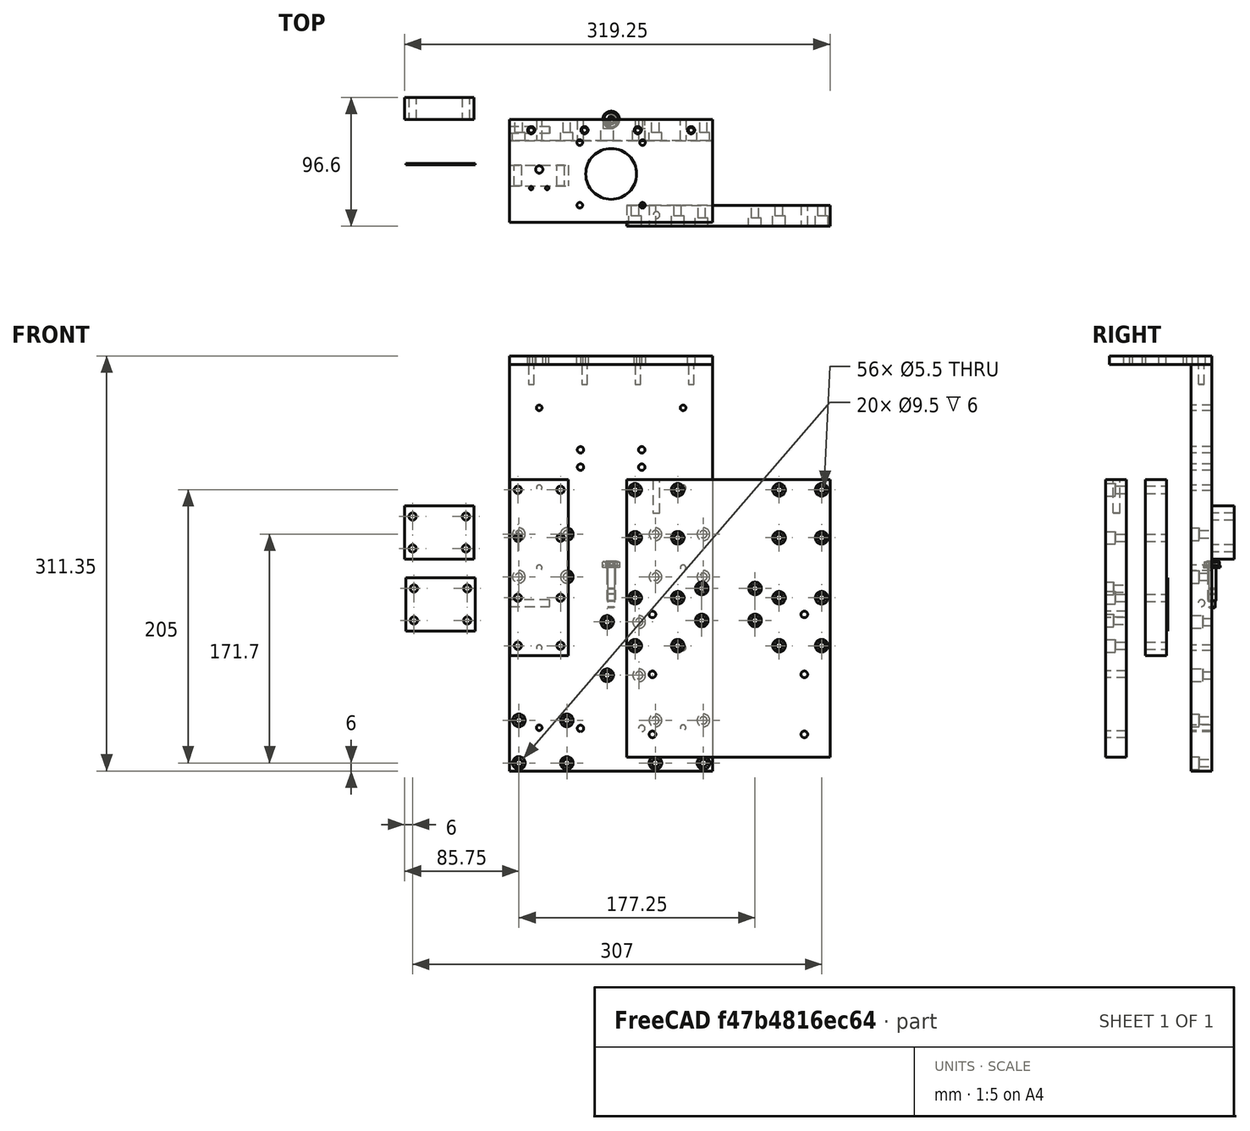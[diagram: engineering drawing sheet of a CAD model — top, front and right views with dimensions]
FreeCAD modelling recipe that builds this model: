
FCSTD DOCUMENT  (FreeCAD 2021.717R24301 +3842 (Git))
Label: Z axis plates
License: Creative Commons Attribution
LicenseURL: http://creativecommons.org/licenses/by/4.0/
objects: App::FeaturePython×171, Part::FeaturePython×140, TechDraw::DrawViewDimension×96, App::LinkElement×44, Sketcher::SketchObject×16, App::Link×16, PartDesign::Pocket×7, PartDesign::Pad×6, PartDesign::Body×6, TechDraw::DrawSVGTemplate×6, TechDraw::DrawViewPart×6, TechDraw::DrawPage×6, PartDesign::ShapeBinder×5, PartDesign::Hole×4, TechDraw::DrawProjGroupItem×4, App::DocumentObjectGroup×3, TechDraw::DrawProjGroup×2, PartDesign::Mirrored×1, TechDraw::DrawViewSection×1, TechDraw::DrawViewAnnotation×1
note: 215 computed .brp shape members not serialized (recipe doc carries the construction recipe); baked Part::Feature solids carry a one-line shape summary decoded from their .brp

FEATURE [Sketcher::SketchObject] Sketch
  FullyConstrained = true
  MapMode = 5
  Placement = pos=(0,0,0) rot=(1,0,0;1.5708rad)
  Support = -> [XZ_Plane]
  sketch-geometry (4):
    g0: LineSegment StartX=-76.25 StartY=152.5 StartZ=0 EndX=76.25 EndY=152.5 EndZ=0
    g1: LineSegment StartX=76.25 StartY=152.5 StartZ=0 EndX=76.25 EndY=-152.5 EndZ=0
    g2: LineSegment StartX=76.25 StartY=-152.5 StartZ=0 EndX=-76.25 EndY=-152.5 EndZ=0
    g3: LineSegment StartX=-76.25 StartY=-152.5 StartZ=0 EndX=-76.25 EndY=152.5 EndZ=0
  constraints (11):
    c: Coincident(g0,g1)
    c: Coincident(g1,g2)
    c: Coincident(g2,g3)
    c: Coincident(g3,g0)
    c: Horizontal(g0)
    c: Horizontal(g2)
    c: Vertical(g1)
    c: Vertical(g3)
    c: Symmetric(g1,g0,g-1)
    c: DistanceX(g0,g0) = 152.5
    c: DistanceY(g1,g1) = 305
FEATURE [PartDesign::Pad] Pad
  ClaimChildren = false
  Direction = (1,1,1)
  Fit = 0
  FitJoin = 0
  InnerFit = 0
  InnerFitJoin = 0
  InnerTaperAngle = 0
  InnerTaperAngleRev = 0
  Length = 15.7
  Length2 = 100
  Linearize = true
  NewSolid = false
  Placement = pos=(0,0,0) rot=(1,0,0;1.5708rad)
  Profile = -> Sketch
  Refine = true
  Suppress = false
  Type = 0
  _ProfileBasedVersion = 0
FEATURE [Sketcher::SketchObject] Sketch001
  FullyConstrained = true
  MapMode = 5
  Placement = pos=(0,0,0) rot=(1,0,0;1.5708rad)
  Support = -> [XZ_Plane]
  sketch-geometry (9):
    g0: Circle CenterX=-54 CenterY=0 CenterZ=0 NormalX=0 NormalY=0 NormalZ=1 AngleXU=0 Radius=2.1
    g1: Circle CenterX=-54 CenterY=60 CenterZ=0 NormalX=0 NormalY=0 NormalZ=1 AngleXU=0 Radius=2.1
    g2: Circle CenterX=-54 CenterY=120 CenterZ=0 NormalX=0 NormalY=0 NormalZ=1 AngleXU=0 Radius=2.1
    g3: Circle CenterX=-54 CenterY=-60 CenterZ=0 NormalX=0 NormalY=0 NormalZ=1 AngleXU=0 Radius=2.1
    g4: Circle CenterX=-54 CenterY=-120 CenterZ=0 NormalX=0 NormalY=0 NormalZ=1 AngleXU=0 Radius=2.1
    g5: LineSegment [constr] StartX=-54 StartY=120 StartZ=0 EndX=-54 EndY=60 EndZ=0
    g6: LineSegment [constr] StartX=-54 StartY=60 StartZ=0 EndX=-54 EndY=0 EndZ=0
    g7: LineSegment [constr] StartX=-54 StartY=0 StartZ=0 EndX=-54 EndY=-60 EndZ=0
    g8: LineSegment [constr] StartX=-54 StartY=-60 StartZ=0 EndX=-54 EndY=-120 EndZ=0
  constraints (23):
    c: Vertical(g4,g3)
    c: Vertical(g3,g0)
    c: Vertical(g0,g1)
    c: Vertical(g1,g2)
    c: Equal(g2,g1)
    c: Equal(g1,g0)
    c: Equal(g0,g3)
    c: Equal(g3,g4)
    c: Coincident(g5,g2)
    c: Coincident(g5,g1)
    c: Coincident(g6,g1)
    c: Coincident(g6,g0)
    c: Coincident(g7,g0)
    c: Coincident(g7,g3)
    c: Coincident(g8,g3)
    c: Coincident(g8,g4)
    c: Equal(g8,g7)
    c: Equal(g7,g6)
    c: Equal(g6,g5)
    c: DistanceY(g5,g5) = 60
    c: DistanceX(g0,g-1) = 54
    c: PointOnObject(g0,g-1)
    c: Radius(g2) = 2.1
FEATURE [PartDesign::Pocket] Pocket
  BaseFeature = -> Pad
  ClaimChildren = false
  Fit = 0
  FitJoin = 0
  InnerFit = 0
  InnerFitJoin = 0
  InnerTaperAngle = 0
  InnerTaperAngleRev = 0
  Length = 5
  Length2 = 100
  Linearize = true
  Midplane = true
  NewSolid = false
  Placement = pos=(0,0,0) rot=(1,0,0;1.5708rad)
  Profile = -> Sketch001
  Refine = true
  Suppress = false
  Type = 1
  _ProfileBasedVersion = 0
FEATURE [PartDesign::Mirrored] Mirrored
  BaseFeature = -> Pocket
  CopyShape = false
  MirrorPlane = -> Sketch001 [V_Axis]
  NewSolid = false
  OriginalSubs = -> [Pocket]
  Originals = -> [Pocket]
  ParallelTransform = true
  Placement = pos=(0,0,0) rot=(1,0,0;1.5708rad)
  Refine = true
  SubTransform = true
  Suppress = false
  _Version = 1
FEATURE [Sketcher::SketchObject] Sketch002
  FullyConstrained = true
  MapMode = 5
  Placement = pos=(0,0,0) rot=(1,0,0;1.5708rad)
  Support = -> [XZ_Plane]
  sketch-geometry (8):
    g0: Circle CenterX=-23 CenterY=-120.525 CenterZ=0 NormalX=0 NormalY=0 NormalZ=1 AngleXU=0 Radius=2.4
    g1: Circle CenterX=23 CenterY=-120.525 CenterZ=0 NormalX=0 NormalY=0 NormalZ=1 AngleXU=0 Radius=2.4
    g2: LineSegment [constr] StartX=-23 StartY=-120.525 StartZ=0 EndX=23 EndY=-120.525 EndZ=0
    g3: GeomPoint [constr] X=0 Y=-120.525 Z=0
    g4: Circle CenterX=-23 CenterY=88.475 CenterZ=0 NormalX=0 NormalY=0 NormalZ=1 AngleXU=0 Radius=2.4
    g5: Circle CenterX=-23 CenterY=75.475 CenterZ=0 NormalX=0 NormalY=0 NormalZ=1 AngleXU=0 Radius=2.4
    g6: Circle CenterX=23 CenterY=88.475 CenterZ=0 NormalX=0 NormalY=0 NormalZ=1 AngleXU=0 Radius=2.4
    g7: Circle CenterX=23 CenterY=75.475 CenterZ=0 NormalX=0 NormalY=0 NormalZ=1 AngleXU=0 Radius=2.4
  constraints (21):
    c: Equal(g1,g0)
    c: Coincident(g2,g0)
    c: Coincident(g2,g1)
    c: Horizontal(g2)
    c: PointOnObject(g3,g-2)
    c: Symmetric(g0,g1,g3)
    c: Radius(g1) = 2.4
    c: DistanceX(g2,g2) = 46
    c: DistanceY(g3,g-1) = 120.525
    c: Equal(g6,g7)
    c: Equal(g7,g5)
    c: Equal(g5,g4)
    c: Equal(g4,g1)
    c: Vertical(g7,g6)
    c: Vertical(g6,g1)
    c: Vertical(g4,g5)
    c: Vertical(g5,g0)
    c: Horizontal(g4,g6)
    c: Horizontal(g5,g7)
    c: DistanceY(g7,g6) = 13
    c: DistanceY(g1,g7) = 196
FEATURE [PartDesign::Pocket] Pocket001
  BaseFeature = -> Mirrored
  ClaimChildren = false
  Fit = 0
  FitJoin = 0
  InnerFit = 0
  InnerFitJoin = 0
  InnerTaperAngle = 0
  InnerTaperAngleRev = 0
  Length = 5
  Length2 = 100
  Linearize = true
  Midplane = true
  NewSolid = false
  Placement = pos=(0,0,0) rot=(1,0,0;1.5708rad)
  Profile = -> Sketch002
  Refine = true
  Suppress = false
  Type = 1
  _ProfileBasedVersion = 0
FEATURE [PartDesign::ShapeBinder] ShapeBinder
  Placement = pos=(0,0,0) rot=(1,0,0;1.5708rad)
  Support = -> [Pocket001]
  TraceSupport = false
FEATURE [Sketcher::SketchObject] Sketch003
  FullyConstrained = true
  MapMode = 5
  Placement = pos=(0,0,0) rot=(1,0,0;1.5708rad)
  Support = -> [XZ_Plane001]
  sketch-geometry (4):
    g0: LineSegment StartX=-76.25 StartY=66 StartZ=0 EndX=76.25 EndY=66 EndZ=0
    g1: LineSegment StartX=76.25 StartY=66 StartZ=0 EndX=76.25 EndY=-142 EndZ=0
    g2: LineSegment StartX=76.25 StartY=-142 StartZ=0 EndX=-76.25 EndY=-142 EndZ=0
    g3: LineSegment StartX=-76.25 StartY=-142 StartZ=0 EndX=-76.25 EndY=66 EndZ=0
  constraints (11):
    c: Coincident(g0,g1)
    c: Coincident(g1,g2)
    c: Coincident(g2,g3)
    c: Coincident(g3,g0)
    c: Horizontal(g2)
    c: Vertical(g1)
    c: Vertical(g3)
    c: DistanceX(g0,g0) = 152.5
    c: DistanceY(g1,g1) = 208
    c: Symmetric(g0,g0,g-2)
    c: DistanceY(g-1,g0) = 66
FEATURE [PartDesign::Pad] Pad001
  ClaimChildren = false
  Direction = (1,1,1)
  Fit = 0
  FitJoin = 0
  InnerFit = 0
  InnerFitJoin = 0
  InnerTaperAngle = 0
  InnerTaperAngleRev = 0
  Length = 15.7
  Length2 = 100
  Linearize = true
  Midplane = true
  NewSolid = false
  Placement = pos=(0,0,0) rot=(1,0,0;1.5708rad)
  Profile = -> Sketch003
  Refine = true
  Suppress = false
  Type = 0
  _ProfileBasedVersion = 0
FEATURE [Sketcher::SketchObject] Sketch004
  ExternalGeometry = -> [ShapeBinder]
  FullyConstrained = true
  MapMode = 5
  Placement = pos=(0,-7.85,-1.7e-15) rot=(1,0,0;1.5708rad)
  Support = -> [Pad001]
  sketch-geometry (21):
    g0: Circle CenterX=-70 CenterY=58.5 CenterZ=0 NormalX=0 NormalY=0 NormalZ=1 AngleXU=0 Radius=2.75
    g1: Circle CenterX=-38 CenterY=58.5 CenterZ=0 NormalX=0 NormalY=0 NormalZ=1 AngleXU=0 Radius=2.75
    g2: Circle CenterX=-70 CenterY=22.5 CenterZ=0 NormalX=0 NormalY=0 NormalZ=1 AngleXU=0 Radius=2.75
    g3: Circle CenterX=-38 CenterY=22.5 CenterZ=0 NormalX=0 NormalY=0 NormalZ=1 AngleXU=0 Radius=2.75
    g4: Circle CenterX=-70 CenterY=-22.5 CenterZ=0 NormalX=0 NormalY=0 NormalZ=1 AngleXU=0 Radius=2.75
    g5: Circle CenterX=-38 CenterY=-22.5 CenterZ=0 NormalX=0 NormalY=0 NormalZ=1 AngleXU=0 Radius=2.75
    g6: Circle CenterX=-70 CenterY=-58.5 CenterZ=0 NormalX=0 NormalY=0 NormalZ=1 AngleXU=0 Radius=2.75
    g7: Circle CenterX=-38 CenterY=-58.5 CenterZ=0 NormalX=0 NormalY=0 NormalZ=1 AngleXU=0 Radius=2.75
    g8: Circle CenterX=38 CenterY=-22.5 CenterZ=0 NormalX=0 NormalY=0 NormalZ=1 AngleXU=0 Radius=2.75
    g9: Circle CenterX=70 CenterY=-22.5 CenterZ=0 NormalX=0 NormalY=0 NormalZ=1 AngleXU=0 Radius=2.75
    g10: Circle CenterX=38 CenterY=-58.5 CenterZ=0 NormalX=0 NormalY=0 NormalZ=1 AngleXU=0 Radius=2.75
    g11: Circle CenterX=70 CenterY=-58.5 CenterZ=0 NormalX=0 NormalY=0 NormalZ=1 AngleXU=0 Radius=2.75
    g12: Circle CenterX=38 CenterY=22.5 CenterZ=0 NormalX=0 NormalY=0 NormalZ=1 AngleXU=0 Radius=2.75
    g13: Circle CenterX=70 CenterY=22.5 CenterZ=0 NormalX=0 NormalY=0 NormalZ=1 AngleXU=0 Radius=2.75
    g14: Circle CenterX=38 CenterY=58.5 CenterZ=0 NormalX=0 NormalY=0 NormalZ=1 AngleXU=0 Radius=2.75
    g15: Circle CenterX=70 CenterY=58.5 CenterZ=0 NormalX=0 NormalY=0 NormalZ=1 AngleXU=0 Radius=2.75
    g16: LineSegment [constr] StartX=-70 StartY=58.5 StartZ=0 EndX=-70 EndY=22.5 EndZ=0
    g17: LineSegment [constr] StartX=-70 StartY=-22.5 StartZ=0 EndX=-70 EndY=-58.5 EndZ=0
    g18: LineSegment [constr] StartX=-70 StartY=58.5 StartZ=0 EndX=-38 EndY=58.5 EndZ=0
    g19: LineSegment [constr] StartX=38 StartY=58.5 StartZ=0 EndX=70 EndY=58.5 EndZ=0
    g20: GeomPoint [constr] X=-54 Y=58.5 Z=0
  constraints (56):
    c: Horizontal(g0,g1)
    c: Horizontal(g1,g14)
    c: Horizontal(g14,g15)
    c: Horizontal(g2,g3)
    c: Horizontal(g3,g12)
    c: Horizontal(g12,g13)
    c: Horizontal(g4,g5)
    c: Horizontal(g5,g8)
    c: Horizontal(g8,g9)
    c: Horizontal(g6,g7)
    c: Horizontal(g7,g10)
    c: Horizontal(g10,g11)
    c: Equal(g0,g1)
    c: Equal(g1,g14)
    c: Equal(g14,g15)
    c: Equal(g15,g12)
    c: Equal(g12,g13)
    c: Equal(g13,g3)
    c: Equal(g3,g2)
    c: Equal(g2,g4)
    c: Equal(g4,g5)
    c: Equal(g5,g8)
    c: Equal(g8,g9)
    c: Equal(g9,g10)
    c: Equal(g10,g11)
    c: Equal(g11,g7)
    c: Equal(g7,g6)
    c: Vertical(g0,g2)
    c: Vertical(g2,g4)
    c: Vertical(g4,g6)
    c: Vertical(g7,g5)
    c: Vertical(g5,g3)
    c: Vertical(g3,g1)
    c: Vertical(g14,g12)
    c: Vertical(g12,g8)
    c: Vertical(g8,g10)
    c: Vertical(g15,g13)
    c: Vertical(g13,g9)
    c: Vertical(g9,g11)
    c: Coincident(g16,g0)
    c: Coincident(g16,g2)
    c: Coincident(g17,g4)
    c: Coincident(g17,g6)
    c: Coincident(g18,g0)
    c: Coincident(g18,g1)
    c: Coincident(g19,g14)
    c: Coincident(g19,g15)
    c: Equal(g18,g19)
    c: Equal(g16,g17)
    c: Symmetric(g2,g9,g-1)
    c: DistanceX(g18,g18) = 32
    c: DistanceY(g16,g16) = 36
    c: Diameter(g15) = 5.5
    c: DistanceY(g4,g2) = 45
    c: Vertical(g20,g-3)
    c: Symmetric(g0,g1,g20)
FEATURE [PartDesign::Hole] Hole  label="Carriages mounts"
  BaseFeature = -> Pad001
  ClaimChildren = false
  CustomThreadClearance = 0
  Depth = 25
  DepthType = 1
  Diameter = 5.5
  DrillForDepth = false
  DrillPoint = 1
  DrillPointAngle = 118
  Fit = 0
  FitJoin = 0
  HoleCutCountersinkAngle = 90
  HoleCutCustomValues = false
  HoleCutDepth = 7.5
  HoleCutDiameter = 9.5
  HoleCutType = 1
  InnerFit = 0
  InnerFitJoin = 0
  ModelThread = false
  NewSolid = false
  Placement = pos=(0,0,0) rot=(1,0,0;1.5708rad)
  Profile = -> Sketch004
  Refine = true
  Suppress = false
  Tapered = false
  TaperedAngle = 90
  ThreadClass = 0
  ThreadDepth = 444.18
  ThreadDepthType = 0
  ThreadDirection = 0
  ThreadFit = 0
  ThreadSize = 0
  ThreadType = 0
  Threaded = false
  UseCustomThreadClearance = false
  _ProfileBasedVersion = 0
FEATURE [Sketcher::SketchObject] Sketch005
  FullyConstrained = true
  MapMode = 5
  Placement = pos=(0,-7.85,-1.7e-15) rot=(1,0,0;1.5708rad)
  Support = -> [Hole]
  sketch-geometry (4):
    g0: Circle CenterX=-20 CenterY=-15.525 CenterZ=0 NormalX=0 NormalY=0 NormalZ=1 AngleXU=0 Radius=2.75
    g1: Circle CenterX=20 CenterY=-15.525 CenterZ=0 NormalX=0 NormalY=0 NormalZ=1 AngleXU=0 Radius=2.75
    g2: Circle CenterX=-20 CenterY=-39.525 CenterZ=0 NormalX=0 NormalY=0 NormalZ=1 AngleXU=0 Radius=2.75
    g3: Circle CenterX=20 CenterY=-39.525 CenterZ=0 NormalX=0 NormalY=0 NormalZ=1 AngleXU=0 Radius=2.75
  constraints (11):
    c: Horizontal(g2,g3)
    c: Vertical(g0,g2)
    c: Vertical(g1,g3)
    c: DistanceX(g0,g1) = 40
    c: DistanceY(g3,g1) = 24
    c: Diameter(g0) = 5.5
    c: Equal(g0,g1)
    c: Equal(g1,g3)
    c: Equal(g3,g2)
    c: DistanceY(g1,g-1) = 15.525
    c: Symmetric(g1,g0,g-2)
FEATURE [PartDesign::Hole] Hole001  label="Screw mount"
  BaseFeature = -> Hole
  ClaimChildren = false
  CustomThreadClearance = 0
  Depth = 25
  DepthType = 1
  Diameter = 5.5
  DrillForDepth = false
  DrillPoint = 1
  DrillPointAngle = 118
  Fit = 0
  FitJoin = 0
  HoleCutCountersinkAngle = 90
  HoleCutCustomValues = false
  HoleCutDepth = 6
  HoleCutDiameter = 9.5
  HoleCutType = 1
  InnerFit = 0
  InnerFitJoin = 0
  ModelThread = false
  NewSolid = false
  Placement = pos=(0,0,0) rot=(1,0,0;1.5708rad)
  Profile = -> Sketch005
  Refine = true
  Suppress = false
  Tapered = false
  TaperedAngle = 90
  ThreadClass = 0
  ThreadDepth = 444.18
  ThreadDepthType = 0
  ThreadDirection = 0
  ThreadFit = 0
  ThreadSize = 0
  ThreadType = 0
  Threaded = false
  UseCustomThreadClearance = false
  _ProfileBasedVersion = 0
FEATURE [PartDesign::ShapeBinder] ShapeBinder001
  Placement = pos=(0,0,0) rot=(1,0,0;1.5708rad)
  Support = -> [Hole001]
  TraceSupport = false
FEATURE [Sketcher::SketchObject] Sketch006
  ExternalGeometry = -> [ShapeBinder001]
  FullyConstrained = true
  MapMode = 5
  Placement = pos=(0,0,0) rot=(1,0,0;1.5708rad)
  Support = -> [XZ_Plane002]
  sketch-geometry (16):
    g0: LineSegment StartX=-76 StartY=66 StartZ=0 EndX=-32 EndY=66 EndZ=0
    g1: LineSegment StartX=-32 StartY=66 StartZ=0 EndX=-32 EndY=-66 EndZ=0
    g2: LineSegment StartX=-32 StartY=-66 StartZ=0 EndX=-76 EndY=-66 EndZ=0
    g3: LineSegment StartX=-76 StartY=-66 StartZ=0 EndX=-76 EndY=66 EndZ=0
    g4: LineSegment [constr] StartX=-70 StartY=58.5 StartZ=0 EndX=-76 EndY=58.5 EndZ=0
    g5: LineSegment [constr] StartX=-38 StartY=58.5 StartZ=0 EndX=-32 EndY=58.5 EndZ=0
    g6: LineSegment [constr] StartX=-38 StartY=58.5 StartZ=0 EndX=-38 EndY=66 EndZ=0
    g7: LineSegment [constr] StartX=-38 StartY=-58.5 StartZ=0 EndX=-38 EndY=-66 EndZ=0
    g8: Circle CenterX=-70 CenterY=58.5 CenterZ=0 NormalX=0 NormalY=0 NormalZ=1 AngleXU=0 Radius=2.75
    g9: Circle CenterX=-38 CenterY=58.5 CenterZ=0 NormalX=0 NormalY=0 NormalZ=1 AngleXU=0 Radius=2.75
    g10: Circle CenterX=-70 CenterY=22.5 CenterZ=0 NormalX=0 NormalY=0 NormalZ=1 AngleXU=0 Radius=2.75
    g11: Circle CenterX=-38 CenterY=22.5 CenterZ=0 NormalX=0 NormalY=0 NormalZ=1 AngleXU=0 Radius=2.75
    g12: Circle CenterX=-70 CenterY=-22.5 CenterZ=0 NormalX=0 NormalY=0 NormalZ=1 AngleXU=0 Radius=2.75
    g13: Circle CenterX=-38 CenterY=-22.5 CenterZ=0 NormalX=0 NormalY=0 NormalZ=1 AngleXU=0 Radius=2.75
    g14: Circle CenterX=-70 CenterY=-58.5 CenterZ=0 NormalX=0 NormalY=0 NormalZ=1 AngleXU=0 Radius=2.75
    g15: Circle CenterX=-38 CenterY=-58.5 CenterZ=0 NormalX=0 NormalY=0 NormalZ=1 AngleXU=0 Radius=2.75
  constraints (40):
    c: Coincident(g0,g1)
    c: Coincident(g1,g2)
    c: Coincident(g2,g3)
    c: Coincident(g3,g0)
    c: Horizontal(g0)
    c: Horizontal(g2)
    c: Vertical(g1)
    c: Vertical(g3)
    c: DistanceX(g2,g2) = 44
    c: DistanceY(g1,g1) = 132
    c: Coincident(g4,g-3)
    c: PointOnObject(g4,g3)
    c: Horizontal(g4)
    c: Coincident(g5,g-4)
    c: PointOnObject(g5,g1)
    c: Horizontal(g5)
    c: Equal(g5,g4)
    c: Coincident(g6,g-4)
    c: PointOnObject(g6,g0)
    c: Coincident(g7,g-10)
    c: PointOnObject(g7,g2)
    c: Vertical(g7)
    c: Vertical(g6)
    c: Equal(g6,g7)
    c: Coincident(g8,g-3)
    c: Coincident(g9,g-4)
    c: Coincident(g10,g-5)
    c: Coincident(g11,g-6)
    c: Coincident(g12,g-7)
    c: Coincident(g13,g-8)
    c: Coincident(g14,g-9)
    c: Coincident(g15,g-10)
    c: Equal(g15,g14)
    c: Equal(g14,g12)
    c: Equal(g12,g13)
    c: Equal(g13,g10)
    c: Equal(g10,g11)
    c: Equal(g11,g8)
    c: Equal(g8,g9)
    c: Equal(g9,g-4)
FEATURE [PartDesign::Pad] Pad002
  ClaimChildren = false
  Direction = (1,1,1)
  Fit = 0
  FitJoin = 0
  InnerFit = 0
  InnerFitJoin = 0
  InnerTaperAngle = 0
  InnerTaperAngleRev = 0
  Length = 15.7
  Length2 = 100
  Linearize = true
  Midplane = true
  NewSolid = false
  Placement = pos=(0,0,0) rot=(1,0,0;1.5708rad)
  Profile = -> Sketch006
  Refine = true
  Suppress = false
  Type = 0
  _ProfileBasedVersion = 0
FEATURE [PartDesign::Body] Body002  label="Shim"
  AutoGroupSolids = false
  ExportMode = 0
  Group = -> [ShapeBinder001,Sketch006,Pad002]
  Origin = -> Origin002
  Placement = pos=(0,-42,0) rot=(0,0,1;0rad)
  Tip = -> Pad002
  _ExportChildren = -> [ShapeBinder001,Pad002]
  _GroupVersion = 1
FEATURE [App::Link] Link  label="Link(Backplate)"
  AutoLinkLabel = true
  AutoPlacement = true
  LinkedObject = -> Body
  SyncGroupVisibility = false
  _LinkVersion = 1
FEATURE [App::Link] Link001  label="Link001(Shim)"
  AutoLinkLabel = true
  AutoPlacement = true
  LinkPlacement = pos=(0,-42,0) rot=(0,0,1;0rad)
  LinkedObject = -> Body002
  Placement = pos=(0,-42,0) rot=(0,0,1;0rad)
  SyncGroupVisibility = false
  _LinkVersion = 1
FEATURE [Part::FeaturePython] Parts002  # WARN: FeaturePython — macro-defined, semantics opaque (R4)
  Group = -> [Link001]
  GroupMode = 0
  _LinkVersion = 1
FEATURE [App::Link] Link002  label="Link002(Frontplate)"
  AutoLinkLabel = true
  AutoPlacement = true
  LinkPlacement = pos=(88,-72,0) rot=(0,0,1;0rad)
  LinkedObject = -> Body001
  Placement = pos=(88,-72,0) rot=(0,0,1;0rad)
  SyncGroupVisibility = false
  _LinkVersion = 1
FEATURE [PartDesign::ShapeBinder] ShapeBinder002
  Placement = pos=(0,0,0) rot=(1,0,0;1.5708rad)
  TraceSupport = false
FEATURE [Sketcher::SketchObject] Sketch008
  ExternalGeometry = -> [ShapeBinder002]
  FullyConstrained = true
  MapMode = 5
  Placement = pos=(0,0,0) rot=(1,0,0;1.5708rad)
  Support = -> [XZ_Plane003]
  sketch-geometry (10):
    g0: LineSegment StartX=-26 StartY=-7.525 StartZ=0 EndX=26 EndY=-7.525 EndZ=0
    g1: LineSegment StartX=26 StartY=-7.525 StartZ=0 EndX=26 EndY=-47.525 EndZ=0
    g2: LineSegment StartX=26 StartY=-47.525 StartZ=0 EndX=-26 EndY=-47.525 EndZ=0
    g3: LineSegment StartX=-26 StartY=-47.525 StartZ=0 EndX=-26 EndY=-7.525 EndZ=0
    g4: Circle CenterX=20 CenterY=-39.525 CenterZ=0 NormalX=0 NormalY=0 NormalZ=1 AngleXU=0 Radius=2.75
    g5: Circle CenterX=-20 CenterY=-15.525 CenterZ=0 NormalX=0 NormalY=0 NormalZ=1 AngleXU=0 Radius=2.75
    g6: Circle CenterX=-20 CenterY=-39.525 CenterZ=0 NormalX=0 NormalY=0 NormalZ=1 AngleXU=0 Radius=2.75
    g7: Circle CenterX=20 CenterY=-15.525 CenterZ=0 NormalX=0 NormalY=0 NormalZ=1 AngleXU=0 Radius=2.75
    g8: LineSegment [constr] StartX=20 StartY=-15.525 StartZ=0 EndX=20 EndY=-7.525 EndZ=0
    g9: LineSegment [constr] StartX=20 StartY=-39.525 StartZ=0 EndX=20 EndY=-47.525 EndZ=0
  constraints (25):
    c: Coincident(g0,g1)
    c: Coincident(g1,g2)
    c: Coincident(g2,g3)
    c: Coincident(g3,g0)
    c: Horizontal(g2)
    c: Vertical(g1)
    c: Vertical(g3)
    c: DistanceX(g0,g0) = 52
    c: DistanceY(g1,g1) = 40
    c: Equal(g7,g6)
    c: Equal(g6,g4)
    c: Equal(g4,g5)
    c: Symmetric(g0,g0,g-2)
    c: Coincident(g5,g-3)
    c: Coincident(g7,g-4)
    c: Equal(g-4,g7)
    c: Coincident(g-5,g6)
    c: Coincident(g4,g-6)
    c: Coincident(g8,g7)
    c: PointOnObject(g8,g0)
    c: Vertical(g8)
    c: Coincident(g9,g4)
    c: PointOnObject(g9,g2)
    c: Vertical(g9)
    c: Equal(g9,g8)
FEATURE [PartDesign::Pad] Pad003
  ClaimChildren = false
  Direction = (1,1,1)
  Fit = 0
  FitJoin = 0
  InnerFit = 0
  InnerFitJoin = 0
  InnerTaperAngle = 0
  InnerTaperAngleRev = 0
  Length = 0.7
  Length2 = 100
  Linearize = true
  NewSolid = false
  Placement = pos=(0,0,0) rot=(1,0,0;1.5708rad)
  Profile = -> Sketch008
  Refine = true
  Suppress = false
  Type = 0
  _ProfileBasedVersion = 0
FEATURE [PartDesign::Body] Body003  label="Nut-shim"
  AutoGroupSolids = false
  ExportMode = 0
  Group = -> [ShapeBinder002,Sketch008,Pad003]
  Origin = -> Origin003
  Placement = pos=(-128,-33,0) rot=(0,0,1;0rad)
  Tip = -> Pad003
  _ExportChildren = -> [ShapeBinder002,Pad003]
  _GroupVersion = 1
FEATURE [App::Link] Link003  label="Link003(Nut-shim)"
  AutoLinkLabel = true
  AutoPlacement = true
  LinkPlacement = pos=(-128,-33,0) rot=(0,0,1;0rad)
  LinkedObject = -> Body003
  Placement = pos=(-128,-33,0) rot=(0,0,1;0rad)
  SyncGroupVisibility = false
  _LinkVersion = 1
FEATURE [Part::FeaturePython] Parts003  # WARN: FeaturePython — macro-defined, semantics opaque (R4)
  Group = -> [Link003]
  GroupMode = 0
  _LinkVersion = 1
FEATURE [Sketcher::SketchObject] Sketch009
  ExternalGeometry = -> [Pocket001]
  FullyConstrained = true
  MapMode = 5
  Placement = pos=(0,-15.7,-3.5e-15) rot=(1,0,0;1.5708rad)
  Support = -> [Pocket001]
  sketch-geometry (22):
    g0: Circle CenterX=-69.25 CenterY=-146.5 CenterZ=0 NormalX=0 NormalY=0 NormalZ=1 AngleXU=0 Radius=2.75
    g1: Circle CenterX=-69.25 CenterY=-114.5 CenterZ=0 NormalX=0 NormalY=0 NormalZ=1 AngleXU=0 Radius=2.75
    g2: Circle CenterX=-33.25 CenterY=-114.5 CenterZ=0 NormalX=0 NormalY=0 NormalZ=1 AngleXU=0 Radius=2.75
    g3: Circle CenterX=-33.25 CenterY=-146.5 CenterZ=0 NormalX=0 NormalY=0 NormalZ=1 AngleXU=0 Radius=2.75
    g4: Circle CenterX=33.25 CenterY=-114.5 CenterZ=0 NormalX=0 NormalY=0 NormalZ=1 AngleXU=0 Radius=2.75
    g5: Circle CenterX=69.25 CenterY=-114.5 CenterZ=0 NormalX=0 NormalY=0 NormalZ=1 AngleXU=0 Radius=2.75
    g6: Circle CenterX=33.25 CenterY=-146.5 CenterZ=0 NormalX=0 NormalY=0 NormalZ=1 AngleXU=0 Radius=2.75
    g7: Circle CenterX=69.25 CenterY=-146.5 CenterZ=0 NormalX=0 NormalY=0 NormalZ=1 AngleXU=0 Radius=2.75
    g8: LineSegment [constr] StartX=-69.25 StartY=-146.5 StartZ=0 EndX=-33.25 EndY=-146.5 EndZ=0
    g9: LineSegment [constr] StartX=33.25 StartY=-146.5 StartZ=0 EndX=69.25 EndY=-146.5 EndZ=0
    g10: Circle CenterX=-69.25 CenterY=-6.8 CenterZ=0 NormalX=0 NormalY=0 NormalZ=1 AngleXU=0 Radius=2.75
    g11: Circle CenterX=-69.25 CenterY=25.2 CenterZ=0 NormalX=0 NormalY=0 NormalZ=1 AngleXU=0 Radius=2.75
    g12: Circle CenterX=-33.25 CenterY=-6.8 CenterZ=0 NormalX=0 NormalY=0 NormalZ=1 AngleXU=0 Radius=2.75
    g13: Circle CenterX=-33.25 CenterY=25.2 CenterZ=0 NormalX=0 NormalY=0 NormalZ=1 AngleXU=0 Radius=2.75
    g14: Circle CenterX=33.25 CenterY=-6.8 CenterZ=0 NormalX=0 NormalY=0 NormalZ=1 AngleXU=0 Radius=2.75
    g15: Circle CenterX=33.25 CenterY=25.2 CenterZ=0 NormalX=0 NormalY=0 NormalZ=1 AngleXU=0 Radius=2.75
    g16: Circle CenterX=69.25 CenterY=-6.8 CenterZ=0 NormalX=0 NormalY=0 NormalZ=1 AngleXU=0 Radius=2.75
    g17: Circle CenterX=69.25 CenterY=25.2 CenterZ=0 NormalX=0 NormalY=0 NormalZ=1 AngleXU=0 Radius=2.75
    g18: GeomPoint [constr] X=69.25 Y=9.2 Z=0
    g19: GeomPoint [constr] X=69.25 Y=-130.5 Z=0
    g20: LineSegment [constr] StartX=-69.25 StartY=-146.5 StartZ=0 EndX=-69.25 EndY=-114.5 EndZ=0
    g21: LineSegment [constr] StartX=-69.25 StartY=25.2 StartZ=0 EndX=-69.25 EndY=-6.8 EndZ=0
  constraints (57):
    c: Horizontal(g5,g4)
    c: Horizontal(g4,g2)
    c: Horizontal(g2,g1)
    c: Horizontal(g0,g3)
    c: Horizontal(g6,g7)
    c: Vertical(g5,g7)
    c: Vertical(g4,g6)
    c: Vertical(g2,g3)
    c: Vertical(g1,g0)
    c: Equal(g1,g2)
    c: Equal(g2,g4)
    c: Equal(g4,g5)
    c: Equal(g5,g6)
    c: Equal(g6,g7)
    c: Equal(g7,g3)
    c: Equal(g3,g0)
    c: Diameter(g1) = 5.5
    c: Coincident(g8,g0)
    c: Coincident(g8,g3)
    c: Coincident(g9,g6)
    c: Coincident(g9,g7)
    c: Equal(g9,g8)
    c: DistanceY(g0,g1) = 32
    c: DistanceX(g8,g8) = 36
    c: Symmetric(g6,g3,g-2)
    c: DistanceY(g-3,g0) = 6
    c: DistanceX(g-3,g0) = 7
    c: Equal(g10,g12)
    c: Equal(g12,g14)
    c: Equal(g14,g16)
    c: Equal(g16,g17)
    c: Equal(g17,g15)
    c: Equal(g15,g13)
    c: Equal(g13,g11)
    c: Equal(g11,g1)
    c: Horizontal(g10,g12)
    c: Horizontal(g12,g14)
    c: Horizontal(g14,g16)
    c: Horizontal(g11,g13)
    c: Horizontal(g13,g15)
    c: Horizontal(g15,g17)
    c: Vertical(g10,g11)
    c: Vertical(g11,g1)
    c: Vertical(g12,g13)
    c: Vertical(g13,g2)
    c: Vertical(g14,g15)
    c: Vertical(g15,g4)
    c: Vertical(g16,g17)
    c: Vertical(g17,g5)
    c: Symmetric(g16,g17,g18)
    c: Symmetric(g5,g7,g19)
    c: DistanceY(g19,g18) = 139.7
    c: Coincident(g20,g0)
    c: Coincident(g20,g1)
    c: Coincident(g21,g11)
    c: Coincident(g21,g10)
    c: Equal(g21,g20)
FEATURE [PartDesign::Hole] Hole003
  BaseFeature = -> Pocket001
  ClaimChildren = false
  CustomThreadClearance = 0
  Depth = 25
  DepthType = 1
  Diameter = 5.5
  DrillForDepth = false
  DrillPoint = 1
  DrillPointAngle = 118
  Fit = 0
  FitJoin = 0
  HoleCutCountersinkAngle = 90
  HoleCutCustomValues = false
  HoleCutDepth = 6
  HoleCutDiameter = 9.5
  HoleCutType = 1
  InnerFit = 0
  InnerFitJoin = 0
  ModelThread = false
  NewSolid = false
  Placement = pos=(0,0,0) rot=(1,0,0;1.5708rad)
  Profile = -> Sketch009
  Refine = true
  Suppress = false
  Tapered = false
  TaperedAngle = 90
  ThreadClass = 0
  ThreadDepth = 689.55
  ThreadDepthType = 0
  ThreadDirection = 0
  ThreadFit = 0
  ThreadSize = 0
  ThreadType = 0
  Threaded = false
  UseCustomThreadClearance = false
  _ProfileBasedVersion = 0
FEATURE [App::Link] Link004  label="Link004(Motor-bracket)"
  AutoLinkLabel = true
  AutoPlacement = true
  LinkedObject = -> Body004
  SyncGroupVisibility = false
  _LinkVersion = 1
FEATURE [Sketcher::SketchObject] Sketch011
  ExternalGeometry = -> [Hole003]
  FullyConstrained = true
  MapMode = 5
  Placement = pos=(0,0,152.5) rot=(0,0,1;3.14159rad)
  Support = -> [Hole003]
  sketch-geometry (9):
    g0: LineSegment [constr] StartX=-60 StartY=15.7 StartZ=0 EndX=-60 EndY=7.85 EndZ=0
    g1: LineSegment [constr] StartX=-60 StartY=7.85 StartZ=0 EndX=-60 EndY=0 EndZ=0
    g2: LineSegment [constr] StartX=-60 StartY=7.85 StartZ=0 EndX=-20 EndY=7.85 EndZ=0
    g3: LineSegment [constr] StartX=-20 StartY=7.85 StartZ=0 EndX=20 EndY=7.85 EndZ=0
    g4: LineSegment [constr] StartX=20 StartY=7.85 StartZ=0 EndX=60 EndY=7.85 EndZ=0
    g5: Circle CenterX=-60 CenterY=7.85 CenterZ=0 NormalX=0 NormalY=0 NormalZ=1 AngleXU=0 Radius=2.1
    g6: Circle CenterX=-20 CenterY=7.85 CenterZ=0 NormalX=0 NormalY=0 NormalZ=1 AngleXU=0 Radius=2.1
    g7: Circle CenterX=20 CenterY=7.85 CenterZ=0 NormalX=0 NormalY=0 NormalZ=1 AngleXU=0 Radius=2.1
    g8: Circle CenterX=60 CenterY=7.85 CenterZ=0 NormalX=0 NormalY=0 NormalZ=1 AngleXU=0 Radius=2.1
  constraints (23):
    c: PointOnObject(g0,g-3)
    c: Vertical(g0)
    c: Coincident(g1,g0)
    c: PointOnObject(g1,g-1)
    c: Coincident(g2,g0)
    c: Horizontal(g2)
    c: Coincident(g3,g2)
    c: Coincident(g4,g3)
    c: Horizontal(g4)
    c: Vertical(g1)
    c: Equal(g1,g0)
    c: Equal(g2,g3)
    c: Equal(g3,g4)
    c: Symmetric(g2,g3,g-2)
    c: Coincident(g5,g0)
    c: Coincident(g6,g2)
    c: Coincident(g7,g3)
    c: Coincident(g8,g4)
    c: Equal(g8,g7)
    c: Equal(g7,g6)
    c: Equal(g6,g5)
    c: Diameter(g8) = 4.2
    c: DistanceX(g3,g3) = 40
FEATURE [PartDesign::Pocket] Pocket002
  BaseFeature = -> Hole003
  ClaimChildren = false
  Fit = 0
  FitJoin = 0
  InnerFit = 0
  InnerFitJoin = 0
  InnerTaperAngle = 0
  InnerTaperAngleRev = 0
  Length = 15
  Length2 = 100
  Linearize = true
  NewSolid = false
  Placement = pos=(0,0,0) rot=(1,0,0;1.5708rad)
  Profile = -> Sketch011
  Refine = true
  Suppress = false
  Type = 0
  _ProfileBasedVersion = 0
FEATURE [PartDesign::ShapeBinder] ShapeBinder003
  Placement = pos=(0,0,0) rot=(1,0,0;1.5708rad)
  Support = -> [Pocket002]
  TraceSupport = false
FEATURE [Sketcher::SketchObject] Sketch010
  ExternalGeometry = -> [ShapeBinder003]
  FullyConstrained = true
  MapMode = 5
  Placement = pos=(0,-3.39e-14,152.5) rot=(0,0,1;3.14159rad)
  Support = -> [ShapeBinder003]
  sketch-geometry (19):
    g0: LineSegment StartX=-76.25 StartY=77.1 StartZ=0 EndX=76.25 EndY=77.1 EndZ=0
    g1: LineSegment StartX=76.25 StartY=77.1 StartZ=0 EndX=76.25 EndY=0 EndZ=0
    g2: LineSegment StartX=-76.25 StartY=0 StartZ=0 EndX=-76.25 EndY=77.1 EndZ=0
    g3: Circle CenterX=0 CenterY=40.7 CenterZ=0 NormalX=0 NormalY=0 NormalZ=1 AngleXU=0 Radius=19.05
    g4: Circle CenterX=-23.55 CenterY=64.25 CenterZ=0 NormalX=0 NormalY=0 NormalZ=1 AngleXU=0 Radius=2.1
    g5: Circle CenterX=23.55 CenterY=64.25 CenterZ=0 NormalX=0 NormalY=0 NormalZ=1 AngleXU=0 Radius=2.1
    g6: Circle CenterX=-23.55 CenterY=17.15 CenterZ=0 NormalX=0 NormalY=0 NormalZ=1 AngleXU=0 Radius=2.1
    g7: Circle CenterX=23.55 CenterY=17.15 CenterZ=0 NormalX=0 NormalY=0 NormalZ=1 AngleXU=0 Radius=2.1
    g8: LineSegment [constr] StartX=-23.55 StartY=64.25 StartZ=0 EndX=23.55 EndY=64.25 EndZ=0
    g9: LineSegment [constr] StartX=23.55 StartY=64.25 StartZ=0 EndX=23.55 EndY=17.15 EndZ=0
    g10: LineSegment [constr] StartX=-28.2 StartY=68.9 StartZ=0 EndX=28.2 EndY=68.9 EndZ=0
    g11: LineSegment [constr] StartX=28.2 StartY=68.9 StartZ=0 EndX=28.2 EndY=12.5 EndZ=0
    g12: LineSegment [constr] StartX=28.2 StartY=12.5 StartZ=0 EndX=-28.2 EndY=12.5 EndZ=0
    g13: LineSegment [constr] StartX=-28.2 StartY=12.5 StartZ=0 EndX=-28.2 EndY=68.9 EndZ=0
    g14: Circle CenterX=-60 CenterY=7.85 CenterZ=0 NormalX=0 NormalY=0 NormalZ=1 AngleXU=0 Radius=2.75
    g15: Circle CenterX=-20 CenterY=7.85 CenterZ=0 NormalX=0 NormalY=0 NormalZ=1 AngleXU=0 Radius=2.75
    g16: Circle CenterX=20 CenterY=7.85 CenterZ=0 NormalX=0 NormalY=0 NormalZ=1 AngleXU=0 Radius=2.75
    g17: Circle CenterX=60 CenterY=7.85 CenterZ=0 NormalX=0 NormalY=0 NormalZ=1 AngleXU=0 Radius=2.75
    g18: LineSegment StartX=-76.25 StartY=0 StartZ=0 EndX=76.25 EndY=0 EndZ=0
  constraints (48):
    c: Coincident(g0,g1)
    c: Coincident(g2,g0)
    c: Horizontal(g0)
    c: Vertical(g1)
    c: Vertical(g2)
    c: Symmetric(g2,g1,g-1)
    c: PointOnObject(g3,g-2)
    c: Diameter(g3) = 38.1
    c: Vertical(g7,g5)
    c: Vertical(g4,g6)
    c: Horizontal(g4,g5)
    c: Horizontal(g6,g7)
    c: Symmetric(g7,g4,g3)
    c: DistanceX(g4,g5) = 47.1
    c: Equal(g5,g4)
    c: Equal(g4,g6)
    c: Equal(g6,g7)
    c: Diameter(g5) = 4.2
    c: Coincident(g8,g4)
    c: Coincident(g8,g5)
    c: Coincident(g9,g5)
    c: Coincident(g9,g7)
    c: Equal(g9,g8)
    c: Coincident(g10,g11)
    c: Coincident(g11,g12)
    c: Coincident(g12,g13)
    c: Coincident(g13,g10)
    c: Horizontal(g10)
    c: Horizontal(g12)
    c: Vertical(g11)
    c: Vertical(g13)
    c: Symmetric(g10,g11,g3)
    c: Equal(g11,g10)
    c: DistanceY(g13,g13) = 56.4
    c: DistanceX(g0,g0) = 152.5
    c: DistanceY(g-4,g3) = 25
    c: Coincident(g14,g-5)
    c: Coincident(g15,g-6)
    c: Coincident(g16,g-7)
    c: Coincident(g17,g-8)
    c: Equal(g17,g16)
    c: Equal(g16,g15)
    c: Equal(g15,g14)
    c: Diameter(g14) = 5.5
    c: Coincident(g18,g2)
    c: Coincident(g18,g1)
    c: Horizontal(g18)
    c: DistanceY(g2,g2) = 77.1
FEATURE [PartDesign::Pad] Pad004
  ClaimChildren = false
  Direction = (1,1,1)
  Fit = 0
  FitJoin = 0
  InnerFit = 0
  InnerFitJoin = 0
  InnerTaperAngle = 0
  InnerTaperAngleRev = 0
  Length = 6.35
  Length2 = 100
  Linearize = true
  NewSolid = false
  Placement = pos=(0,0,0) rot=(1,0,0;1.5708rad)
  Profile = -> Sketch010
  Refine = true
  Suppress = false
  Type = 0
  _ProfileBasedVersion = 0
FEATURE [Sketcher::SketchObject] Sketch012
  ExternalGeometry = -> [Pad001]
  FullyConstrained = true
  MapMode = 5
  Placement = pos=(0,-7.85,-1.7e-15) rot=(1,0,0;1.5708rad)
  sketch-geometry (6):
    g0: Circle CenterX=-57 CenterY=-80 CenterZ=0 NormalX=0 NormalY=0 NormalZ=1 AngleXU=0 Radius=2.5
    g1: Circle CenterX=-57 CenterY=-125 CenterZ=0 NormalX=0 NormalY=0 NormalZ=1 AngleXU=0 Radius=2.5
    g2: Circle CenterX=57 CenterY=-80 CenterZ=0 NormalX=0 NormalY=0 NormalZ=1 AngleXU=0 Radius=2.5
    g3: Circle CenterX=57 CenterY=-125 CenterZ=0 NormalX=0 NormalY=0 NormalZ=1 AngleXU=0 Radius=2.5
    g4: Circle CenterX=-57 CenterY=-35 CenterZ=0 NormalX=0 NormalY=0 NormalZ=1 AngleXU=0 Radius=2.5
    g5: Circle CenterX=57 CenterY=-35 CenterZ=0 NormalX=0 NormalY=0 NormalZ=1 AngleXU=0 Radius=2.5
  constraints (17):
    c: Vertical(g0,g1)
    c: Horizontal(g1,g3)
    c: Equal(g1,g0)
    c: Equal(g0,g2)
    c: Equal(g2,g3)
    c: Diameter(g2) = 5
    c: Symmetric(g2,g0,g-2)
    c: DistanceX(g0,g2) = 114
    c: DistanceY(g1,g0) = 45
    c: Vertical(g3,g2)
    c: DistanceY(g-3,g3) = 17
    c: Vertical(g5,g2)
    c: Vertical(g4,g0)
    c: Horizontal(g4,g5)
    c: Equal(g4,g5)
    c: Equal(g5,g2)
    c: DistanceY(g0,g4) = 45
FEATURE [PartDesign::Pocket] Pocket003
  BaseFeature = -> Hole001
  ClaimChildren = false
  Fit = 0
  FitJoin = 0
  InnerFit = 0
  InnerFitJoin = 0
  InnerTaperAngle = 0
  InnerTaperAngleRev = 0
  Length = 5
  Length2 = 100
  Linearize = true
  NewSolid = false
  Placement = pos=(0,0,0) rot=(1,0,0;1.5708rad)
  Profile = -> Sketch012
  Refine = true
  Suppress = false
  Type = 1
  _ProfileBasedVersion = 0
FEATURE [Sketcher::SketchObject] Sketch013
  ExternalGeometry = -> [Pocket002]
  FullyConstrained = true
  MapMode = 5
  Placement = pos=(0,-15.7,-3.5e-15) rot=(1,0,0;1.5708rad)
  Support = -> [Pocket002]
  sketch-geometry (6):
    g0: Circle CenterX=-3 CenterY=-40.65 CenterZ=0 NormalX=0 NormalY=0 NormalZ=1 AngleXU=0 Radius=2.75
    g1: Circle CenterX=21 CenterY=-40.65 CenterZ=0 NormalX=0 NormalY=0 NormalZ=1 AngleXU=0 Radius=2.75
    g2: Circle CenterX=-3 CenterY=-80.65 CenterZ=0 NormalX=0 NormalY=0 NormalZ=1 AngleXU=0 Radius=2.75
    g3: Circle CenterX=21 CenterY=-80.65 CenterZ=0 NormalX=0 NormalY=0 NormalZ=1 AngleXU=0 Radius=2.75
    g4: GeomPoint [constr] X=33.25 Y=-60.65 Z=0
    g5: GeomPoint [constr] X=21 Y=-60.65 Z=0
  constraints (14):
    c: Equal(g0,g1)
    c: Equal(g1,g3)
    c: Equal(g3,g2)
    c: Vertical(g1,g3)
    c: Vertical(g0,g2)
    c: Horizontal(g2,g3)
    c: DistanceX(g0,g1) = 24
    c: DistanceY(g3,g1) = 40
    c: Horizontal(g4,g5)
    c: Symmetric(g1,g3,g5)
    c: Symmetric(g-4,g-3,g4)
    c: Diameter(g0) = 5.5
    c: DistanceX(g-1,g1) = 21
    c: Horizontal(g0,g1)
FEATURE [PartDesign::Hole] Hole004
  BaseFeature = -> Pocket002
  ClaimChildren = false
  CustomThreadClearance = 0
  Depth = 25
  DepthType = 1
  Diameter = 5.5
  DrillForDepth = false
  DrillPoint = 1
  DrillPointAngle = 118
  Fit = 0
  FitJoin = 0
  HoleCutCountersinkAngle = 90
  HoleCutCustomValues = false
  HoleCutDepth = 9
  HoleCutDiameter = 9.5
  HoleCutType = 1
  InnerFit = 0
  InnerFitJoin = 0
  ModelThread = false
  NewSolid = false
  Placement = pos=(0,0,0) rot=(1,0,0;1.5708rad)
  Profile = -> Sketch013
  Refine = true
  Suppress = false
  Tapered = false
  TaperedAngle = 90
  ThreadClass = 0
  ThreadDepth = 689.55
  ThreadDepthType = 0
  ThreadDirection = 0
  ThreadFit = 0
  ThreadSize = 0
  ThreadType = 0
  Threaded = false
  UseCustomThreadClearance = false
  _ProfileBasedVersion = 0
FEATURE [PartDesign::ShapeBinder] ShapeBinder004
  Support = -> [Pad003]
  TraceSupport = false
FEATURE [PartDesign::Pad] Pad005
  ClaimChildren = false
  Direction = (1,1,1)
  Fit = 0
  FitJoin = 0
  InnerFit = 0
  InnerFitJoin = 0
  InnerTaperAngle = 0
  InnerTaperAngleRev = 0
  Length = 16.75
  Length2 = 100
  Linearize = true
  NewSolid = false
  Profile = -> ShapeBinder004
  Refine = true
  Suppress = false
  Type = 0
  _ProfileBasedVersion = 0
FEATURE [PartDesign::Body] Body005  label="Nut-shim-X"
  AutoGroupSolids = false
  ExportMode = 0
  Group = -> [ShapeBinder004,Pad005]
  Origin = -> Origin005
  Placement = pos=(-129,0,54) rot=(0,0,1;0rad)
  Tip = -> Pad005
  _ExportChildren = -> [Pad005]
  _GroupVersion = 1
FEATURE [App::Link] Link005  label="Link005(Nut-shim-X)"
  AutoLinkLabel = true
  AutoPlacement = true
  LinkPlacement = pos=(-129,0,54) rot=(0,0,1;0rad)
  LinkedObject = -> Body005
  Placement = pos=(-129,0,54) rot=(0,0,1;0rad)
  SyncGroupVisibility = false
  _LinkVersion = 1
FEATURE [Part::FeaturePython] Parts005  # WARN: FeaturePython — macro-defined, semantics opaque (R4)
  Group = -> [Link005]
  GroupMode = 0
  _LinkVersion = 1
FEATURE [Part::FeaturePython] Screw  label="M5x16-Screw"  # Fasteners workbench fastener (typed FeaturePython)
  diameter = 6
  invert = false
  length = 4
  lengthCustom = 16
  matchOuter = false
  offset = 0
  thread = false
  type = 33
FEATURE [App::LinkElement] Link006_i0
  LinkPlacement = pos=(-69.25,29.3,25.2) rot=(1,0,0;1.5708rad)
  LinkedObject = -> Screw
  Placement = pos=(-69.25,29.3,25.2) rot=(1,0,0;1.5708rad)
  _LinkVersion = 1
FEATURE [App::LinkElement] Link006_i1
  LinkPlacement = pos=(-33.25,29.3,25.2) rot=(1,0,0;1.5708rad)
  LinkedObject = -> Screw
  Placement = pos=(-33.25,29.3,25.2) rot=(1,0,0;1.5708rad)
  _LinkVersion = 1
FEATURE [App::LinkElement] Link006_i2
  LinkPlacement = pos=(-69.25,29.3,-6.8) rot=(1,0,0;1.5708rad)
  LinkedObject = -> Screw
  Placement = pos=(-69.25,29.3,-6.8) rot=(1,0,0;1.5708rad)
  _LinkVersion = 1
FEATURE [App::LinkElement] Link006_i3
  LinkPlacement = pos=(33.25,29.3,25.2) rot=(1,0,0;1.5708rad)
  LinkedObject = -> Screw
  Placement = pos=(33.25,29.3,25.2) rot=(1,0,0;1.5708rad)
  _LinkVersion = 1
FEATURE [App::LinkElement] Link006_i4
  LinkPlacement = pos=(69.25,29.3,-6.8) rot=(1,0,0;1.5708rad)
  LinkedObject = -> Screw
  Placement = pos=(69.25,29.3,-6.8) rot=(1,0,0;1.5708rad)
  _LinkVersion = 1
FEATURE [App::LinkElement] Link006_i5
  LinkPlacement = pos=(33.25,29.3,-114.5) rot=(1,0,0;1.5708rad)
  LinkedObject = -> Screw
  Placement = pos=(33.25,29.3,-114.5) rot=(1,0,0;1.5708rad)
  _LinkVersion = 1
FEATURE [App::LinkElement] Link006_i6
  LinkPlacement = pos=(-33.25,29.3,-114.5) rot=(1,0,0;1.5708rad)
  LinkedObject = -> Screw
  Placement = pos=(-33.25,29.3,-114.5) rot=(1,0,0;1.5708rad)
  _LinkVersion = 1
FEATURE [App::LinkElement] Link006_i7
  LinkPlacement = pos=(-69.25,29.3,-114.5) rot=(1,0,0;1.5708rad)
  LinkedObject = -> Screw
  Placement = pos=(-69.25,29.3,-114.5) rot=(1,0,0;1.5708rad)
  _LinkVersion = 1
FEATURE [App::LinkElement] Link006_i8
  LinkPlacement = pos=(33.25,29.3,-146.5) rot=(1,0,0;1.5708rad)
  LinkedObject = -> Screw
  Placement = pos=(33.25,29.3,-146.5) rot=(1,0,0;1.5708rad)
  _LinkVersion = 1
FEATURE [App::LinkElement] Link006_i9
  LinkPlacement = pos=(-33.25,29.3,-146.5) rot=(1,0,0;1.5708rad)
  LinkedObject = -> Screw
  Placement = pos=(-33.25,29.3,-146.5) rot=(1,0,0;1.5708rad)
  _LinkVersion = 1
FEATURE [App::LinkElement] Link006_i10
  LinkPlacement = pos=(-69.25,29.3,-146.5) rot=(1,0,0;1.5708rad)
  LinkedObject = -> Screw
  Placement = pos=(-69.25,29.3,-146.5) rot=(1,0,0;1.5708rad)
  _LinkVersion = 1
FEATURE [App::LinkElement] Link006_i11
  LinkPlacement = pos=(-33.25,29.3,-6.8) rot=(1,0,0;1.5708rad)
  LinkedObject = -> Screw
  Placement = pos=(-33.25,29.3,-6.8) rot=(1,0,0;1.5708rad)
  _LinkVersion = 1
FEATURE [App::LinkElement] Link006_i12
  LinkPlacement = pos=(69.25,29.3,25.2) rot=(1,0,0;1.5708rad)
  LinkedObject = -> Screw
  Placement = pos=(69.25,29.3,25.2) rot=(1,0,0;1.5708rad)
  _LinkVersion = 1
FEATURE [App::LinkElement] Link006_i13
  LinkPlacement = pos=(33.25,29.3,-6.8) rot=(1,0,0;1.5708rad)
  LinkedObject = -> Screw
  Placement = pos=(33.25,29.3,-6.8) rot=(1,0,0;1.5708rad)
  _LinkVersion = 1
FEATURE [App::LinkElement] Link006_i14
  LinkPlacement = pos=(69.25,29.3,-114.5) rot=(1,0,0;1.5708rad)
  LinkedObject = -> Screw
  Placement = pos=(69.25,29.3,-114.5) rot=(1,0,0;1.5708rad)
  _LinkVersion = 1
FEATURE [App::LinkElement] Link006_i15
  LinkPlacement = pos=(69.25,29.3,-146.5) rot=(1,0,0;1.5708rad)
  LinkedObject = -> Screw
  Placement = pos=(69.25,29.3,-146.5) rot=(1,0,0;1.5708rad)
  _LinkVersion = 1
FEATURE [App::Link] Link006  label="M5x16-Screw 16ct"
  AutoLinkLabel = true
  AutoPlacement = true
  ElementCount = 16
  ElementList = -> [Link006_i0,Link006_i1,Link006_i2,Link006_i3,Link006_i4,Link006_i5,Link006_i6,Link006_i7,Link006_i8,Link006_i9,Link006_i10,Link006_i11,Link006_i12,Link006_i13,Link006_i14,Link006_i15]
  LinkPlacement = pos=(0,-39,0) rot=(0,0,1;0rad)
  LinkedObject = -> Screw
  Placement = pos=(0,-39,0) rot=(0,0,1;0rad)
  SyncGroupVisibility = false
  _LinkVersion = 1
FEATURE [Part::FeaturePython] Screw001  label="M5x30-Screw"  # Fasteners workbench fastener (typed FeaturePython)
  diameter = 6
  invert = false
  length = 7
  lengthCustom = 30
  matchOuter = false
  offset = 0
  thread = false
  type = 33
FEATURE [App::LinkElement] Link007_i0
  LinkPlacement = pos=(-3,44.3,-40.65) rot=(1,0,0;1.5708rad)
  LinkedObject = -> Screw001
  Placement = pos=(-3,44.3,-40.65) rot=(1,0,0;1.5708rad)
  _LinkVersion = 1
FEATURE [App::LinkElement] Link007_i1
  LinkPlacement = pos=(21,44.3,-40.65) rot=(1,0,0;1.5708rad)
  LinkedObject = -> Screw001
  Placement = pos=(21,44.3,-40.65) rot=(1,0,0;1.5708rad)
  _LinkVersion = 1
FEATURE [App::LinkElement] Link007_i2
  LinkPlacement = pos=(-3,44.3,-80.65) rot=(1,0,0;1.5708rad)
  LinkedObject = -> Screw001
  Placement = pos=(-3,44.3,-80.65) rot=(1,0,0;1.5708rad)
  _LinkVersion = 1
FEATURE [App::LinkElement] Link007_i3
  LinkPlacement = pos=(21,44.3,-80.65) rot=(1,0,0;1.5708rad)
  LinkedObject = -> Screw001
  Placement = pos=(21,44.3,-80.65) rot=(1,0,0;1.5708rad)
  _LinkVersion = 1
FEATURE [App::Link] Link007  label="M5x30-Screw 4ct"
  AutoLinkLabel = true
  AutoPlacement = true
  ElementCount = 4
  ElementList = -> [Link007_i0,Link007_i1,Link007_i2,Link007_i3]
  LinkPlacement = pos=(0,-51,0) rot=(0,0,1;0rad)
  LinkedObject = -> Screw001
  Placement = pos=(0,-51,0) rot=(0,0,1;0rad)
  SyncGroupVisibility = false
  _LinkVersion = 1
FEATURE [Part::FeaturePython] Screw002  label="M5x20-Screw"  # Fasteners workbench fastener (typed FeaturePython)
  diameter = 6
  invert = false
  length = 5
  lengthCustom = 20
  matchOuter = false
  offset = 0
  thread = false
  type = 33
FEATURE [App::LinkElement] Link008_i0
  LinkPlacement = pos=(-60,-7.84998,-46.15) rot=(0,0,1;3.14159rad)
  LinkedObject = -> Screw002
  Placement = pos=(-60,-7.84998,-46.15) rot=(0,0,1;3.14159rad)
  _LinkVersion = 1
FEATURE [App::LinkElement] Link008_i1
  LinkPlacement = pos=(-20,-7.84998,-46.15) rot=(0,0,1;3.14159rad)
  LinkedObject = -> Screw002
  Placement = pos=(-20,-7.84998,-46.15) rot=(0,0,1;3.14159rad)
  _LinkVersion = 1
FEATURE [App::LinkElement] Link008_i2
  LinkPlacement = pos=(20,-7.84998,-46.15) rot=(0,0,1;3.14159rad)
  LinkedObject = -> Screw002
  Placement = pos=(20,-7.84998,-46.15) rot=(0,0,1;3.14159rad)
  _LinkVersion = 1
FEATURE [App::LinkElement] Link008_i3
  LinkPlacement = pos=(60,-7.84998,-46.15) rot=(0,0,1;3.14159rad)
  LinkedObject = -> Screw002
  Placement = pos=(60,-7.84998,-46.15) rot=(0,0,1;3.14159rad)
  _LinkVersion = 1
FEATURE [App::Link] Link008  label="M5x20-Screw 4ct"
  AutoLinkLabel = true
  AutoPlacement = true
  ElementCount = 4
  ElementList = -> [Link008_i0,Link008_i1,Link008_i2,Link008_i3]
  LinkPlacement = pos=(0,-2.44379e-05,205) rot=(0,0,1;0rad)
  LinkedObject = -> Screw002
  Placement = pos=(0,-2.44379e-05,205) rot=(0,0,1;0rad)
  SyncGroupVisibility = false
  _LinkVersion = 1
FEATURE [Part::FeaturePython] Parts004  # WARN: FeaturePython — macro-defined, semantics opaque (R4)
  Group = -> [Link004,Link008]
  GroupMode = 0
  _LinkVersion = 1
FEATURE [App::LinkElement] Link009_i0
  LinkPlacement = pos=(18,39.65,58.5) rot=(1,0,0;1.5708rad)
  LinkedObject = -> Screw001
  Placement = pos=(18,39.65,58.5) rot=(1,0,0;1.5708rad)
  _LinkVersion = 1
FEATURE [App::LinkElement] Link009_i1
  LinkPlacement = pos=(18,39.65,22.5) rot=(1,0,0;1.5708rad)
  LinkedObject = -> Screw001
  Placement = pos=(18,39.65,22.5) rot=(1,0,0;1.5708rad)
  _LinkVersion = 1
FEATURE [App::LinkElement] Link009_i2
  LinkPlacement = pos=(50,39.65,22.5) rot=(1,0,0;1.5708rad)
  LinkedObject = -> Screw001
  Placement = pos=(50,39.65,22.5) rot=(1,0,0;1.5708rad)
  _LinkVersion = 1
FEATURE [App::LinkElement] Link009_i3
  LinkPlacement = pos=(18,39.65,-58.5) rot=(1,0,0;1.5708rad)
  LinkedObject = -> Screw001
  Placement = pos=(18,39.65,-58.5) rot=(1,0,0;1.5708rad)
  _LinkVersion = 1
FEATURE [App::LinkElement] Link009_i4
  LinkPlacement = pos=(50,39.65,-22.5) rot=(1,0,0;1.5708rad)
  LinkedObject = -> Screw001
  Placement = pos=(50,39.65,-22.5) rot=(1,0,0;1.5708rad)
  _LinkVersion = 1
FEATURE [App::LinkElement] Link009_i5
  LinkPlacement = pos=(158,39.65,-58.5) rot=(1,0,0;1.5708rad)
  LinkedObject = -> Screw001
  Placement = pos=(158,39.65,-58.5) rot=(1,0,0;1.5708rad)
  _LinkVersion = 1
FEATURE [App::LinkElement] Link009_i6
  LinkPlacement = pos=(126,39.65,-58.5) rot=(1,0,0;1.5708rad)
  LinkedObject = -> Screw001
  Placement = pos=(126,39.65,-58.5) rot=(1,0,0;1.5708rad)
  _LinkVersion = 1
FEATURE [App::LinkElement] Link009_i7
  LinkPlacement = pos=(158,39.65,-22.5) rot=(1,0,0;1.5708rad)
  LinkedObject = -> Screw001
  Placement = pos=(158,39.65,-22.5) rot=(1,0,0;1.5708rad)
  _LinkVersion = 1
FEATURE [App::LinkElement] Link009_i8
  LinkPlacement = pos=(126,39.65,-22.5) rot=(1,0,0;1.5708rad)
  LinkedObject = -> Screw001
  Placement = pos=(126,39.65,-22.5) rot=(1,0,0;1.5708rad)
  _LinkVersion = 1
FEATURE [App::LinkElement] Link009_i9
  LinkPlacement = pos=(126,39.65,22.5) rot=(1,0,0;1.5708rad)
  LinkedObject = -> Screw001
  Placement = pos=(126,39.65,22.5) rot=(1,0,0;1.5708rad)
  _LinkVersion = 1
FEATURE [App::LinkElement] Link009_i10
  LinkPlacement = pos=(158,39.65,22.5) rot=(1,0,0;1.5708rad)
  LinkedObject = -> Screw001
  Placement = pos=(158,39.65,22.5) rot=(1,0,0;1.5708rad)
  _LinkVersion = 1
FEATURE [App::LinkElement] Link009_i11
  LinkPlacement = pos=(50,39.65,58.5) rot=(1,0,0;1.5708rad)
  LinkedObject = -> Screw001
  Placement = pos=(50,39.65,58.5) rot=(1,0,0;1.5708rad)
  _LinkVersion = 1
FEATURE [App::LinkElement] Link009_i12
  LinkPlacement = pos=(18,39.65,-22.5) rot=(1,0,0;1.5708rad)
  LinkedObject = -> Screw001
  Placement = pos=(18,39.65,-22.5) rot=(1,0,0;1.5708rad)
  _LinkVersion = 1
FEATURE [App::LinkElement] Link009_i13
  LinkPlacement = pos=(50,39.65,-58.5) rot=(1,0,0;1.5708rad)
  LinkedObject = -> Screw001
  Placement = pos=(50,39.65,-58.5) rot=(1,0,0;1.5708rad)
  _LinkVersion = 1
FEATURE [App::LinkElement] Link009_i14
  LinkPlacement = pos=(158,39.65,58.5) rot=(1,0,0;1.5708rad)
  LinkedObject = -> Screw001
  Placement = pos=(158,39.65,58.5) rot=(1,0,0;1.5708rad)
  _LinkVersion = 1
FEATURE [App::LinkElement] Link009_i15
  LinkPlacement = pos=(126,39.65,58.5) rot=(1,0,0;1.5708rad)
  LinkedObject = -> Screw001
  Placement = pos=(126,39.65,58.5) rot=(1,0,0;1.5708rad)
  _LinkVersion = 1
FEATURE [App::Link] Link009  label="M5x30-Screw 16ct"
  AutoLinkLabel = true
  AutoPlacement = true
  ElementCount = 16
  ElementList = -> [Link009_i0,Link009_i1,Link009_i2,Link009_i3,Link009_i4,Link009_i5,Link009_i6,Link009_i7,Link009_i8,Link009_i9,Link009_i10,Link009_i11,Link009_i12,Link009_i13,Link009_i14,Link009_i15]
  LinkPlacement = pos=(0,-112,0) rot=(0,0,1;0rad)
  LinkedObject = -> Screw001
  Placement = pos=(0,-112,0) rot=(0,0,1;0rad)
  SyncGroupVisibility = false
  _LinkVersion = 1
FEATURE [App::LinkElement] Link010_i0
  LinkPlacement = pos=(9.99999,27.15,-15.525) rot=(1,0,0;1.5708rad)
  LinkedObject = -> Screw
  Placement = pos=(9.99999,27.15,-15.525) rot=(1,0,0;1.5708rad)
  _LinkVersion = 1
FEATURE [App::LinkElement] Link010_i1
  LinkPlacement = pos=(50,27.15,-15.525) rot=(1,0,0;1.5708rad)
  LinkedObject = -> Screw
  Placement = pos=(50,27.15,-15.525) rot=(1,0,0;1.5708rad)
  _LinkVersion = 1
FEATURE [App::LinkElement] Link010_i2
  LinkPlacement = pos=(9.99999,27.15,-39.525) rot=(1,0,0;1.5708rad)
  LinkedObject = -> Screw
  Placement = pos=(9.99999,27.15,-39.525) rot=(1,0,0;1.5708rad)
  _LinkVersion = 1
FEATURE [App::LinkElement] Link010_i3
  LinkPlacement = pos=(50,27.15,-39.525) rot=(1,0,0;1.5708rad)
  LinkedObject = -> Screw
  Placement = pos=(50,27.15,-39.525) rot=(1,0,0;1.5708rad)
  _LinkVersion = 1
FEATURE [App::Link] Link010  label="M5x16-Screw 4ct "
  AutoLinkLabel = true
  AutoPlacement = true
  ElementCount = 4
  ElementList = -> [Link010_i0,Link010_i1,Link010_i2,Link010_i3]
  LinkPlacement = pos=(58,-101,0) rot=(0,0,1;0rad)
  LinkedObject = -> Screw
  Placement = pos=(58,-101,0) rot=(0,0,1;0rad)
  SyncGroupVisibility = false
  _LinkVersion = 1
FEATURE [Sketcher::SketchObject] Sketch014
  ExternalGeometry = -> [Hole004]
  FullyConstrained = true
  MapMode = 5
  Placement = pos=(-76.25,0,0) rot=(0.707107,0,-0.707107;3.14159rad)
  Support = -> [Hole004]
  sketch-geometry (3):
    g0: Circle CenterX=26.5 CenterY=7.85 CenterZ=0 NormalX=0 NormalY=0 NormalZ=1 AngleXU=0 Radius=2.5
    g1: GeomPoint [constr] X=26.5 Y=15.7 Z=0
    g2: GeomPoint [constr] X=26.5 Y=0 Z=0
  constraints (6):
    c: PointOnObject(g1,g-3)
    c: PointOnObject(g2,g-1)
    c: Vertical(g1,g0)
    c: DistanceX(g-3,g1) = 179
    c: Symmetric(g1,g2,g0)
    c: Diameter(g0) = 5
FEATURE [PartDesign::Pocket] Pocket004
  BaseFeature = -> Hole004
  ClaimChildren = false
  Fit = 0
  FitJoin = 0
  InnerFit = 0
  InnerFitJoin = 0
  InnerTaperAngle = 0
  InnerTaperAngleRev = 0
  Length = 30
  Length2 = 100
  Linearize = true
  NewSolid = false
  Placement = pos=(0,0,0) rot=(1,0,0;1.5708rad)
  Profile = -> Sketch014
  Refine = true
  Suppress = false
  Type = 0
  _ProfileBasedVersion = 1
FEATURE [PartDesign::Body] Body  label="Backplate"
  AutoGroupSolids = false
  ExportMode = 0
  Group = -> [Sketch,Pad,Sketch001,Pocket,Mirrored,Sketch002,Pocket001,Sketch009,Hole003,Sketch011,Pocket002,Sketch013,Hole004,Sketch014,Pocket004]
  Origin = -> Origin
  Tip = -> Pocket004
  _ExportChildren = -> [Pad,Pocket,Mirrored,Pocket001,Hole003,Pocket002,Hole004,Pocket004]
  _GroupVersion = 1
FEATURE [Part::FeaturePython] Screw003  label="1/4inx1in-Screw"  # Fasteners workbench fastener (typed FeaturePython)
  diameter = 1
  invert = false
  length = 2
  lengthCustom = 25.4
  matchOuter = false
  offset = 0
  thread = false
  type = 0
FEATURE [Part::FeaturePython] Nut  label="1/4in-Nut"  # Fasteners workbench fastener (typed FeaturePython)
  diameter = 11
  invert = false
  matchOuter = false
  offset = 0
  thread = false
  type = 0
FEATURE [App::Link] Link011  label="Link011(1/4inx1in-Screw)"
  AutoLinkLabel = true
  AutoPlacement = true
  LinkPlacement = pos=(-81.65,-7.85,-26.5) rot=(0.707107,0,-0.707107;3.14159rad)
  LinkedObject = -> Screw003
  Placement = pos=(-81.65,-7.85,-26.5) rot=(0.707107,0,-0.707107;3.14159rad)
  SyncGroupVisibility = false
  _LinkVersion = 1
FEATURE [App::Link] Link012  label="Link012(1/4in-Nut)"
  AutoLinkLabel = true
  AutoPlacement = true
  LinkPlacement = pos=(-76.25,-7.85,-26.5) rot=(0.707107,0,-0.707107;3.14159rad)
  LinkedObject = -> Nut
  Placement = pos=(-76.25,-7.85,-26.5) rot=(0.707107,0,-0.707107;3.14159rad)
  SyncGroupVisibility = false
  _LinkVersion = 1
FEATURE [Part::FeaturePython] Parts  # WARN: FeaturePython — macro-defined, semantics opaque (R4)
  Group = -> [Link,Link006,Link007,Link011,Link012]
  GroupMode = 0
  _LinkVersion = 1
FEATURE [Sketcher::SketchObject] Sketch015
  FullyConstrained = true
  MapMode = 5
  Placement = pos=(0,-5.49e-14,152.5) rot=(1,0,0;3.14159rad)
  Support = -> [Pad004]
  sketch-geometry (5):
    g0: LineSegment [constr] StartX=-60 StartY=51.35 StartZ=0 EndX=-54 EndY=37.35 EndZ=0
    g1: LineSegment [constr] StartX=-54 StartY=37.35 StartZ=0 EndX=-48 EndY=51.35 EndZ=0
    g2: Circle CenterX=-48 CenterY=51.35 CenterZ=0 NormalX=0 NormalY=0 NormalZ=1 AngleXU=0 Radius=1.25
    g3: Circle CenterX=-60 CenterY=51.35 CenterZ=0 NormalX=0 NormalY=0 NormalZ=1 AngleXU=0 Radius=1.25
    g4: Circle CenterX=-54 CenterY=37.35 CenterZ=0 NormalX=0 NormalY=0 NormalZ=1 AngleXU=0 Radius=2.75
  constraints (13):
    c: Coincident(g1,g0)
    c: Equal(g1,g0)
    c: Coincident(g2,g1)
    c: Coincident(g3,g0)
    c: Coincident(g4,g0)
    c: Equal(g3,g2)
    c: Horizontal(g3,g2)
    c: Diameter(g3) = 2.5
    c: Diameter(g4) = 5.5
    c: DistanceX(g3,g2) = 12
    c: DistanceY(g4,g2) = 14
    c: DistanceX(g4,g-1) = 54
    c: DistanceY(g-1,g2) = 51.35
FEATURE [PartDesign::Pocket] Pocket005
  BaseFeature = -> Pad004
  ClaimChildren = false
  Fit = 0
  FitJoin = 0
  InnerFit = 0
  InnerFitJoin = 0
  InnerTaperAngle = 0
  InnerTaperAngleRev = 0
  Length = 5
  Length2 = 100
  Linearize = true
  NewSolid = false
  Placement = pos=(0,0,0) rot=(1,0,0;1.5708rad)
  Profile = -> Sketch015
  Refine = true
  Suppress = false
  Type = 1
  _ProfileBasedVersion = 1
FEATURE [PartDesign::Body] Body004  label="Motor-bracket"
  AutoGroupSolids = false
  ExportMode = 0
  Group = -> [Sketch010,Pad004,ShapeBinder003,Sketch015,Pocket005]
  Origin = -> Origin004
  Tip = -> Pocket005
  _ExportChildren = -> [Pad004,ShapeBinder003,Pocket005]
  _GroupVersion = 1
FEATURE [Sketcher::SketchObject] Sketch016
  FullyConstrained = true
  MapMode = 5
  Placement = pos=(0,0,66) rot=(0,0,1;3.14159rad)
  Support = -> [Pocket003]
  sketch-geometry (1):
    g0: Circle CenterX=54 CenterY=-0.4 CenterZ=0 NormalX=0 NormalY=0 NormalZ=1 AngleXU=0 Radius=2.5
  constraints (3):
    c: Diameter(g0) = 5
    c: DistanceX(g-1,g0) = 54
    c: DistanceY(g0,g-1) = 0.4
FEATURE [PartDesign::Pocket] Pocket006
  BaseFeature = -> Pocket003
  ClaimChildren = false
  Fit = 0
  FitJoin = 0
  InnerFit = 0
  InnerFitJoin = 0
  InnerTaperAngle = 0
  InnerTaperAngleRev = 0
  Length = 25
  Length2 = 100
  Linearize = true
  NewSolid = false
  Placement = pos=(0,0,0) rot=(1,0,0;1.5708rad)
  Profile = -> Sketch016
  Refine = true
  Suppress = false
  Type = 0
  _ProfileBasedVersion = 1
FEATURE [PartDesign::Body] Body001  label="Frontplate"
  AutoGroupSolids = false
  ExportMode = 0
  Group = -> [ShapeBinder,Sketch003,Pad001,Sketch004,Hole,Sketch005,Hole001,Sketch012,Pocket003,Sketch016,Pocket006]
  Origin = -> Origin001
  Placement = pos=(88,-72,0) rot=(0,0,1;0rad)
  Tip = -> Pocket006
  _ExportChildren = -> [ShapeBinder,Pad001,Hole,Hole001,Pocket003,Pocket006]
  _GroupVersion = 1
FEATURE [Part::FeaturePython] Washer  label="1/4in-Washer"  # Fasteners workbench fastener (typed FeaturePython)
  diameter = 11
  invert = false
  matchOuter = false
  offset = 0
  type = 0
FEATURE [App::DocumentObjectGroup] Group  label="Components"
  ExportMode = 1
  Group = -> [Body,Body001,Body002,Body003,Body004,Body005,Screw,Screw001,Screw002,Screw003,Nut,Washer]
  _GroupVersion = 1
FEATURE [App::Link] Link013  label="1/4in-Washer "
  AutoLinkLabel = true
  AutoPlacement = true
  LinkPlacement = pos=(34,-71.6,66) rot=(0,0,1;3.14159rad)
  LinkedObject = -> Washer
  Placement = pos=(34,-71.6,66) rot=(0,0,1;3.14159rad)
  SyncGroupVisibility = false
  _LinkVersion = 1
FEATURE [App::Link] Link014  label="1/4inx1in-Screw "
  AutoLinkLabel = true
  AutoPlacement = true
  LinkPlacement = pos=(34,-71.6,81.4) rot=(0,0,1;3.14159rad)
  LinkedObject = -> Screw003
  Placement = pos=(34,-71.6,81.4) rot=(0,0,1;3.14159rad)
  SyncGroupVisibility = false
  _LinkVersion = 1
FEATURE [App::Link] Link015  label="1/4in-Nut "
  AutoLinkLabel = true
  AutoPlacement = true
  LinkPlacement = pos=(34,-71.6,67.6002) rot=(0,0,1;3.14159rad)
  LinkedObject = -> Nut
  Placement = pos=(34,-71.6,67.6002) rot=(0,0,1;3.14159rad)
  SyncGroupVisibility = false
  _LinkVersion = 1
FEATURE [Part::FeaturePython] Parts001  # WARN: FeaturePython — macro-defined, semantics opaque (R4)
  Group = -> [Link002,Link009,Link010,Link014,Link013,Link015]
  GroupMode = 0
  _LinkVersion = 1
FEATURE [TechDraw::DrawSVGTemplate] Template
  EditableTexts = DrawingTitle1=Z axis motor bracket; DrawingTitle2=Count: 1; DrawingTitle3=Maerial: 1/4" Aluminum; DrawnBy=Andrew <owner>; Revision=V.1.0; Scale=Scale 1:1; Sheet=Sheet 1 of 1
  Height = 215.9
  Orientation = 1
  Width = 279.4
FEATURE [TechDraw::DrawViewPart] View  label="Motor bracket Top"
  CoarseView = false
  Direction = (0,0,1)
  Focus = 100
  HardHidden = false
  IsoCount = 0
  IsoHidden = false
  IsoVisible = false
  LockPosition = false
  Perspective = false
  Rotation = 0
  ScaleType = 0
  SeamHidden = false
  SeamVisible = true
  SmoothHidden = false
  SmoothVisible = true
  Source = -> [Body004]
  X = 142.851
  XDirection = (1,0,0)
  Y = 132.61
FEATURE [TechDraw::DrawViewDimension] Dimension
  Arbitrary = false
  ArbitraryTolerances = false
  EqualTolerance = true
  FormatSpec = ⌀%.2f
  FormatSpecOverTolerance = %+.2f
  FormatSpecUnderTolerance = %+.2f
  Inverted = false
  LockPosition = false
  MeasureType = 1
  OverTolerance = 0
  References2D = -> [View]
  Rotation = 0
  ScaleType = 0
  TheoreticalExact = false
  Type = 5
  UnderTolerance = 0
  X = -8.48904
  Y = -1.17013
FEATURE [TechDraw::DrawViewDimension] Dimension002
  Arbitrary = false
  ArbitraryTolerances = false
  EqualTolerance = true
  FormatSpec = %.2f
  FormatSpecOverTolerance = %+.2f
  FormatSpecUnderTolerance = %+.2f
  Inverted = false
  LockPosition = false
  MeasureType = 1
  OverTolerance = 0
  References2D = -> [View]
  Rotation = 0
  ScaleType = 0
  TheoreticalExact = false
  Type = 1
  UnderTolerance = 0
  X = 0.775865
  Y = 61.4694
FEATURE [TechDraw::DrawViewDimension] Dimension003
  Arbitrary = false
  ArbitraryTolerances = false
  EqualTolerance = true
  FormatSpec = %.2f
  FormatSpecOverTolerance = %+.2f
  FormatSpecUnderTolerance = %+.2f
  Inverted = false
  LockPosition = false
  MeasureType = 1
  OverTolerance = 0
  References2D = -> [View]
  Rotation = 0
  ScaleType = 0
  TheoreticalExact = false
  Type = 2
  UnderTolerance = 0
  X = -98.2391
  Y = 0.0602093
FEATURE [TechDraw::DrawViewDimension] Dimension004
  Arbitrary = false
  ArbitraryTolerances = false
  EqualTolerance = true
  FormatSpec = %.2f
  FormatSpecOverTolerance = %+.2f
  FormatSpecUnderTolerance = %+.2f
  Inverted = false
  LockPosition = false
  MeasureType = 1
  OverTolerance = 0
  References2D = -> [View]
  Rotation = 0
  ScaleType = 0
  TheoreticalExact = false
  Type = 1
  UnderTolerance = 0
  X = -67.2513
  Y = 50.8762
FEATURE [TechDraw::DrawViewDimension] Dimension005
  Arbitrary = false
  ArbitraryTolerances = false
  EqualTolerance = true
  FormatSpec = %.2f
  FormatSpecOverTolerance = %+.2f
  FormatSpecUnderTolerance = %+.2f
  Inverted = false
  LockPosition = false
  MeasureType = 1
  OverTolerance = 0
  References2D = -> [View]
  Rotation = 0
  ScaleType = 0
  TheoreticalExact = false
  Type = 1
  UnderTolerance = 0
  X = -40.3495
  Y = 50.7956
FEATURE [TechDraw::DrawViewDimension] Dimension006
  Arbitrary = false
  ArbitraryTolerances = false
  EqualTolerance = true
  FormatSpec = %.2f
  FormatSpecOverTolerance = %+.2f
  FormatSpecUnderTolerance = %+.2f
  Inverted = false
  LockPosition = false
  MeasureType = 1
  OverTolerance = 0
  References2D = -> [View]
  Rotation = 0
  ScaleType = 0
  TheoreticalExact = false
  Type = 1
  UnderTolerance = 0
  X = -3.49488
  Y = 50.7956
FEATURE [TechDraw::DrawViewDimension] Dimension007
  Arbitrary = false
  ArbitraryTolerances = false
  EqualTolerance = true
  FormatSpec = %.2f
  FormatSpecOverTolerance = %+.2f
  FormatSpecUnderTolerance = %+.2f
  Inverted = false
  LockPosition = false
  MeasureType = 1
  OverTolerance = 0
  References2D = -> [View]
  Rotation = 0
  ScaleType = 0
  TheoreticalExact = false
  Type = 1
  UnderTolerance = 0
  X = 38.0099
  Y = 50.7422
FEATURE [TechDraw::DrawViewDimension] Dimension008
  Arbitrary = false
  ArbitraryTolerances = false
  EqualTolerance = true
  FormatSpec = %.2f
  FormatSpecOverTolerance = %+.2f
  FormatSpecUnderTolerance = %+.2f
  Inverted = false
  LockPosition = false
  MeasureType = 1
  OverTolerance = 0
  References2D = -> [View]
  Rotation = 0
  ScaleType = 0
  TheoreticalExact = false
  Type = 1
  UnderTolerance = 0
  X = 0
  Y = -25.7
FEATURE [TechDraw::DrawViewDimension] Dimension010
  Arbitrary = false
  ArbitraryTolerances = false
  EqualTolerance = true
  FormatSpec = %.2f
  FormatSpecOverTolerance = %+.2f
  FormatSpecUnderTolerance = %+.2f
  Inverted = false
  LockPosition = false
  MeasureType = 1
  OverTolerance = 0
  References2D = -> [View]
  Rotation = 0
  ScaleType = 0
  TheoreticalExact = false
  Type = 2
  UnderTolerance = 0
  X = 35.1544
  Y = -29.6171
FEATURE [TechDraw::DrawViewDimension] Dimension011
  Arbitrary = false
  ArbitraryTolerances = false
  EqualTolerance = true
  FormatSpec = %.2f
  FormatSpecOverTolerance = %+.2f
  FormatSpecUnderTolerance = %+.2f
  Inverted = false
  LockPosition = false
  MeasureType = 1
  OverTolerance = 0
  References2D = -> [View]
  Rotation = 0
  ScaleType = 0
  TheoreticalExact = false
  Type = 2
  UnderTolerance = 0
  X = -31.9726
  Y = -1.38431
FEATURE [TechDraw::DrawViewDimension] Dimension012
  Arbitrary = false
  ArbitraryTolerances = false
  EqualTolerance = true
  FormatSpec = %.2f
  FormatSpecOverTolerance = %+.2f
  FormatSpecUnderTolerance = %+.2f
  Inverted = false
  LockPosition = false
  MeasureType = 1
  OverTolerance = 0
  References2D = -> [View]
  Rotation = 0
  ScaleType = 0
  TheoreticalExact = false
  Type = 1
  UnderTolerance = 0
  X = 44.5402
  Y = -6.8572
FEATURE [TechDraw::DrawViewDimension] Dimension013
  Arbitrary = false
  ArbitraryTolerances = false
  EqualTolerance = true
  FormatSpec = %.2f
  FormatSpecOverTolerance = %+.2f
  FormatSpecUnderTolerance = %+.2f
  Inverted = false
  LockPosition = false
  MeasureType = 1
  OverTolerance = 0
  References2D = -> [View]
  Rotation = 0
  ScaleType = 0
  TheoreticalExact = false
  Type = 1
  UnderTolerance = 0
  X = 7.37228
  Y = 31.4472
FEATURE [TechDraw::DrawViewDimension] Dimension014
  Arbitrary = false
  ArbitraryTolerances = false
  EqualTolerance = true
  FormatSpec = %.2f
  FormatSpecOverTolerance = %+.2f
  FormatSpecUnderTolerance = %+.2f
  Inverted = false
  LockPosition = false
  MeasureType = 1
  OverTolerance = 0
  References2D = -> [View]
  Rotation = 0
  ScaleType = 0
  TheoreticalExact = false
  Type = 2
  UnderTolerance = 0
  X = 25.1746
  Y = 9.81642
FEATURE [TechDraw::DrawViewDimension] Dimension015
  Arbitrary = false
  ArbitraryTolerances = false
  EqualTolerance = true
  FormatSpec = %.2f
  FormatSpecOverTolerance = %+.2f
  FormatSpecUnderTolerance = %+.2f
  Inverted = false
  LockPosition = false
  MeasureType = 1
  OverTolerance = 0
  References2D = -> [View]
  Rotation = 0
  ScaleType = 0
  TheoreticalExact = false
  Type = 1
  UnderTolerance = 0
  X = -53.8086
  Y = -15.8628
FEATURE [TechDraw::DrawViewDimension] Dimension016
  Arbitrary = false
  ArbitraryTolerances = false
  EqualTolerance = true
  FormatSpec = %.2f
  FormatSpecOverTolerance = %+.2f
  FormatSpecUnderTolerance = %+.2f
  Inverted = false
  LockPosition = false
  MeasureType = 1
  OverTolerance = 0
  References2D = -> [View]
  Rotation = 0
  ScaleType = 0
  TheoreticalExact = false
  Type = 2
  UnderTolerance = 0
  X = -68.125
  Y = -25.675
FEATURE [TechDraw::DrawViewDimension] Dimension017
  Arbitrary = false
  ArbitraryTolerances = false
  EqualTolerance = true
  FormatSpec = %.2f
  FormatSpecOverTolerance = %+.2f
  FormatSpecUnderTolerance = %+.2f
  Inverted = false
  LockPosition = false
  MeasureType = 1
  OverTolerance = 0
  References2D = -> [View]
  Rotation = 0
  ScaleType = 0
  TheoreticalExact = false
  Type = 2
  UnderTolerance = 0
  X = -70.3996
  Y = -4.0772
FEATURE [TechDraw::DrawViewDimension] Dimension018
  Arbitrary = false
  ArbitraryTolerances = false
  EqualTolerance = true
  FormatSpec = %.2f
  FormatSpecOverTolerance = %+.2f
  FormatSpecUnderTolerance = %+.2f
  Inverted = false
  LockPosition = false
  MeasureType = 1
  OverTolerance = 0
  References2D = -> [View]
  Rotation = 0
  ScaleType = 0
  TheoreticalExact = false
  Type = 1
  UnderTolerance = 0
  X = -46.6632
  Y = -1.20585
FEATURE [TechDraw::DrawViewDimension] Dimension019
  Arbitrary = false
  ArbitraryTolerances = false
  EqualTolerance = true
  FormatSpec = %.2f
  FormatSpecOverTolerance = %+.2f
  FormatSpecUnderTolerance = %+.2f
  Inverted = false
  LockPosition = false
  MeasureType = 1
  OverTolerance = 0
  References2D = -> [View]
  Rotation = 0
  ScaleType = 0
  TheoreticalExact = false
  Type = 2
  UnderTolerance = 0
  X = -87.4587
  Y = 21.6083
FEATURE [TechDraw::DrawViewDimension] Dimension020
  Arbitrary = false
  ArbitraryTolerances = false
  EqualTolerance = true
  FormatSpec = 4x ⌀%.2f
  FormatSpecOverTolerance = %+.2f
  FormatSpecUnderTolerance = %+.2f
  Inverted = false
  LockPosition = false
  MeasureType = 1
  OverTolerance = 0
  References2D = -> [View]
  Rotation = 0
  ScaleType = 0
  TheoreticalExact = false
  Type = 5
  UnderTolerance = 0
  X = 89.7773
  Y = 52.2584
FEATURE [TechDraw::DrawViewDimension] Dimension021
  Arbitrary = true
  ArbitraryTolerances = false
  EqualTolerance = true
  FormatSpec = 4x M5
  FormatSpecOverTolerance = %+.2f
  FormatSpecUnderTolerance = %+.2f
  Inverted = false
  LockPosition = false
  MeasureType = 1
  OverTolerance = 0
  References2D = -> [View]
  Rotation = 0
  ScaleType = 0
  TheoreticalExact = false
  Type = 4
  UnderTolerance = 0
  X = 35.3749
  Y = 34.2264
FEATURE [TechDraw::DrawViewDimension] Dimension022
  Arbitrary = false
  ArbitraryTolerances = false
  EqualTolerance = true
  FormatSpec = %.2f
  FormatSpecOverTolerance = %+.2f
  FormatSpecUnderTolerance = %+.2f
  Inverted = false
  LockPosition = false
  MeasureType = 1
  OverTolerance = 0
  References2D = -> [View]
  Rotation = 0
  ScaleType = 0
  TheoreticalExact = false
  Type = 1
  UnderTolerance = 0
  X = -65.125
  Y = 16.9043
FEATURE [TechDraw::DrawPage] Page  label="Motor bracket"
  KeepUpdated = true
  NextBalloonIndex = 1
  ProjectionType = 0
  Template = -> Template
  Views = -> [View,Dimension,Dimension002,Dimension003,Dimension004,Dimension005,Dimension006,Dimension007,Dimension008,Dimension010,Dimension011,Dimension012,Dimension013,Dimension014,Dimension015,Dimension016,Dimension017,Dimension018,Dimension019,Dimension020,Dimension021,Dimension022]
FEATURE [TechDraw::DrawSVGTemplate] Template001
  EditableTexts = DrawingTitle1=Carriage shim; DrawingTitle2=Count: 2; DrawingTitle3=Material: 5/8" Aluminum; DrawnBy=Andrew <owner>; Revision=V.1.0; Scale=Scale 1:1; Sheet=Sheet 1 of 1
  Height = 215.9
  Orientation = 1
  Width = 279.4
FEATURE [TechDraw::DrawViewPart] View001  label="Top"
  CoarseView = false
  Direction = (0,-1,0)
  Focus = 100
  HardHidden = false
  IsoCount = 0
  IsoHidden = false
  IsoVisible = false
  LockPosition = false
  Perspective = false
  Rotation = 0
  ScaleType = 0
  SeamHidden = false
  SeamVisible = true
  SmoothHidden = false
  SmoothVisible = true
  Source = -> [Body002]
  X = 141.965
  XDirection = (0,0,-1)
  Y = 158.025
FEATURE [TechDraw::DrawViewSection] SectionView  label="Section  - A"
  BaseView = -> View001
  CoarseView = false
  CutSurfaceDisplay = 2
  Direction = (-1,0,0)
  FileGeomPattern = <path> software/FreeCAD-asm3-Daily-Win64-Py3-Qt5-20210717/data/Mod/TechDraw/PAT/FCPAT.pat
  FileHatchPattern = <path> software/FreeCAD-asm3-Daily-Win64-Py3-Qt5-20210717/data/Mod/TechDraw/Patterns/simple.svg
  Focus = 100
  FuseBeforeCut = false
  HardHidden = false
  HatchScale = 1
  IsoCount = 0
  IsoHidden = false
  IsoVisible = false
  LockPosition = false
  NameGeomPattern = Diamond
  Perspective = false
  Rotation = 0
  ScaleType = 0
  SeamHidden = false
  SeamVisible = true
  SectionDirection = 2
  SectionNormal = (-1,0,0)
  SectionOrigin = (-70,-42,0)
  SmoothHidden = false
  SmoothVisible = true
  Source = -> [Body002]
  X = 142.468
  XDirection = (0,0,-1)
  Y = 107.95
FEATURE [TechDraw::DrawViewDimension] Dimension023
  Arbitrary = false
  ArbitraryTolerances = false
  EqualTolerance = true
  FormatSpec = %.2f
  FormatSpecOverTolerance = %+.2f
  FormatSpecUnderTolerance = %+.2f
  Inverted = false
  LockPosition = false
  MeasureType = 1
  OverTolerance = 0
  References2D = -> [View001]
  Rotation = 0
  ScaleType = 0
  TheoreticalExact = false
  Type = 1
  UnderTolerance = 0
  X = -0.503263
  Y = 36.5946
FEATURE [TechDraw::DrawViewDimension] Dimension024
  Arbitrary = false
  ArbitraryTolerances = false
  EqualTolerance = true
  FormatSpec = %.2f
  FormatSpecOverTolerance = %+.2f
  FormatSpecUnderTolerance = %+.2f
  Inverted = false
  LockPosition = false
  MeasureType = 1
  OverTolerance = 0
  References2D = -> [View001]
  Rotation = 0
  ScaleType = 0
  TheoreticalExact = false
  Type = 2
  UnderTolerance = 0
  X = -84.8724
  Y = 0
FEATURE [TechDraw::DrawViewDimension] Dimension025
  Arbitrary = false
  ArbitraryTolerances = false
  EqualTolerance = true
  FormatSpec = %.2f
  FormatSpecOverTolerance = %+.2f
  FormatSpecUnderTolerance = %+.2f
  Inverted = false
  LockPosition = false
  MeasureType = 1
  OverTolerance = 0
  References2D = -> [View001]
  Rotation = 0
  ScaleType = 0
  TheoreticalExact = false
  Type = 2
  UnderTolerance = 0
  X = -75.1077
  Y = 2.26469
FEATURE [TechDraw::DrawViewDimension] Dimension026
  Arbitrary = false
  ArbitraryTolerances = false
  EqualTolerance = true
  FormatSpec = %.2f
  FormatSpecOverTolerance = %+.2f
  FormatSpecUnderTolerance = %+.2f
  Inverted = false
  LockPosition = false
  MeasureType = 1
  OverTolerance = 0
  References2D = -> [View001]
  Rotation = 0
  ScaleType = 0
  TheoreticalExact = false
  Type = 1
  UnderTolerance = 0
  X = -40.5
  Y = 13.2321
FEATURE [TechDraw::DrawViewDimension] Dimension027
  Arbitrary = false
  ArbitraryTolerances = false
  EqualTolerance = true
  FormatSpec = %.2f
  FormatSpecOverTolerance = %+.2f
  FormatSpecUnderTolerance = %+.2f
  Inverted = false
  LockPosition = false
  MeasureType = 1
  OverTolerance = 0
  References2D = -> [View001]
  Rotation = 0
  ScaleType = 0
  TheoreticalExact = false
  Type = 1
  UnderTolerance = 0
  X = -76.3414
  Y = 31.5816
FEATURE [TechDraw::DrawViewDimension] Dimension028
  Arbitrary = false
  ArbitraryTolerances = false
  EqualTolerance = true
  FormatSpec = 8x ⌀%.2f
  FormatSpecOverTolerance = %+.2f
  FormatSpecUnderTolerance = %+.2f
  Inverted = false
  LockPosition = false
  MeasureType = 1
  OverTolerance = 0
  References2D = -> [View001]
  Rotation = 0
  ScaleType = 0
  TheoreticalExact = false
  Type = 5
  UnderTolerance = 0
  X = 40.0094
  Y = 10.8202
FEATURE [TechDraw::DrawViewDimension] Dimension029
  Arbitrary = false
  ArbitraryTolerances = false
  EqualTolerance = true
  FormatSpec = %.2f
  FormatSpecOverTolerance = %+.2f
  FormatSpecUnderTolerance = %+.2f
  Inverted = false
  LockPosition = false
  MeasureType = 1
  OverTolerance = 0
  References2D = -> [SectionView]
  Rotation = 0
  ScaleType = 0
  TheoreticalExact = false
  Type = 2
  UnderTolerance = 0
  X = -80.0914
  Y = 1.76142
FEATURE [TechDraw::DrawPage] Page001  label="Carriage shim"
  KeepUpdated = true
  NextBalloonIndex = 1
  ProjectionType = 0
  Template = -> Template001
  Views = -> [View001,SectionView,Dimension023,Dimension024,Dimension025,Dimension026,Dimension027,Dimension028,Dimension029]
FEATURE [TechDraw::DrawSVGTemplate] Template002
  EditableTexts = DrawingTitle1=Back plate; DrawingTitle2=Count: 1; DrawingTitle3=Material: 5/8" Aluminum; DrawnBy=Andrew <owner>; Revision=V.1.2; Scale=Scale 2:1; Sheet=Sheet 1 of 1
  Height = 215.9
  Orientation = 1
  Width = 279.4
FEATURE [TechDraw::DrawViewPart] View002  label="Front"
  CoarseView = false
  Direction = (0,-1,0)
  Focus = 100
  HardHidden = false
  IsoCount = 0
  IsoHidden = false
  IsoVisible = false
  LockPosition = false
  Perspective = false
  Rotation = 0
  Scale = 0.5
  ScaleType = 0
  SeamHidden = false
  SeamVisible = true
  SmoothHidden = false
  SmoothVisible = true
  Source = -> [Body]
  X = 130.302
  XDirection = (0,0,-1)
  Y = 138.649
FEATURE [TechDraw::DrawViewDimension] Dimension030
  Arbitrary = false
  ArbitraryTolerances = false
  EqualTolerance = true
  FormatSpec = %.2f
  FormatSpecOverTolerance = %+.2f
  FormatSpecUnderTolerance = %+.2f
  Inverted = false
  LockPosition = false
  MeasureType = 1
  OverTolerance = 0
  References2D = -> [View002]
  Rotation = 0
  ScaleType = 0
  TheoreticalExact = false
  Type = 1
  UnderTolerance = 0
  X = -3.27121
  Y = 60.5202
FEATURE [TechDraw::DrawViewDimension] Dimension031
  Arbitrary = false
  ArbitraryTolerances = false
  EqualTolerance = true
  FormatSpec = %.2f
  FormatSpecOverTolerance = %+.2f
  FormatSpecUnderTolerance = %+.2f
  Inverted = false
  LockPosition = false
  MeasureType = 1
  OverTolerance = 0
  References2D = -> [View002]
  Rotation = 0
  ScaleType = 0
  TheoreticalExact = false
  Type = 2
  UnderTolerance = 0
  X = -93.4889
  Y = 2.27887
FEATURE [TechDraw::DrawViewDimension] Dimension032
  Arbitrary = false
  ArbitraryTolerances = false
  EqualTolerance = true
  FormatSpec = %.2f
  FormatSpecOverTolerance = %+.2f
  FormatSpecUnderTolerance = %+.2f
  Inverted = false
  LockPosition = false
  MeasureType = 1
  OverTolerance = 0
  References2D = -> [View002]
  Rotation = 0
  ScaleType = 0
  TheoreticalExact = false
  Type = 2
  UnderTolerance = 0
  X = -85.7364
  Y = 1.91423
FEATURE [TechDraw::DrawViewDimension] Dimension033
  Arbitrary = false
  ArbitraryTolerances = false
  EqualTolerance = true
  FormatSpec = %.2f
  FormatSpecOverTolerance = %+.2f
  FormatSpecUnderTolerance = %+.2f
  Inverted = false
  LockPosition = false
  MeasureType = 1
  OverTolerance = 0
  References2D = -> [View002]
  Rotation = 0
  ScaleType = 0
  TheoreticalExact = false
  Type = 2
  UnderTolerance = 0
  X = -84.0131
  Y = 48.4506
FEATURE [TechDraw::DrawViewDimension] Dimension034
  Arbitrary = false
  ArbitraryTolerances = false
  EqualTolerance = true
  FormatSpec = %.2f
  FormatSpecOverTolerance = %+.2f
  FormatSpecUnderTolerance = %+.2f
  Inverted = false
  LockPosition = false
  MeasureType = 1
  OverTolerance = 0
  References2D = -> [View002]
  Rotation = 0
  ScaleType = 0
  TheoreticalExact = false
  Type = 2
  UnderTolerance = 0
  X = -52.9747
  Y = 0
FEATURE [TechDraw::DrawViewDimension] Dimension035
  Arbitrary = false
  ArbitraryTolerances = false
  EqualTolerance = true
  FormatSpec = %.2f
  FormatSpecOverTolerance = %+.2f
  FormatSpecUnderTolerance = %+.2f
  Inverted = false
  LockPosition = false
  MeasureType = 1
  OverTolerance = 0
  References2D = -> [View002]
  Rotation = 0
  ScaleType = 0
  TheoreticalExact = false
  Type = 1
  UnderTolerance = 0
  X = -41.5117
  Y = 24.7806
FEATURE [TechDraw::DrawViewDimension] Dimension036
  Arbitrary = false
  ArbitraryTolerances = false
  EqualTolerance = true
  FormatSpec = %.2f
  FormatSpecOverTolerance = %+.2f
  FormatSpecUnderTolerance = %+.2f
  Inverted = false
  LockPosition = false
  MeasureType = 1
  OverTolerance = 0
  References2D = -> [View002]
  Rotation = 0
  ScaleType = 0
  TheoreticalExact = false
  Type = 2
  UnderTolerance = 0
  X = -52.9925
  Y = -17.6773
FEATURE [TechDraw::DrawViewDimension] Dimension037
  Arbitrary = false
  ArbitraryTolerances = false
  EqualTolerance = true
  FormatSpec = %.2f
  FormatSpecOverTolerance = %+.2f
  FormatSpecUnderTolerance = %+.2f
  Inverted = false
  LockPosition = false
  MeasureType = 1
  OverTolerance = 0
  References2D = -> [View002]
  Rotation = 0
  ScaleType = 0
  TheoreticalExact = false
  Type = 1
  UnderTolerance = 0
  X = -61.7396
  Y = -40.8051
FEATURE [TechDraw::DrawViewDimension] Dimension038
  Arbitrary = false
  ArbitraryTolerances = false
  EqualTolerance = true
  FormatSpec = 4x %.2f
  FormatSpecOverTolerance = %+.2f
  FormatSpecUnderTolerance = %+.2f
  Inverted = false
  LockPosition = false
  MeasureType = 1
  OverTolerance = 0
  References2D = -> [View002]
  Rotation = 0
  ScaleType = 0
  TheoreticalExact = false
  Type = 1
  UnderTolerance = 0
  X = -48.0628
  Y = 49.205
FEATURE [TechDraw::DrawViewDimension] Dimension039
  Arbitrary = false
  ArbitraryTolerances = false
  EqualTolerance = true
  FormatSpec = %.2f
  FormatSpecOverTolerance = %+.2f
  FormatSpecUnderTolerance = %+.2f
  Inverted = false
  LockPosition = false
  MeasureType = 1
  OverTolerance = 0
  References2D = -> [View002]
  Rotation = 0
  ScaleType = 0
  TheoreticalExact = false
  Type = 1
  UnderTolerance = 0
  X = -5.29898
  Y = 49.3036
FEATURE [TechDraw::DrawViewDimension] Dimension040
  Arbitrary = false
  ArbitraryTolerances = false
  EqualTolerance = true
  FormatSpec = %.2f
  FormatSpecOverTolerance = %+.2f
  FormatSpecUnderTolerance = %+.2f
  Inverted = false
  LockPosition = false
  MeasureType = 1
  OverTolerance = 0
  References2D = -> [View002]
  Rotation = 0
  ScaleType = 0
  TheoreticalExact = false
  Type = 1
  UnderTolerance = 0
  X = -21.8242
  Y = 49.3354
FEATURE [TechDraw::DrawViewDimension] Dimension041
  Arbitrary = false
  ArbitraryTolerances = false
  EqualTolerance = true
  FormatSpec = %.2f
  FormatSpecOverTolerance = %+.2f
  FormatSpecUnderTolerance = %+.2f
  Inverted = false
  LockPosition = false
  MeasureType = 1
  OverTolerance = 0
  References2D = -> [View002]
  Rotation = 0
  ScaleType = 0
  TheoreticalExact = false
  Type = 2
  UnderTolerance = 0
  X = -22.0362
  Y = 27.023
FEATURE [TechDraw::DrawViewDimension] Dimension042
  Arbitrary = false
  ArbitraryTolerances = false
  EqualTolerance = true
  FormatSpec = %.2f
  FormatSpecOverTolerance = %+.2f
  FormatSpecUnderTolerance = %+.2f
  Inverted = false
  LockPosition = false
  MeasureType = 1
  OverTolerance = 0
  References2D = -> [View002]
  Rotation = 0
  ScaleType = 0
  TheoreticalExact = false
  Type = 1
  UnderTolerance = 0
  X = 63.9601
  Y = 53.8976
FEATURE [TechDraw::DrawViewDimension] Dimension043
  Arbitrary = false
  ArbitraryTolerances = false
  EqualTolerance = true
  FormatSpec = %.2f
  FormatSpecOverTolerance = %+.2f
  FormatSpecUnderTolerance = %+.2f
  Inverted = false
  LockPosition = false
  MeasureType = 1
  OverTolerance = 0
  References2D = -> [View002]
  Rotation = 0
  ScaleType = 0
  TheoreticalExact = false
  Type = 1
  UnderTolerance = 0
  X = -69.6564
  Y = 49.2163
FEATURE [TechDraw::DrawViewDimension] Dimension044
  Arbitrary = false
  ArbitraryTolerances = false
  EqualTolerance = true
  FormatSpec = %.2f
  FormatSpecOverTolerance = %+.2f
  FormatSpecUnderTolerance = %+.2f
  Inverted = false
  LockPosition = false
  MeasureType = 1
  OverTolerance = 0
  References2D = -> [View002]
  Rotation = 0
  ScaleType = 0
  TheoreticalExact = false
  Type = 2
  UnderTolerance = 0
  X = -22.1711
  Y = 2.10565
FEATURE [TechDraw::DrawViewDimension] Dimension045
  Arbitrary = false
  ArbitraryTolerances = false
  EqualTolerance = true
  FormatSpec = %.2f
  FormatSpecOverTolerance = %+.2f
  FormatSpecUnderTolerance = %+.2f
  Inverted = false
  LockPosition = false
  MeasureType = 1
  OverTolerance = 0
  References2D = -> [View002]
  Rotation = 0
  ScaleType = 0
  TheoreticalExact = false
  Type = 1
  UnderTolerance = 0
  X = 30.325
  Y = -7.05126
FEATURE [TechDraw::DrawViewDimension] Dimension046
  Arbitrary = false
  ArbitraryTolerances = false
  EqualTolerance = true
  FormatSpec = %.2f
  FormatSpecOverTolerance = %+.2f
  FormatSpecUnderTolerance = %+.2f
  Inverted = false
  LockPosition = false
  MeasureType = 1
  OverTolerance = 0
  References2D = -> [View002]
  Rotation = 0
  ScaleType = 0
  TheoreticalExact = false
  Type = 2
  UnderTolerance = 0
  X = 27.5991
  Y = 6.79707
FEATURE [TechDraw::DrawViewDimension] Dimension047
  Arbitrary = false
  ArbitraryTolerances = false
  EqualTolerance = true
  FormatSpec = %.2f
  FormatSpecOverTolerance = %+.2f
  FormatSpecUnderTolerance = %+.2f
  Inverted = false
  LockPosition = false
  MeasureType = 1
  OverTolerance = 0
  References2D = -> [View002]
  Rotation = 0
  ScaleType = 0
  TheoreticalExact = false
  Type = 2
  UnderTolerance = 0
  X = 10.9054
  Y = 27.5364
FEATURE [TechDraw::DrawViewDimension] Dimension048
  Arbitrary = false
  ArbitraryTolerances = false
  EqualTolerance = true
  FormatSpec = %.2f
  FormatSpecOverTolerance = %+.2f
  FormatSpecUnderTolerance = %+.2f
  Inverted = false
  LockPosition = false
  MeasureType = 1
  OverTolerance = 0
  References2D = -> [View002]
  Rotation = 0
  ScaleType = 0
  TheoreticalExact = false
  Type = 1
  UnderTolerance = 0
  X = 48.2132
  Y = 8.77693
FEATURE [TechDraw::DrawViewDimension] Dimension049
  Arbitrary = false
  ArbitraryTolerances = false
  EqualTolerance = true
  FormatSpec = %.2f
  FormatSpecOverTolerance = %+.2f
  FormatSpecUnderTolerance = %+.2f
  Inverted = false
  LockPosition = false
  MeasureType = 1
  OverTolerance = 0
  References2D = -> [View002]
  Rotation = 0
  ScaleType = 0
  TheoreticalExact = false
  Type = 1
  UnderTolerance = 0
  X = 82.3468
  Y = 50.4369
FEATURE [TechDraw::DrawViewDimension] Dimension050
  Arbitrary = false
  ArbitraryTolerances = false
  EqualTolerance = true
  FormatSpec = %.2f
  FormatSpecOverTolerance = %+.2f
  FormatSpecUnderTolerance = %+.2f
  Inverted = false
  LockPosition = false
  MeasureType = 1
  OverTolerance = 0
  References2D = -> [View002]
  Rotation = 0
  ScaleType = 0
  TheoreticalExact = false
  Type = 1
  UnderTolerance = 0
  X = 68.0648
  Y = 9.88153
FEATURE [TechDraw::DrawViewDimension] Dimension051
  Arbitrary = false
  ArbitraryTolerances = false
  EqualTolerance = true
  FormatSpec = %.2f
  FormatSpecOverTolerance = %+.2f
  FormatSpecUnderTolerance = %+.2f
  Inverted = false
  LockPosition = false
  MeasureType = 1
  OverTolerance = 0
  References2D = -> [View002]
  Rotation = 0
  ScaleType = 0
  TheoreticalExact = false
  Type = 2
  UnderTolerance = 0
  X = 81.0612
  Y = 29.0798
FEATURE [TechDraw::DrawViewDimension] Dimension052
  Arbitrary = false
  ArbitraryTolerances = false
  EqualTolerance = true
  FormatSpec = %.2f
  FormatSpecOverTolerance = %+.2f
  FormatSpecUnderTolerance = %+.2f
  Inverted = false
  LockPosition = false
  MeasureType = 1
  OverTolerance = 0
  References2D = -> [View002]
  Rotation = 0
  ScaleType = 0
  TheoreticalExact = false
  Type = 2
  UnderTolerance = 0
  X = 80.7529
  Y = 0.93912
FEATURE [TechDraw::DrawViewDimension] Dimension053
  Arbitrary = true
  ArbitraryTolerances = false
  EqualTolerance = true
  FormatSpec = 10x M5
  FormatSpecOverTolerance = %+.2f
  FormatSpecUnderTolerance = %+.2f
  Inverted = false
  LockPosition = false
  MeasureType = 1
  OverTolerance = 0
  References2D = -> [View002]
  Rotation = 0
  ScaleType = 0
  TheoreticalExact = false
  Type = 4
  UnderTolerance = 0
  X = -47.8557
  Y = 34.2647
FEATURE [TechDraw::DrawViewDimension] Dimension054
  Arbitrary = true
  ArbitraryTolerances = false
  EqualTolerance = true
  FormatSpec = 6x 1/4-20
  FormatSpecOverTolerance = %+.2f
  FormatSpecUnderTolerance = %+.2f
  Inverted = false
  LockPosition = false
  MeasureType = 1
  OverTolerance = 0
  References2D = -> [View002]
  Rotation = 0
  ScaleType = 0
  TheoreticalExact = false
  Type = 4
  UnderTolerance = 0
  X = -37.3274
  Y = 0.957114
FEATURE [TechDraw::DrawViewDimension] Dimension055
  Arbitrary = false
  ArbitraryTolerances = false
  EqualTolerance = true
  FormatSpec = 16x ⌀%.2f
  FormatSpecOverTolerance = %+.2f
  FormatSpecUnderTolerance = %+.2f
  Inverted = false
  LockPosition = false
  MeasureType = 1
  OverTolerance = 0
  References2D = -> [View002]
  Rotation = 0
  ScaleType = 0
  TheoreticalExact = false
  Type = 5
  UnderTolerance = 0
  X = 15.888
  Y = -20.2908
FEATURE [TechDraw::DrawViewDimension] Dimension056
  Arbitrary = false
  ArbitraryTolerances = false
  EqualTolerance = true
  FormatSpec = 16x ⌀%.2f ↓6.00
  FormatSpecOverTolerance = %+.2f
  FormatSpecUnderTolerance = %+.2f
  Inverted = false
  LockPosition = false
  MeasureType = 1
  OverTolerance = 0
  References2D = -> [View002]
  Rotation = 0
  ScaleType = 0
  TheoreticalExact = false
  Type = 5
  UnderTolerance = 0
  X = 30.0533
  Y = -29.2877
FEATURE [TechDraw::DrawViewDimension] Dimension057
  Arbitrary = false
  ArbitraryTolerances = false
  EqualTolerance = true
  FormatSpec = 4x ⌀%.2f ↓9.00
  FormatSpecOverTolerance = %+.2f
  FormatSpecUnderTolerance = %+.2f
  Inverted = false
  LockPosition = false
  MeasureType = 1
  OverTolerance = 0
  References2D = -> [View002]
  Rotation = 0
  ScaleType = 0
  TheoreticalExact = false
  Type = 5
  UnderTolerance = 0
  X = 33.3076
  Y = 26.2249
FEATURE [TechDraw::DrawViewDimension] Dimension058
  Arbitrary = false
  ArbitraryTolerances = false
  EqualTolerance = true
  FormatSpec = 4x ⌀%.2f
  FormatSpecOverTolerance = %+.2f
  FormatSpecUnderTolerance = %+.2f
  Inverted = false
  LockPosition = false
  MeasureType = 1
  OverTolerance = 0
  References2D = -> [View002]
  Rotation = 0
  ScaleType = 0
  TheoreticalExact = false
  Type = 5
  UnderTolerance = 0
  X = 39.2417
  Y = 19.908
FEATURE [TechDraw::DrawViewPart] View003  label="Right"
  CoarseView = false
  Direction = (-1,0,0)
  Focus = 100
  HardHidden = false
  IsoCount = 0
  IsoHidden = false
  IsoVisible = false
  LockPosition = false
  Perspective = false
  Rotation = 0
  Scale = 0.5
  ScaleType = 0
  SeamHidden = false
  SeamVisible = true
  SmoothHidden = false
  SmoothVisible = true
  Source = -> [Body]
  X = 130.223
  XDirection = (0,0,-1)
  Y = 81.4353
FEATURE [TechDraw::DrawViewDimension] Dimension059
  Arbitrary = false
  ArbitraryTolerances = false
  EqualTolerance = true
  FormatSpec = %.2f
  FormatSpecOverTolerance = %+.2f
  FormatSpecUnderTolerance = %+.2f
  Inverted = false
  LockPosition = false
  MeasureType = 1
  OverTolerance = 0
  References2D = -> [View003]
  Rotation = 0
  ScaleType = 0
  TheoreticalExact = false
  Type = 2
  UnderTolerance = 0
  X = -92.8923
  Y = 2.34383
FEATURE [TechDraw::DrawViewDimension] Dimension060
  Arbitrary = false
  ArbitraryTolerances = false
  EqualTolerance = true
  FormatSpec = %.2f
  FormatSpecOverTolerance = %+.2f
  FormatSpecUnderTolerance = %+.2f
  Inverted = false
  LockPosition = false
  MeasureType = 1
  OverTolerance = 0
  References2D = -> [View003]
  Rotation = 0
  ScaleType = 0
  TheoreticalExact = false
  Type = 1
  UnderTolerance = 0
  X = 45.1328
  Y = -7.32234
FEATURE [TechDraw::DrawViewDimension] Dimension061
  Arbitrary = true
  ArbitraryTolerances = false
  EqualTolerance = true
  FormatSpec = 1/4-20 ↓25.0
  FormatSpecOverTolerance = %+.2f
  FormatSpecUnderTolerance = %+.2f
  Inverted = false
  LockPosition = false
  MeasureType = 1
  OverTolerance = 0
  References2D = -> [View003]
  Rotation = 0
  ScaleType = 0
  TheoreticalExact = false
  Type = 4
  UnderTolerance = 0
  X = 28.522
  Y = 10.7197
FEATURE [TechDraw::DrawSVGTemplate] Template003
  EditableTexts = DrawingTitle1=Ballnut shim; DrawingTitle2=Count: 1; DrawingTitle3=Material: 0.7mm Aluminum; DrawnBy=Andrew <owner>; Revision=V.1.0; Scale=Scale 1:1; Sheet=Sheet 1 of 1
  Height = 215.9
  Orientation = 1
  Width = 279.4
FEATURE [TechDraw::DrawViewPart] View004  label="Front  "
  CoarseView = false
  Direction = (0,-1,0)
  Focus = 100
  HardHidden = false
  IsoCount = 0
  IsoHidden = false
  IsoVisible = false
  LockPosition = false
  Perspective = false
  Rotation = 0
  ScaleType = 0
  SeamHidden = false
  SeamVisible = true
  SmoothHidden = false
  SmoothVisible = true
  Source = -> [Body003]
  X = 93.1481
  XDirection = (1,0,0)
  Y = 146.45
FEATURE [TechDraw::DrawViewDimension] Dimension062
  Arbitrary = false
  ArbitraryTolerances = false
  EqualTolerance = true
  FormatSpec = %.2f
  FormatSpecOverTolerance = %+.2f
  FormatSpecUnderTolerance = %+.2f
  Inverted = false
  LockPosition = false
  MeasureType = 1
  OverTolerance = 0
  References2D = -> [View004]
  Rotation = 0
  ScaleType = 0
  TheoreticalExact = false
  Type = 2
  UnderTolerance = 0
  X = 37.6142
  Y = 1.00653
FEATURE [TechDraw::DrawViewDimension] Dimension063
  Arbitrary = false
  ArbitraryTolerances = false
  EqualTolerance = true
  FormatSpec = %.2f
  FormatSpecOverTolerance = %+.2f
  FormatSpecUnderTolerance = %+.2f
  Inverted = false
  LockPosition = false
  MeasureType = 1
  OverTolerance = 0
  References2D = -> [View004]
  Rotation = 0
  ScaleType = 0
  TheoreticalExact = false
  Type = 1
  UnderTolerance = 0
  X = 1.76142
  Y = 31.3234
FEATURE [TechDraw::DrawViewDimension] Dimension064
  Arbitrary = false
  ArbitraryTolerances = false
  EqualTolerance = true
  FormatSpec = %.2f
  FormatSpecOverTolerance = %+.2f
  FormatSpecUnderTolerance = %+.2f
  Inverted = false
  LockPosition = false
  MeasureType = 1
  OverTolerance = 0
  References2D = -> [View004]
  Rotation = 0
  ScaleType = 0
  TheoreticalExact = false
  Type = 1
  UnderTolerance = 0
  X = -1.25816
  Y = -23.3234
FEATURE [TechDraw::DrawViewDimension] Dimension065
  Arbitrary = false
  ArbitraryTolerances = false
  EqualTolerance = true
  FormatSpec = 4x ⌀%.2f
  FormatSpecOverTolerance = %+.2f
  FormatSpecUnderTolerance = %+.2f
  Inverted = false
  LockPosition = false
  MeasureType = 1
  OverTolerance = 0
  References2D = -> [View004]
  Rotation = 0
  ScaleType = 0
  TheoreticalExact = false
  Type = 5
  UnderTolerance = 0
  X = 41.5192
  Y = 28.9376
FEATURE [TechDraw::DrawViewDimension] Dimension066
  Arbitrary = false
  ArbitraryTolerances = false
  EqualTolerance = true
  FormatSpec = %.2f
  FormatSpecOverTolerance = %+.2f
  FormatSpecUnderTolerance = %+.2f
  Inverted = false
  LockPosition = false
  MeasureType = 1
  OverTolerance = 0
  References2D = -> [View004]
  Rotation = 0
  ScaleType = 0
  TheoreticalExact = false
  Type = 2
  UnderTolerance = 0
  X = -37.5751
  Y = 0.503263
FEATURE [TechDraw::DrawViewAnnotation] Annotation
  Font = osifont
  LineSpace = 80
  LockPosition = false
  MaxWidth = -1
  Rotation = 0
  ScaleType = 0
  Text = This part is optional and can be  | eliminated by sanding carriage  | shims down to 15.0mm
  TextSize = 4
  TextStyle = 0
  X = 92.8965
  Y = 95.1168
FEATURE [TechDraw::DrawPage] Page003  label="Ballnut shim"
  KeepUpdated = true
  NextBalloonIndex = 1
  ProjectionType = 0
  Template = -> Template003
  Views = -> [View004,Dimension062,Dimension063,Dimension064,Dimension065,Dimension066,Annotation]
FEATURE [TechDraw::DrawSVGTemplate] Template004
  EditableTexts = DrawingTitle1=Ballnut shim X axis; DrawingTitle2=Count: 1; DrawingTitle3=Material: 16.75mm Aluminum; DrawnBy=Andrew <owner>; Revision=V.1.0; Scale=Scale 1:1; Sheet=Sheet 1 of 1
  Height = 215.9
  Orientation = 1
  Width = 279.4
FEATURE [TechDraw::DrawProjGroupItem] ProjItem  label="Front001"
  CoarseView = false
  Direction = (0,-1,0)
  Focus = 100
  HardHidden = false
  IsoCount = 0
  IsoHidden = false
  IsoVisible = false
  LockPosition = true
  Perspective = false
  Rotation = 0
  RotationVector = (1,0,0)
  ScaleType = 2
  SeamHidden = false
  SeamVisible = true
  SmoothHidden = false
  SmoothVisible = true
  Source = -> [Body005]
  Type = 0
  X = 0
  XDirection = (1,0,0)
  Y = 0
FEATURE [TechDraw::DrawProjGroupItem] ProjItem001  label="Left"
  CoarseView = false
  Direction = (-1,-1e-16,0)
  Focus = 100
  HardHidden = false
  IsoCount = 0
  IsoHidden = false
  IsoVisible = false
  LockPosition = false
  Perspective = false
  Rotation = 0
  RotationVector = (1,0,0)
  ScaleType = 2
  SeamHidden = false
  SeamVisible = true
  SmoothHidden = false
  SmoothVisible = true
  Source = -> [Body005]
  Type = 1
  X = 64.375
  XDirection = (1e-16,-1,0)
  Y = 0
FEATURE [TechDraw::DrawProjGroup] ProjGroup
  Anchor = -> ProjItem
  AutoDistribute = true
  LockPosition = false
  ProjectionType = 0
  Rotation = 0
  ScaleType = 0
  Source = -> [Body005]
  Views = -> [ProjItem,ProjItem001]
  X = 101.2
  Y = 125.564
  spacingX = 30
  spacingY = 15
FEATURE [TechDraw::DrawViewDimension] Dimension067
  Arbitrary = false
  ArbitraryTolerances = false
  EqualTolerance = true
  FormatSpec = %.2f
  FormatSpecOverTolerance = %+.2f
  FormatSpecUnderTolerance = %+.2f
  Inverted = false
  LockPosition = false
  MeasureType = 1
  OverTolerance = 0
  References2D = -> [ProjItem001]
  Rotation = 0
  ScaleType = 0
  TheoreticalExact = false
  Type = 2
  UnderTolerance = 0
  X = 22.2147
  Y = 0
FEATURE [TechDraw::DrawViewDimension] Dimension068
  Arbitrary = false
  ArbitraryTolerances = false
  EqualTolerance = true
  FormatSpec = %.2f
  FormatSpecOverTolerance = %+.2f
  FormatSpecUnderTolerance = %+.2f
  Inverted = false
  LockPosition = false
  MeasureType = 1
  OverTolerance = 0
  References2D = -> [ProjItem001]
  Rotation = 0
  ScaleType = 0
  TheoreticalExact = false
  Type = 1
  UnderTolerance = 0
  X = 0
  Y = 31.0718
FEATURE [TechDraw::DrawViewDimension] Dimension069
  Arbitrary = false
  ArbitraryTolerances = false
  EqualTolerance = true
  FormatSpec = %.2f
  FormatSpecOverTolerance = %+.2f
  FormatSpecUnderTolerance = %+.2f
  Inverted = false
  LockPosition = false
  MeasureType = 1
  OverTolerance = 0
  References2D = -> [ProjItem]
  Rotation = 0
  ScaleType = 0
  TheoreticalExact = false
  Type = 1
  UnderTolerance = 0
  X = 2.26469
  Y = 31.6273
FEATURE [TechDraw::DrawViewDimension] Dimension070
  Arbitrary = false
  ArbitraryTolerances = false
  EqualTolerance = true
  FormatSpec = %.2f
  FormatSpecOverTolerance = %+.2f
  FormatSpecUnderTolerance = %+.2f
  Inverted = false
  LockPosition = false
  MeasureType = 1
  OverTolerance = 0
  References2D = -> [ProjItem]
  Rotation = 0
  ScaleType = 0
  TheoreticalExact = false
  Type = 2
  UnderTolerance = 0
  X = 32.5816
  Y = 0.754895
FEATURE [TechDraw::DrawViewDimension] Dimension071
  Arbitrary = false
  ArbitraryTolerances = false
  EqualTolerance = true
  FormatSpec = 4x ⌀%.2f
  FormatSpecOverTolerance = %+.2f
  FormatSpecUnderTolerance = %+.2f
  Inverted = false
  LockPosition = false
  MeasureType = 1
  OverTolerance = 0
  References2D = -> [ProjItem]
  Rotation = 0
  ScaleType = 0
  TheoreticalExact = false
  Type = 5
  UnderTolerance = 0
  X = 37.9964
  Y = 34.4735
FEATURE [TechDraw::DrawPage] Page004  label="Ballnut shim X axis"
  KeepUpdated = true
  NextBalloonIndex = 1
  ProjectionType = 0
  Template = -> Template004
  Views = -> [ProjGroup,Dimension067,Dimension068,Dimension069,Dimension070,Dimension071]
FEATURE [TechDraw::DrawSVGTemplate] Template005
  EditableTexts = DrawingTitle1=Front plate; DrawingTitle2=Count: 1; DrawingTitle3=Material: 5/8" Aluminum; DrawnBy=Andrew <owner>; Revision=V.1.0; Scale=Scale 2:1; Sheet=Sheet 1 of 1
  Height = 215.9
  Orientation = 1
  Width = 279.4
FEATURE [TechDraw::DrawProjGroupItem] ProjItem002  label="Front002"
  CoarseView = false
  Direction = (0,-1,0)
  Focus = 100
  HardHidden = false
  IsoCount = 0
  IsoHidden = false
  IsoVisible = false
  LockPosition = true
  Perspective = false
  Rotation = 0
  RotationVector = (0,0,1)
  Scale = 0.5
  ScaleType = 2
  SeamHidden = false
  SeamVisible = true
  SmoothHidden = false
  SmoothVisible = true
  Source = -> [Body001]
  Type = 0
  X = 0
  XDirection = (0,0,1)
  Y = 0
FEATURE [TechDraw::DrawProjGroupItem] ProjItem003  label="Right001"
  CoarseView = false
  Direction = (0,-1e-16,1)
  Focus = 100
  HardHidden = false
  IsoCount = 0
  IsoHidden = false
  IsoVisible = false
  LockPosition = false
  Perspective = false
  Rotation = 0
  RotationVector = (1,0,0)
  Scale = 0.5
  ScaleType = 2
  SeamHidden = false
  SeamVisible = true
  SmoothHidden = false
  SmoothVisible = true
  Source = -> [Body001]
  Type = 2
  X = -80.925
  XDirection = (0,1,1e-16)
  Y = 0
FEATURE [TechDraw::DrawProjGroup] ProjGroup001
  Anchor = -> ProjItem002
  AutoDistribute = true
  LockPosition = false
  ProjectionType = 0
  Rotation = 0
  Scale = 0.5
  ScaleType = 0
  Source = -> [Body001]
  Views = -> [ProjItem002,ProjItem003]
  X = 141.874
  Y = 138.822
  spacingX = 25
  spacingY = 15
FEATURE [TechDraw::DrawViewDimension] Dimension072
  Arbitrary = false
  ArbitraryTolerances = false
  EqualTolerance = true
  FormatSpec = %.2f
  FormatSpecOverTolerance = %+.2f
  FormatSpecUnderTolerance = %+.2f
  Inverted = false
  LockPosition = false
  MeasureType = 1
  OverTolerance = 0
  References2D = -> [ProjItem003]
  Rotation = 0
  ScaleType = 0
  TheoreticalExact = false
  Type = 1
  UnderTolerance = 0
  X = -1.00653
  Y = 49.1968
FEATURE [TechDraw::DrawViewDimension] Dimension073
  Arbitrary = false
  ArbitraryTolerances = false
  EqualTolerance = true
  FormatSpec = %.2f
  FormatSpecOverTolerance = %+.2f
  FormatSpecUnderTolerance = %+.2f
  Inverted = false
  LockPosition = false
  MeasureType = 1
  OverTolerance = 0
  References2D = -> [ProjItem003]
  Rotation = 0
  ScaleType = 0
  TheoreticalExact = false
  Type = 2
  UnderTolerance = 0
  X = -15.7517
  Y = 1.00653
FEATURE [TechDraw::DrawViewDimension] Dimension074
  Arbitrary = false
  ArbitraryTolerances = false
  EqualTolerance = true
  FormatSpec = %.2f
  FormatSpecOverTolerance = %+.2f
  FormatSpecUnderTolerance = %+.2f
  Inverted = false
  LockPosition = false
  MeasureType = 1
  OverTolerance = 0
  References2D = -> [ProjItem003]
  Rotation = 0
  ScaleType = 0
  TheoreticalExact = false
  Type = 2
  UnderTolerance = 0
  X = -10.1708
  Y = 34.5565
FEATURE [TechDraw::DrawViewDimension] Dimension075
  Arbitrary = true
  ArbitraryTolerances = false
  EqualTolerance = true
  FormatSpec = 1/4-20 ↓25.0
  FormatSpecOverTolerance = %+.2f
  FormatSpecUnderTolerance = %+.2f
  Inverted = false
  LockPosition = false
  MeasureType = 1
  OverTolerance = 0
  References2D = -> [ProjItem003]
  Rotation = 0
  ScaleType = 0
  TheoreticalExact = false
  Type = 4
  UnderTolerance = 0
  X = 15.4414
  Y = 47.9834
FEATURE [TechDraw::DrawViewDimension] Dimension076
  Arbitrary = false
  ArbitraryTolerances = false
  EqualTolerance = true
  FormatSpec = %.2f
  FormatSpecOverTolerance = %+.2f
  FormatSpecUnderTolerance = %+.2f
  Inverted = false
  LockPosition = false
  MeasureType = 1
  OverTolerance = 0
  References2D = -> [ProjItem002]
  Rotation = 0
  ScaleType = 0
  TheoreticalExact = false
  Type = 1
  UnderTolerance = 0
  X = 7.1e-15
  Y = 57.2673
FEATURE [TechDraw::DrawViewDimension] Dimension077
  Arbitrary = false
  ArbitraryTolerances = false
  EqualTolerance = true
  FormatSpec = %.2f
  FormatSpecOverTolerance = %+.2f
  FormatSpecUnderTolerance = %+.2f
  Inverted = false
  LockPosition = false
  MeasureType = 1
  OverTolerance = 0
  References2D = -> [ProjItem002]
  Rotation = 0
  ScaleType = 0
  TheoreticalExact = false
  Type = 2
  UnderTolerance = 0
  X = 55.2688
  Y = 28.5952
FEATURE [TechDraw::DrawViewDimension] Dimension078
  Arbitrary = false
  ArbitraryTolerances = false
  EqualTolerance = true
  FormatSpec = %.2f
  FormatSpecOverTolerance = %+.2f
  FormatSpecUnderTolerance = %+.2f
  Inverted = false
  LockPosition = false
  MeasureType = 1
  OverTolerance = 0
  References2D = -> [ProjItem002]
  Rotation = 0
  ScaleType = 0
  TheoreticalExact = false
  Type = 2
  UnderTolerance = 0
  X = 55.2689
  Y = 0.797595
FEATURE [TechDraw::DrawViewDimension] Dimension079
  Arbitrary = false
  ArbitraryTolerances = false
  EqualTolerance = true
  FormatSpec = %.2f
  FormatSpecOverTolerance = %+.2f
  FormatSpecUnderTolerance = %+.2f
  Inverted = false
  LockPosition = false
  MeasureType = 1
  OverTolerance = 0
  References2D = -> [ProjItem002]
  Rotation = 0
  ScaleType = 0
  TheoreticalExact = false
  Type = 2
  UnderTolerance = 0
  X = 59.6476
  Y = 45.8323
FEATURE [TechDraw::DrawViewDimension] Dimension080
  Arbitrary = false
  ArbitraryTolerances = false
  EqualTolerance = true
  FormatSpec = %.2f
  FormatSpecOverTolerance = %+.2f
  FormatSpecUnderTolerance = %+.2f
  Inverted = false
  LockPosition = false
  MeasureType = 1
  OverTolerance = 0
  References2D = -> [ProjItem002]
  Rotation = 0
  ScaleType = 0
  TheoreticalExact = false
  Type = 1
  UnderTolerance = 0
  X = 59.8816
  Y = -38.6012
FEATURE [TechDraw::DrawViewDimension] Dimension081
  Arbitrary = false
  ArbitraryTolerances = false
  EqualTolerance = true
  FormatSpec = %.2f
  FormatSpecOverTolerance = %+.2f
  FormatSpecUnderTolerance = %+.2f
  Inverted = false
  LockPosition = false
  MeasureType = 1
  OverTolerance = 0
  References2D = -> [ProjItem002]
  Rotation = 0
  ScaleType = 0
  TheoreticalExact = false
  Type = 1
  UnderTolerance = 0
  X = 39.7286
  Y = 48.3996
FEATURE [TechDraw::DrawViewDimension] Dimension082
  Arbitrary = false
  ArbitraryTolerances = false
  EqualTolerance = true
  FormatSpec = %.2f
  FormatSpecOverTolerance = %+.2f
  FormatSpecUnderTolerance = %+.2f
  Inverted = false
  LockPosition = false
  MeasureType = 1
  OverTolerance = 0
  References2D = -> [ProjItem002]
  Rotation = 0
  ScaleType = 0
  TheoreticalExact = false
  Type = 1
  UnderTolerance = 0
  X = 18.8405
  Y = 48.3996
FEATURE [TechDraw::DrawViewDimension] Dimension083
  Arbitrary = false
  ArbitraryTolerances = false
  EqualTolerance = true
  FormatSpec = %.2f
  FormatSpecOverTolerance = %+.2f
  FormatSpecUnderTolerance = %+.2f
  Inverted = false
  LockPosition = false
  MeasureType = 1
  OverTolerance = 0
  References2D = -> [ProjItem002]
  Rotation = 0
  ScaleType = 0
  TheoreticalExact = false
  Type = 1
  UnderTolerance = 0
  X = -34.829
  Y = 51.3381
FEATURE [TechDraw::DrawViewDimension] Dimension084
  Arbitrary = false
  ArbitraryTolerances = false
  EqualTolerance = true
  FormatSpec = %.2f
  FormatSpecOverTolerance = %+.2f
  FormatSpecUnderTolerance = %+.2f
  Inverted = false
  LockPosition = false
  MeasureType = 1
  OverTolerance = 0
  References2D = -> [ProjItem002]
  Rotation = 0
  ScaleType = 0
  TheoreticalExact = false
  Type = 1
  UnderTolerance = 0
  X = -33.2501
  Y = 46.0397
FEATURE [TechDraw::DrawViewDimension] Dimension085
  Arbitrary = false
  ArbitraryTolerances = false
  EqualTolerance = true
  FormatSpec = %.2f
  FormatSpecOverTolerance = %+.2f
  FormatSpecUnderTolerance = %+.2f
  Inverted = false
  LockPosition = false
  MeasureType = 1
  OverTolerance = 0
  References2D = -> [ProjItem002]
  Rotation = 0
  ScaleType = 0
  TheoreticalExact = false
  Type = 1
  UnderTolerance = 0
  X = -11.7501
  Y = 46.1166
FEATURE [TechDraw::DrawViewDimension] Dimension086
  Arbitrary = false
  ArbitraryTolerances = false
  EqualTolerance = true
  FormatSpec = %.2f
  FormatSpecOverTolerance = %+.2f
  FormatSpecUnderTolerance = %+.2f
  Inverted = false
  LockPosition = false
  MeasureType = 1
  OverTolerance = 0
  References2D = -> [ProjItem002]
  Rotation = 0
  ScaleType = 0
  TheoreticalExact = false
  Type = 2
  UnderTolerance = 0
  X = -64.8755
  Y = 0.957114
FEATURE [TechDraw::DrawViewDimension] Dimension087
  Arbitrary = false
  ArbitraryTolerances = false
  EqualTolerance = true
  FormatSpec = %.2f
  FormatSpecOverTolerance = %+.2f
  FormatSpecUnderTolerance = %+.2f
  Inverted = false
  LockPosition = false
  MeasureType = 1
  OverTolerance = 0
  References2D = -> [ProjItem002]
  Rotation = 0
  ScaleType = 0
  TheoreticalExact = false
  Type = 2
  UnderTolerance = 0
  X = -64.739
  Y = 35.2339
FEATURE [TechDraw::DrawViewDimension] Dimension088
  Arbitrary = false
  ArbitraryTolerances = false
  EqualTolerance = true
  FormatSpec = %.2f
  FormatSpecOverTolerance = %+.2f
  FormatSpecUnderTolerance = %+.2f
  Inverted = false
  LockPosition = false
  MeasureType = 1
  OverTolerance = 0
  References2D = -> [ProjItem002]
  Rotation = 0
  ScaleType = 0
  TheoreticalExact = false
  Type = 1
  UnderTolerance = 0
  X = 5.04608
  Y = 6.55439
FEATURE [TechDraw::DrawViewDimension] Dimension089
  Arbitrary = false
  ArbitraryTolerances = false
  EqualTolerance = true
  FormatSpec = %.2f
  FormatSpecOverTolerance = %+.2f
  FormatSpecUnderTolerance = %+.2f
  Inverted = false
  LockPosition = false
  MeasureType = 1
  OverTolerance = 0
  References2D = -> [ProjItem002]
  Rotation = 0
  ScaleType = 0
  TheoreticalExact = false
  Type = 2
  UnderTolerance = 0
  X = 18.1287
  Y = 1.14854
FEATURE [TechDraw::DrawViewDimension] Dimension090
  Arbitrary = false
  ArbitraryTolerances = false
  EqualTolerance = true
  FormatSpec = %.2f
  FormatSpecOverTolerance = %+.2f
  FormatSpecUnderTolerance = %+.2f
  Inverted = false
  LockPosition = false
  MeasureType = 1
  OverTolerance = 0
  References2D = -> [ProjItem002]
  Rotation = 0
  ScaleType = 0
  TheoreticalExact = false
  Type = 1
  UnderTolerance = 0
  X = -28.1041
  Y = 19.4684
FEATURE [TechDraw::DrawViewDimension] Dimension091
  Arbitrary = false
  ArbitraryTolerances = false
  EqualTolerance = true
  FormatSpec = 16x ⌀%.2f
  FormatSpecOverTolerance = %+.2f
  FormatSpecUnderTolerance = %+.2f
  Inverted = false
  LockPosition = false
  MeasureType = 1
  OverTolerance = 0
  References2D = -> [ProjItem002]
  Rotation = 0
  ScaleType = 0
  TheoreticalExact = false
  Type = 5
  UnderTolerance = 0
  X = 16.4834
  Y = -17.0901
FEATURE [TechDraw::DrawViewDimension] Dimension092
  Arbitrary = false
  ArbitraryTolerances = false
  EqualTolerance = true
  FormatSpec = 16x ⌀%.2f ↓8.0
  FormatSpecOverTolerance = %+.2f
  FormatSpecUnderTolerance = %+.2f
  Inverted = false
  LockPosition = false
  MeasureType = 1
  OverTolerance = 0
  References2D = -> [ProjItem002]
  Rotation = 0
  ScaleType = 0
  TheoreticalExact = false
  Type = 5
  UnderTolerance = 0
  X = 26.3139
  Y = -25.0268
FEATURE [TechDraw::DrawViewDimension] Dimension093
  Arbitrary = true
  ArbitraryTolerances = false
  EqualTolerance = true
  FormatSpec = 6x 1/4-20
  FormatSpecOverTolerance = %+.2f
  FormatSpecUnderTolerance = %+.2f
  Inverted = false
  LockPosition = false
  MeasureType = 1
  OverTolerance = 0
  References2D = -> [ProjItem002]
  Rotation = 0
  ScaleType = 0
  TheoreticalExact = false
  Type = 4
  UnderTolerance = 0
  X = -31.2391
  Y = -15.819
FEATURE [TechDraw::DrawViewDimension] Dimension094
  Arbitrary = false
  ArbitraryTolerances = false
  EqualTolerance = true
  FormatSpec = 4x ⌀%.2f
  FormatSpecOverTolerance = %+.2f
  FormatSpecUnderTolerance = %+.2f
  Inverted = false
  LockPosition = false
  MeasureType = 1
  OverTolerance = 0
  References2D = -> [ProjItem002]
  Rotation = 0
  ScaleType = 0
  TheoreticalExact = false
  Type = 5
  UnderTolerance = 0
  X = -11.6981
  Y = 3.58918
FEATURE [TechDraw::DrawViewDimension] Dimension095
  Arbitrary = false
  ArbitraryTolerances = false
  EqualTolerance = true
  FormatSpec = 4x ⌀%.2f ↓8.0
  FormatSpecOverTolerance = %+.2f
  FormatSpecUnderTolerance = %+.2f
  Inverted = false
  LockPosition = false
  MeasureType = 1
  OverTolerance = 0
  References2D = -> [ProjItem002]
  Rotation = 0
  ScaleType = 0
  TheoreticalExact = false
  Type = 5
  UnderTolerance = 0
  X = -21.1363
  Y = -1.99399
FEATURE [TechDraw::DrawPage] Page005  label="Front plate"
  KeepUpdated = true
  NextBalloonIndex = 1
  ProjectionType = 0
  Template = -> Template005
  Views = -> [ProjGroup001,Dimension072,Dimension073,Dimension074,Dimension075,Dimension076,Dimension077,Dimension078,Dimension079,Dimension080,Dimension081,Dimension082,Dimension083,Dimension084,Dimension085,Dimension086,Dimension087,Dimension088,Dimension089,Dimension090,Dimension091,Dimension092,Dimension093,Dimension094,Dimension095]
FEATURE [TechDraw::DrawViewPart] View005  label="Top "
  CoarseView = false
  Direction = (0,0,1)
  Focus = 100
  HardHidden = false
  IsoCount = 0
  IsoHidden = false
  IsoVisible = false
  LockPosition = false
  Perspective = false
  Rotation = 0
  Scale = 0.5
  ScaleType = 0
  SeamHidden = false
  SeamVisible = true
  SmoothHidden = false
  SmoothVisible = true
  Source = -> [Body]
  X = 229.918
  XDirection = (0,1,0)
  Y = 138.352
FEATURE [TechDraw::DrawViewDimension] Dimension096
  Arbitrary = false
  ArbitraryTolerances = false
  EqualTolerance = true
  FormatSpec = %.2f
  FormatSpecOverTolerance = %+.2f
  FormatSpecUnderTolerance = %+.2f
  Inverted = false
  LockPosition = false
  MeasureType = 1
  OverTolerance = 0
  References2D = -> [View005]
  Rotation = 0
  ScaleType = 0
  TheoreticalExact = false
  Type = 2
  UnderTolerance = 0
  X = 8.05524
  Y = 47.1342
FEATURE [TechDraw::DrawViewDimension] Dimension097
  Arbitrary = false
  ArbitraryTolerances = false
  EqualTolerance = true
  FormatSpec = %.2f
  FormatSpecOverTolerance = %+.2f
  FormatSpecUnderTolerance = %+.2f
  Inverted = false
  LockPosition = false
  MeasureType = 1
  OverTolerance = 0
  References2D = -> [View005]
  Rotation = 0
  ScaleType = 0
  TheoreticalExact = false
  Type = 2
  UnderTolerance = 0
  X = 11.9639
  Y = 18.6707
FEATURE [TechDraw::DrawPage] Page002  label="Back plate"
  KeepUpdated = true
  NextBalloonIndex = 1
  ProjectionType = 0
  Template = -> Template002
  Views = -> [View002,Dimension030,Dimension031,Dimension032,Dimension033,Dimension034,Dimension035,Dimension036,Dimension037,Dimension038,Dimension039,Dimension040,Dimension041,Dimension042,Dimension043,Dimension044,Dimension045,Dimension046,Dimension047,Dimension048,Dimension049,Dimension050,Dimension051,Dimension052,Dimension053,Dimension054,Dimension055,Dimension056,Dimension057,Dimension058,View003,+6 more]
FEATURE [App::DocumentObjectGroup] Group002  label="Drawings"
  ExportMode = 1
  Group = -> [Page,Page001,Page002,Page003,Page004,Page005]
  _GroupVersion = 1
FEATURE [Part::FeaturePython] Assembly  label="Backplate-Assembly"  # WARN: FeaturePython — macro-defined, semantics opaque (R4)
  AutoRelax = true
  BuildShape = 0
  Freeze = false
  Group = -> [Constraints,Elements,Parts]
  Verbose = false
  _LinkVersion = 1
  _SolverType = 1
  _Version = 1
FEATURE [App::FeaturePython] Constraints  # WARN: FeaturePython — macro-defined, semantics opaque (R4)
  Group = -> [Constraint,Constraint006,Constraint007,Constraint008,Constraint009,Constraint010,Constraint011,Constraint012,Constraint013,Constraint014,Constraint015,Constraint016,Constraint017,Constraint018,Constraint019,Constraint020,Constraint021,Constraint022,Constraint023,Constraint024,Constraint025,Constraint052,Constraint053]
  _LinkVersion = 1
  _Version = 1
FEATURE [App::FeaturePython] Elements  # WARN: FeaturePython — macro-defined, semantics opaque (R4)
  Group = -> [Element,Element001,Element002,Element039,Element040,Element041,Element046,Element047,Element048,_Element,_Element001,_Element002,_Element003,_Element004,_Element005,_Element006,_Element007,_Element008,_Element009,_Element010,_Element011,_Element012,_Element013,_Element014,_Element015,_Element016,_Element017,_Element018,_Element019,_Element020,_Element021,_Element022,_Element023,_Element024,+18 more]
  _LinkVersion = 1
FEATURE [Part::FeaturePython] Element  label="rail-tr"  # link proxy (typed FeaturePython)
  Detach = false
  LinkTransform = true
  LinkedObject = -> Link [Pocket001.Edge44]
  _LinkVersion = 1
  _Parent = -> Elements
FEATURE [Part::FeaturePython] Element001  label="rail-tl"  # link proxy (typed FeaturePython)
  Detach = false
  LinkTransform = true
  LinkedObject = -> Link [Pocket001.Edge34]
  _LinkVersion = 1
  _Parent = -> Elements
FEATURE [Part::FeaturePython] Element002  label="screw-br"  # link proxy (typed FeaturePython)
  Detach = false
  LinkTransform = true
  LinkedObject = -> Link [Pocket001.Sketch002.Edge2]
  Offset = pos=(0,0,15.7) rot=(0,0,1;0rad)
  Placement = pos=(0,-15.7,1.42e-14) rot=(0,0,1;0rad)
  _LinkVersion = 1
  _Parent = -> Elements
FEATURE [Part::FeaturePython] Assembly001  label="Frontplate-Assembly"  # WARN: FeaturePython — macro-defined, semantics opaque (R4)
  AutoRelax = true
  BuildShape = 0
  Freeze = false
  Group = -> [Constraints001,Elements001,Parts001]
  Verbose = false
  _LinkVersion = 1
  _SolverType = 1
  _Version = 1
FEATURE [App::FeaturePython] Constraints001  # WARN: FeaturePython — macro-defined, semantics opaque (R4)
  Group = -> [Constraint002,Constraint030,Constraint031,Constraint032,Constraint033,Constraint034,Constraint035,Constraint036,Constraint037,Constraint038,Constraint039,Constraint040,Constraint041,Constraint042,Constraint043,Constraint044,Constraint045,Constraint046,Constraint047,Constraint048,Constraint049,Constraint054,Constraint055,Constraint056]
  _LinkVersion = 1
  _Version = 1
FEATURE [App::FeaturePython] Elements001  # WARN: FeaturePython — macro-defined, semantics opaque (R4)
  Group = -> [Element027,Element028,Element032,Element033,Element036,Element045,_Element048,_Element049,_Element050,_Element051,_Element052,_Element053,_Element054,_Element055,_Element056,_Element057,_Element058,_Element059,_Element060,_Element061,_Element062,_Element063,_Element064,_Element065,_Element066,_Element067,_Element068,_Element069,_Element070,_Element071,_Element072,_Element073,_Element074,+18 more]
  _LinkVersion = 1
FEATURE [Part::FeaturePython] Assembly002  label="Shim-Assembly"  # WARN: FeaturePython — macro-defined, semantics opaque (R4)
  AutoRelax = true
  BuildShape = 0
  Freeze = false
  Group = -> [Constraints002,Elements002,Parts002]
  Verbose = false
  _LinkVersion = 1
  _SolverType = 1
  _Version = 1
FEATURE [App::FeaturePython] Constraints002  # WARN: FeaturePython — macro-defined, semantics opaque (R4)
  Group = -> [Constraint003]
  _LinkVersion = 1
  _Version = 1
FEATURE [App::FeaturePython] Elements002  # WARN: FeaturePython — macro-defined, semantics opaque (R4)
  Group = -> [Element003,Element004,Element005,Element006]
  _LinkVersion = 1
FEATURE [Part::FeaturePython] Element003  label="front-tl"  # link proxy (typed FeaturePython)
  Detach = false
  LinkTransform = true
  LinkedObject = -> Link001 [Pad002.Edge24]
  _LinkVersion = 1
  _Parent = -> Elements002
FEATURE [Part::FeaturePython] Element004  label="front-bl"  # link proxy (typed FeaturePython)
  Detach = false
  LinkTransform = true
  LinkedObject = -> Link001 [Pad002.Edge18]
  _LinkVersion = 1
  _Parent = -> Elements002
FEATURE [Part::FeaturePython] Element005  label="cart-tl"  # link proxy (typed FeaturePython)
  Detach = false
  LinkTransform = true
  LinkedObject = -> Link001 [Pad002.Edge23]
  _LinkVersion = 1
  _Parent = -> Elements002
FEATURE [Part::FeaturePython] Element006  label="cart-bl"  # link proxy (typed FeaturePython)
  Detach = false
  LinkTransform = true
  LinkedObject = -> Link001 [Pad002.Edge17]
  _LinkVersion = 1
  _Parent = -> Elements002
FEATURE [App::FeaturePython] Constraint  label="Locked"  # WARN: FeaturePython — macro-defined, semantics opaque (R4)
  Disabled = false
  Group = -> [ElementLink]
  _ConstraintType = 0
  _LinkVersion = 1
  _Parent = -> Constraints
FEATURE [App::FeaturePython] ElementLink  label="rail-tr"  # link proxy (typed FeaturePython)
  LinkTransform = true
  LinkedObject = -> Element
  _LinkVersion = 1
  _Parent = -> Constraint
FEATURE [Part::FeaturePython] Element027  label="shim-t-l"  # link proxy (typed FeaturePython)
  Detach = false
  LinkTransform = true
  LinkedObject = -> Link002 [Pocket003.Edge21]
  _LinkVersion = 1
  _Parent = -> Elements001
FEATURE [Part::FeaturePython] Element028  label="shim-b-l"  # link proxy (typed FeaturePython)
  Detach = false
  LinkTransform = true
  LinkedObject = -> Link002 [Pocket003.Edge13]
  _LinkVersion = 1
  _Parent = -> Elements001
FEATURE [Part::FeaturePython] Element032  label="shim-b-r"  # link proxy (typed FeaturePython)
  Detach = false
  LinkTransform = true
  LinkedObject = -> Link002 [Pocket003.Edge29]
  _LinkVersion = 1
  _Parent = -> Elements001
FEATURE [Part::FeaturePython] Element033  label="shim-t-r"  # link proxy (typed FeaturePython)
  Detach = false
  LinkTransform = true
  LinkedObject = -> Link002 [Pocket003.Edge37]
  _LinkVersion = 1
  _Parent = -> Elements001
FEATURE [Part::FeaturePython] Assembly003  label="Nut-shim-Assembly"  # WARN: FeaturePython — macro-defined, semantics opaque (R4)
  AutoRelax = true
  BuildShape = 0
  Freeze = false
  Group = -> [Constraints003,Elements003,Parts003]
  Verbose = false
  _LinkVersion = 1
  _SolverType = 1
  _Version = 1
FEATURE [App::FeaturePython] Constraints003  # WARN: FeaturePython — macro-defined, semantics opaque (R4)
  Group = -> [Constraint001]
  _LinkVersion = 1
  _Version = 1
FEATURE [App::FeaturePython] Elements003  # WARN: FeaturePython — macro-defined, semantics opaque (R4)
  Group = -> [Element034,Element035]
  _LinkVersion = 1
FEATURE [Part::FeaturePython] Element034  label="fp-mate"  # link proxy (typed FeaturePython)
  Detach = false
  LinkTransform = true
  LinkedObject = -> Link003 [Pad003.Edge18]
  _LinkVersion = 1
  _Parent = -> Elements003
FEATURE [Part::FeaturePython] Element035  label="nut-mate"  # link proxy (typed FeaturePython)
  Detach = false
  LinkTransform = true
  LinkedObject = -> Link003 [Pad003.Edge20]
  _LinkVersion = 1
  _Parent = -> Elements003
FEATURE [Part::FeaturePython] Element036  label="shim-nut-mate"  # link proxy (typed FeaturePython)
  Detach = false
  LinkTransform = true
  LinkedObject = -> Link002 [Hole001.Sketch005.Edge4]
  Offset = pos=(0,0,-15.7) rot=(0,0,1;0rad)
  Placement = pos=(0,15.7,-7.1e-15) rot=(0,0,1;0rad)
  _LinkVersion = 1
  _Parent = -> Elements001
FEATURE [Part::FeaturePython] Assembly004  label="Motor Bracket Assembly"  # WARN: FeaturePython — macro-defined, semantics opaque (R4)
  AutoRelax = true
  BuildShape = 0
  Freeze = false
  Group = -> [Constraints004,Elements004,Parts004]
  Verbose = false
  _LinkVersion = 1
  _SolverType = 1
  _Version = 1
FEATURE [App::FeaturePython] Constraints004  # WARN: FeaturePython — macro-defined, semantics opaque (R4)
  Group = -> [Constraint004,Constraint026,Constraint027,Constraint028,Constraint029]
  _LinkVersion = 1
  _Version = 1
FEATURE [App::FeaturePython] Elements004  # WARN: FeaturePython — macro-defined, semantics opaque (R4)
  Group = -> [Element037,Element038,_Element040,_Element041,_Element042,_Element043,_Element044,_Element045,_Element046,_Element047,Element052]
  _LinkVersion = 1
FEATURE [Part::FeaturePython] Element037  label="Motor-mate"  # link proxy (typed FeaturePython)
  Detach = false
  LinkTransform = true
  LinkedObject = -> Link004 [Pad004.Edge15]
  _LinkVersion = 1
  _Parent = -> Elements004
FEATURE [Part::FeaturePython] Element038  label="bp-mate"  # link proxy (typed FeaturePython)
  Detach = false
  LinkTransform = true
  LinkedObject = -> Link004 [Pad004.Edge23]
  _LinkVersion = 1
  _Parent = -> Elements004
FEATURE [Part::FeaturePython] Element039  label="bracket-mate"  # link proxy (typed FeaturePython)
  Detach = false
  LinkTransform = true
  LinkedObject = -> Link [Pocket002.Edge7]
  _LinkVersion = 1
  _Parent = -> Elements
FEATURE [Part::FeaturePython] Element040  label="x-cart-bl"  # link proxy (typed FeaturePython)
  Detach = false
  LinkTransform = true
  LinkedObject = -> Link [Hole004.Edge18]
  _LinkVersion = 1
  _Parent = -> Elements
FEATURE [Part::FeaturePython] Element041  label="x-cart-br"  # link proxy (typed FeaturePython)
  Detach = false
  LinkTransform = true
  LinkedObject = -> Link [Hole004.Edge33]
  _LinkVersion = 1
  _Parent = -> Elements
FEATURE [Part::FeaturePython] Element045  label="spindle-65mm-tl"  # link proxy (typed FeaturePython)
  Detach = false
  LinkTransform = true
  LinkedObject = -> Link002 [Pocket003.Edge40]
  _LinkVersion = 1
  _Parent = -> Elements001
FEATURE [Part::FeaturePython] Element046  label="x-cart-tl"  # link proxy (typed FeaturePython)
  Detach = false
  LinkTransform = true
  LinkedObject = -> Link [Hole004.Edge29]
  _LinkVersion = 1
  _Parent = -> Elements
FEATURE [Part::FeaturePython] Element047  label="x-cart-tr"  # link proxy (typed FeaturePython)
  Detach = false
  LinkTransform = true
  LinkedObject = -> Link [Hole004.Edge42]
  _LinkVersion = 1
  _Parent = -> Elements
FEATURE [App::FeaturePython] Constraint001  label="Locked001"  # WARN: FeaturePython — macro-defined, semantics opaque (R4)
  Disabled = false
  Group = -> [ElementLink001]
  _ConstraintType = 0
  _LinkVersion = 1
  _Parent = -> Constraints003
FEATURE [App::FeaturePython] ElementLink001  label="fp-mate"  # link proxy (typed FeaturePython)
  LinkTransform = true
  LinkedObject = -> Element034
  _LinkVersion = 1
  _Parent = -> Constraint001
FEATURE [Part::FeaturePython] Element048  label="x-nut-mate"  # link proxy (typed FeaturePython)
  Detach = false
  LinkTransform = true
  LinkedObject = -> Link [Hole004.Edge22]
  _LinkVersion = 1
  _Parent = -> Elements
FEATURE [App::DocumentObjectGroup] Group001  label="Assemblies"
  ExportMode = 1
  Group = -> [Assembly,Assembly001,Assembly002,Assembly003,Assembly004,Assembly005]
  _GroupVersion = 1
FEATURE [App::FeaturePython] Constraint002  label="Locked002"  # WARN: FeaturePython — macro-defined, semantics opaque (R4)
  Disabled = false
  Group = -> [ElementLink002]
  _ConstraintType = 0
  _LinkVersion = 1
  _Parent = -> Constraints001
FEATURE [App::FeaturePython] ElementLink002  label="shim-nut-mate"  # link proxy (typed FeaturePython)
  LinkTransform = true
  LinkedObject = -> Element036
  _LinkVersion = 1
  _Parent = -> Constraint002
FEATURE [App::FeaturePython] Constraint003  label="Locked003"  # WARN: FeaturePython — macro-defined, semantics opaque (R4)
  Disabled = false
  Group = -> [ElementLink003]
  _ConstraintType = 0
  _LinkVersion = 1
  _Parent = -> Constraints002
FEATURE [App::FeaturePython] ElementLink003  label="front-tl"  # link proxy (typed FeaturePython)
  LinkTransform = true
  LinkedObject = -> Element003
  _LinkVersion = 1
  _Parent = -> Constraint003
FEATURE [App::FeaturePython] Constraint004  label="Locked004"  # WARN: FeaturePython — macro-defined, semantics opaque (R4)
  Disabled = false
  Group = -> [ElementLink004]
  _ConstraintType = 0
  _LinkVersion = 1
  _Parent = -> Constraints004
FEATURE [App::FeaturePython] ElementLink004  label="Motor-mate"  # link proxy (typed FeaturePython)
  LinkTransform = true
  LinkedObject = -> Element037
  _LinkVersion = 1
  _Parent = -> Constraint004
FEATURE [Part::FeaturePython] Assembly005  label="Nut-shim-X-Assembly"  # WARN: FeaturePython — macro-defined, semantics opaque (R4)
  AutoRelax = true
  BuildShape = 0
  Freeze = false
  Group = -> [Constraints005,Elements005,Parts005]
  Verbose = false
  _LinkVersion = 1
  _SolverType = 1
  _Version = 1
FEATURE [App::FeaturePython] Constraints005  # WARN: FeaturePython — macro-defined, semantics opaque (R4)
  Group = -> [Constraint005]
  _LinkVersion = 1
  _Version = 1
FEATURE [App::FeaturePython] Elements005  # WARN: FeaturePython — macro-defined, semantics opaque (R4)
  Group = -> [Element049,Element050]
  _LinkVersion = 1
FEATURE [Part::FeaturePython] Element049  label="bp-mate"  # link proxy (typed FeaturePython)
  Detach = false
  LinkTransform = true
  LinkedObject = -> Link005 [Pad005.Edge20]
  _LinkVersion = 1
  _Parent = -> Elements005
FEATURE [Part::FeaturePython] Element050  label="nut-mate"  # link proxy (typed FeaturePython)
  Detach = false
  LinkTransform = true
  LinkedObject = -> Link005 [Pad005.Edge21]
  _LinkVersion = 1
  _Parent = -> Elements005
FEATURE [App::FeaturePython] Constraint005  label="Locked005"  # WARN: FeaturePython — macro-defined, semantics opaque (R4)
  Disabled = false
  Group = -> [ElementLink005]
  _ConstraintType = 0
  _LinkVersion = 1
  _Parent = -> Constraints005
FEATURE [App::FeaturePython] ElementLink005  label="nut-mate"  # link proxy (typed FeaturePython)
  LinkTransform = true
  LinkedObject = -> Element050
  _LinkVersion = 1
  _Parent = -> Constraint005
FEATURE [App::FeaturePython] Constraint006  label="Attachment"  # WARN: FeaturePython — macro-defined, semantics opaque (R4)
  Cascade = false
  Disabled = false
  Group = -> [ElementLink006,ElementLink007]
  Multiply = false
  _ConstraintType = 45
  _LinkVersion = 1
  _Parent = -> Constraints
FEATURE [App::FeaturePython] ElementLink006  label="_Element"  # link proxy (typed FeaturePython)
  LinkTransform = true
  LinkedObject = -> _Element
  _LinkVersion = 1
  _Parent = -> Constraint006
FEATURE [Part::FeaturePython] _Element  # link proxy (typed FeaturePython)
  Detach = false
  LinkTransform = true
  LinkedObject = -> Link006 [0.Edge9]
  _LinkVersion = 1
  _Parent = -> Elements
FEATURE [App::FeaturePython] ElementLink007  label="_Element001"  # link proxy (typed FeaturePython)
  LinkTransform = true
  LinkedObject = -> _Element001
  _LinkVersion = 1
  _Parent = -> Constraint006
FEATURE [Part::FeaturePython] _Element001  # link proxy (typed FeaturePython)
  Detach = false
  LinkTransform = true
  LinkedObject = -> Link [Hole004.Edge115]
  _LinkVersion = 1
  _Parent = -> Elements
FEATURE [App::FeaturePython] Constraint007  label="Attachment001"  # WARN: FeaturePython — macro-defined, semantics opaque (R4)
  Cascade = false
  Disabled = false
  Group = -> [ElementLink008,ElementLink009]
  Multiply = false
  _ConstraintType = 45
  _LinkVersion = 1
  _Parent = -> Constraints
FEATURE [App::FeaturePython] ElementLink008  label="_Element002"  # link proxy (typed FeaturePython)
  LinkTransform = true
  LinkedObject = -> _Element002
  _LinkVersion = 1
  _Parent = -> Constraint007
FEATURE [Part::FeaturePython] _Element002  # link proxy (typed FeaturePython)
  Detach = false
  LinkTransform = true
  LinkedObject = -> Link006 [1.Edge9]
  _LinkVersion = 1
  _Parent = -> Elements
FEATURE [App::FeaturePython] ElementLink009  label="_Element003"  # link proxy (typed FeaturePython)
  LinkTransform = true
  LinkedObject = -> _Element003
  _LinkVersion = 1
  _Parent = -> Constraint007
FEATURE [Part::FeaturePython] _Element003  # link proxy (typed FeaturePython)
  Detach = false
  LinkTransform = true
  LinkedObject = -> Link [Hole004.Edge122]
  _LinkVersion = 1
  _Parent = -> Elements
FEATURE [App::FeaturePython] Constraint008  label="Attachment002"  # WARN: FeaturePython — macro-defined, semantics opaque (R4)
  Cascade = false
  Disabled = false
  Group = -> [ElementLink010,ElementLink011]
  Multiply = false
  _ConstraintType = 45
  _LinkVersion = 1
  _Parent = -> Constraints
FEATURE [App::FeaturePython] ElementLink010  label="_Element004"  # link proxy (typed FeaturePython)
  LinkTransform = true
  LinkedObject = -> _Element004
  _LinkVersion = 1
  _Parent = -> Constraint008
FEATURE [Part::FeaturePython] _Element004  # link proxy (typed FeaturePython)
  Detach = false
  LinkTransform = true
  LinkedObject = -> Link006 [11.Edge9]
  _LinkVersion = 1
  _Parent = -> Elements
FEATURE [App::FeaturePython] ElementLink011  label="_Element005"  # link proxy (typed FeaturePython)
  LinkTransform = true
  LinkedObject = -> _Element005
  _LinkVersion = 1
  _Parent = -> Constraint008
FEATURE [Part::FeaturePython] _Element005  # link proxy (typed FeaturePython)
  Detach = false
  LinkTransform = true
  LinkedObject = -> Link [Hole004.Edge120]
  _LinkVersion = 1
  _Parent = -> Elements
FEATURE [App::FeaturePython] Constraint009  label="Attachment003"  # WARN: FeaturePython — macro-defined, semantics opaque (R4)
  Cascade = false
  Disabled = false
  Group = -> [ElementLink012,ElementLink013]
  Multiply = false
  _ConstraintType = 45
  _LinkVersion = 1
  _Parent = -> Constraints
FEATURE [App::FeaturePython] ElementLink012  label="_Element006"  # link proxy (typed FeaturePython)
  LinkTransform = true
  LinkedObject = -> _Element006
  _LinkVersion = 1
  _Parent = -> Constraint009
FEATURE [Part::FeaturePython] _Element006  # link proxy (typed FeaturePython)
  Detach = false
  LinkTransform = true
  LinkedObject = -> Link006 [2.Edge9]
  _LinkVersion = 1
  _Parent = -> Elements
FEATURE [App::FeaturePython] ElementLink013  label="_Element007"  # link proxy (typed FeaturePython)
  LinkTransform = true
  LinkedObject = -> _Element007
  _LinkVersion = 1
  _Parent = -> Constraint009
FEATURE [Part::FeaturePython] _Element007  # link proxy (typed FeaturePython)
  Detach = false
  LinkTransform = true
  LinkedObject = -> Link [Hole004.Edge113]
  _LinkVersion = 1
  _Parent = -> Elements
FEATURE [App::FeaturePython] Constraint010  label="Attachment004"  # WARN: FeaturePython — macro-defined, semantics opaque (R4)
  Cascade = false
  Disabled = false
  Group = -> [ElementLink014,ElementLink015]
  Multiply = false
  _ConstraintType = 45
  _LinkVersion = 1
  _Parent = -> Constraints
FEATURE [App::FeaturePython] ElementLink014  label="_Element008"  # link proxy (typed FeaturePython)
  LinkTransform = true
  LinkedObject = -> _Element008
  _LinkVersion = 1
  _Parent = -> Constraint010
FEATURE [Part::FeaturePython] _Element008  # link proxy (typed FeaturePython)
  Detach = false
  LinkTransform = true
  LinkedObject = -> Link006 [3.Edge9]
  _LinkVersion = 1
  _Parent = -> Elements
FEATURE [App::FeaturePython] ElementLink015  label="_Element009"  # link proxy (typed FeaturePython)
  LinkTransform = true
  LinkedObject = -> _Element009
  _LinkVersion = 1
  _Parent = -> Constraint010
FEATURE [Part::FeaturePython] _Element009  # link proxy (typed FeaturePython)
  Detach = false
  LinkTransform = true
  LinkedObject = -> Link [Hole004.Edge143]
  _LinkVersion = 1
  _Parent = -> Elements
FEATURE [App::FeaturePython] Constraint011  label="Attachment005"  # WARN: FeaturePython — macro-defined, semantics opaque (R4)
  Cascade = false
  Disabled = false
  Group = -> [ElementLink016,ElementLink017]
  Multiply = false
  _ConstraintType = 45
  _LinkVersion = 1
  _Parent = -> Constraints
FEATURE [App::FeaturePython] ElementLink016  label="_Element010"  # link proxy (typed FeaturePython)
  LinkTransform = true
  LinkedObject = -> _Element010
  _LinkVersion = 1
  _Parent = -> Constraint011
FEATURE [Part::FeaturePython] _Element010  # link proxy (typed FeaturePython)
  Detach = false
  LinkTransform = true
  LinkedObject = -> Link006 [12.Edge9]
  _LinkVersion = 1
  _Parent = -> Elements
FEATURE [App::FeaturePython] ElementLink017  label="_Element011"  # link proxy (typed FeaturePython)
  LinkTransform = true
  LinkedObject = -> _Element011
  _LinkVersion = 1
  _Parent = -> Constraint011
FEATURE [Part::FeaturePython] _Element011  # link proxy (typed FeaturePython)
  Detach = false
  LinkTransform = true
  LinkedObject = -> Link [Hole004.Edge150]
  _LinkVersion = 1
  _Parent = -> Elements
FEATURE [App::FeaturePython] Constraint012  label="Attachment006"  # WARN: FeaturePython — macro-defined, semantics opaque (R4)
  Cascade = false
  Disabled = false
  Group = -> [ElementLink018,ElementLink019]
  Multiply = false
  _ConstraintType = 45
  _LinkVersion = 1
  _Parent = -> Constraints
FEATURE [App::FeaturePython] ElementLink018  label="_Element012"  # link proxy (typed FeaturePython)
  LinkTransform = true
  LinkedObject = -> _Element012
  _LinkVersion = 1
  _Parent = -> Constraint012
FEATURE [Part::FeaturePython] _Element012  # link proxy (typed FeaturePython)
  Detach = false
  LinkTransform = true
  LinkedObject = -> Link006 [13.Edge9]
  _LinkVersion = 1
  _Parent = -> Elements
FEATURE [App::FeaturePython] ElementLink019  label="_Element013"  # link proxy (typed FeaturePython)
  LinkTransform = true
  LinkedObject = -> _Element013
  _LinkVersion = 1
  _Parent = -> Constraint012
FEATURE [Part::FeaturePython] _Element013  # link proxy (typed FeaturePython)
  Detach = false
  LinkTransform = true
  LinkedObject = -> Link [Hole004.Edge141]
  _LinkVersion = 1
  _Parent = -> Elements
FEATURE [App::FeaturePython] Constraint013  label="Attachment007"  # WARN: FeaturePython — macro-defined, semantics opaque (R4)
  Cascade = false
  Disabled = false
  Group = -> [ElementLink020,ElementLink021]
  Multiply = false
  _ConstraintType = 45
  _LinkVersion = 1
  _Parent = -> Constraints
FEATURE [App::FeaturePython] ElementLink020  label="_Element014"  # link proxy (typed FeaturePython)
  LinkTransform = true
  LinkedObject = -> _Element014
  _LinkVersion = 1
  _Parent = -> Constraint013
FEATURE [Part::FeaturePython] _Element014  # link proxy (typed FeaturePython)
  Detach = false
  LinkTransform = true
  LinkedObject = -> Link006 [4.Edge9]
  _LinkVersion = 1
  _Parent = -> Elements
FEATURE [App::FeaturePython] ElementLink021  label="_Element015"  # link proxy (typed FeaturePython)
  LinkTransform = true
  LinkedObject = -> _Element015
  _LinkVersion = 1
  _Parent = -> Constraint013
FEATURE [Part::FeaturePython] _Element015  # link proxy (typed FeaturePython)
  Detach = false
  LinkTransform = true
  LinkedObject = -> Link [Hole004.Edge148]
  _LinkVersion = 1
  _Parent = -> Elements
FEATURE [App::FeaturePython] Constraint014  label="Attachment008"  # WARN: FeaturePython — macro-defined, semantics opaque (R4)
  Cascade = false
  Disabled = false
  Group = -> [ElementLink022,ElementLink023]
  Multiply = false
  _ConstraintType = 45
  _LinkVersion = 1
  _Parent = -> Constraints
FEATURE [App::FeaturePython] ElementLink022  label="_Element016"  # link proxy (typed FeaturePython)
  LinkTransform = true
  LinkedObject = -> _Element016
  _LinkVersion = 1
  _Parent = -> Constraint014
FEATURE [Part::FeaturePython] _Element016  # link proxy (typed FeaturePython)
  Detach = false
  LinkTransform = true
  LinkedObject = -> Link006 [14.Edge9]
  _LinkVersion = 1
  _Parent = -> Elements
FEATURE [App::FeaturePython] ElementLink023  label="_Element017"  # link proxy (typed FeaturePython)
  LinkTransform = true
  LinkedObject = -> _Element017
  _LinkVersion = 1
  _Parent = -> Constraint014
FEATURE [Part::FeaturePython] _Element017  # link proxy (typed FeaturePython)
  Detach = false
  LinkTransform = true
  LinkedObject = -> Link [Hole004.Edge138]
  _LinkVersion = 1
  _Parent = -> Elements
FEATURE [App::FeaturePython] Constraint015  label="Attachment009"  # WARN: FeaturePython — macro-defined, semantics opaque (R4)
  Cascade = false
  Disabled = false
  Group = -> [ElementLink024,ElementLink025]
  Multiply = false
  _ConstraintType = 45
  _LinkVersion = 1
  _Parent = -> Constraints
FEATURE [App::FeaturePython] ElementLink024  label="_Element018"  # link proxy (typed FeaturePython)
  LinkTransform = true
  LinkedObject = -> _Element018
  _LinkVersion = 1
  _Parent = -> Constraint015
FEATURE [Part::FeaturePython] _Element018  # link proxy (typed FeaturePython)
  Detach = false
  LinkTransform = true
  LinkedObject = -> Link006 [5.Edge9]
  _LinkVersion = 1
  _Parent = -> Elements
FEATURE [App::FeaturePython] ElementLink025  label="_Element019"  # link proxy (typed FeaturePython)
  LinkTransform = true
  LinkedObject = -> _Element019
  _LinkVersion = 1
  _Parent = -> Constraint015
FEATURE [Part::FeaturePython] _Element019  # link proxy (typed FeaturePython)
  Detach = false
  LinkTransform = true
  LinkedObject = -> Link [Hole004.Edge129]
  _LinkVersion = 1
  _Parent = -> Elements
FEATURE [App::FeaturePython] Constraint016  label="Attachment010"  # WARN: FeaturePython — macro-defined, semantics opaque (R4)
  Cascade = false
  Disabled = false
  Group = -> [ElementLink026,ElementLink027]
  Multiply = false
  _ConstraintType = 45
  _LinkVersion = 1
  _Parent = -> Constraints
FEATURE [App::FeaturePython] ElementLink026  label="_Element020"  # link proxy (typed FeaturePython)
  LinkTransform = true
  LinkedObject = -> _Element020
  _LinkVersion = 1
  _Parent = -> Constraint016
FEATURE [Part::FeaturePython] _Element020  # link proxy (typed FeaturePython)
  Detach = false
  LinkTransform = true
  LinkedObject = -> Link006 [15.Edge9]
  _LinkVersion = 1
  _Parent = -> Elements
FEATURE [App::FeaturePython] ElementLink027  label="_Element021"  # link proxy (typed FeaturePython)
  LinkTransform = true
  LinkedObject = -> _Element021
  _LinkVersion = 1
  _Parent = -> Constraint016
FEATURE [Part::FeaturePython] _Element021  # link proxy (typed FeaturePython)
  Detach = false
  LinkTransform = true
  LinkedObject = -> Link [Hole004.Edge136]
  _LinkVersion = 1
  _Parent = -> Elements
FEATURE [App::FeaturePython] Constraint017  label="Attachment011"  # WARN: FeaturePython — macro-defined, semantics opaque (R4)
  Cascade = false
  Disabled = false
  Group = -> [ElementLink028,ElementLink029]
  Multiply = false
  _ConstraintType = 45
  _LinkVersion = 1
  _Parent = -> Constraints
FEATURE [App::FeaturePython] ElementLink028  label="_Element022"  # link proxy (typed FeaturePython)
  LinkTransform = true
  LinkedObject = -> _Element022
  _LinkVersion = 1
  _Parent = -> Constraint017
FEATURE [Part::FeaturePython] _Element022  # link proxy (typed FeaturePython)
  Detach = false
  LinkTransform = true
  LinkedObject = -> Link006 [6.Edge9]
  _LinkVersion = 1
  _Parent = -> Elements
FEATURE [App::FeaturePython] ElementLink029  label="_Element023"  # link proxy (typed FeaturePython)
  LinkTransform = true
  LinkedObject = -> _Element023
  _LinkVersion = 1
  _Parent = -> Constraint017
FEATURE [Part::FeaturePython] _Element023  # link proxy (typed FeaturePython)
  Detach = false
  LinkTransform = true
  LinkedObject = -> Link [Hole004.Edge107]
  _LinkVersion = 1
  _Parent = -> Elements
FEATURE [App::FeaturePython] Constraint018  label="Attachment012"  # WARN: FeaturePython — macro-defined, semantics opaque (R4)
  Cascade = false
  Disabled = false
  Group = -> [ElementLink030,ElementLink031]
  Multiply = false
  _ConstraintType = 45
  _LinkVersion = 1
  _Parent = -> Constraints
FEATURE [App::FeaturePython] ElementLink030  label="_Element024"  # link proxy (typed FeaturePython)
  LinkTransform = true
  LinkedObject = -> _Element024
  _LinkVersion = 1
  _Parent = -> Constraint018
FEATURE [Part::FeaturePython] _Element024  # link proxy (typed FeaturePython)
  Detach = false
  LinkTransform = true
  LinkedObject = -> Link006 [7.Edge9]
  _LinkVersion = 1
  _Parent = -> Elements
FEATURE [App::FeaturePython] ElementLink031  label="_Element025"  # link proxy (typed FeaturePython)
  LinkTransform = true
  LinkedObject = -> _Element025
  _LinkVersion = 1
  _Parent = -> Constraint018
FEATURE [Part::FeaturePython] _Element025  # link proxy (typed FeaturePython)
  Detach = false
  LinkTransform = true
  LinkedObject = -> Link [Hole004.Edge100]
  _LinkVersion = 1
  _Parent = -> Elements
FEATURE [App::FeaturePython] Constraint019  label="Attachment013"  # WARN: FeaturePython — macro-defined, semantics opaque (R4)
  Cascade = false
  Disabled = false
  Group = -> [ElementLink032,ElementLink033]
  Multiply = false
  _ConstraintType = 45
  _LinkVersion = 1
  _Parent = -> Constraints
FEATURE [App::FeaturePython] ElementLink032  label="_Element026"  # link proxy (typed FeaturePython)
  LinkTransform = true
  LinkedObject = -> _Element026
  _LinkVersion = 1
  _Parent = -> Constraint019
FEATURE [Part::FeaturePython] _Element026  # link proxy (typed FeaturePython)
  Detach = false
  LinkTransform = true
  LinkedObject = -> Link006 [8.Edge9]
  _LinkVersion = 1
  _Parent = -> Elements
FEATURE [App::FeaturePython] ElementLink033  label="_Element027"  # link proxy (typed FeaturePython)
  LinkTransform = true
  LinkedObject = -> _Element027
  _LinkVersion = 1
  _Parent = -> Constraint019
FEATURE [Part::FeaturePython] _Element027  # link proxy (typed FeaturePython)
  Detach = false
  LinkTransform = true
  LinkedObject = -> Link [Hole004.Edge127]
  _LinkVersion = 1
  _Parent = -> Elements
FEATURE [App::FeaturePython] Constraint020  label="Attachment014"  # WARN: FeaturePython — macro-defined, semantics opaque (R4)
  Cascade = false
  Disabled = false
  Group = -> [ElementLink034,ElementLink035]
  Multiply = false
  _ConstraintType = 45
  _LinkVersion = 1
  _Parent = -> Constraints
FEATURE [App::FeaturePython] ElementLink034  label="_Element028"  # link proxy (typed FeaturePython)
  LinkTransform = true
  LinkedObject = -> _Element028
  _LinkVersion = 1
  _Parent = -> Constraint020
FEATURE [Part::FeaturePython] _Element028  # link proxy (typed FeaturePython)
  Detach = false
  LinkTransform = true
  LinkedObject = -> Link006 [9.Edge9]
  _LinkVersion = 1
  _Parent = -> Elements
FEATURE [App::FeaturePython] ElementLink035  label="_Element029"  # link proxy (typed FeaturePython)
  LinkTransform = true
  LinkedObject = -> _Element029
  _LinkVersion = 1
  _Parent = -> Constraint020
FEATURE [Part::FeaturePython] _Element029  # link proxy (typed FeaturePython)
  Detach = false
  LinkTransform = true
  LinkedObject = -> Link [Hole004.Edge104]
  _LinkVersion = 1
  _Parent = -> Elements
FEATURE [App::FeaturePython] Constraint021  label="Attachment015"  # WARN: FeaturePython — macro-defined, semantics opaque (R4)
  Cascade = false
  Disabled = false
  Group = -> [ElementLink036,ElementLink037]
  Multiply = false
  _ConstraintType = 45
  _LinkVersion = 1
  _Parent = -> Constraints
FEATURE [App::FeaturePython] ElementLink036  label="_Element030"  # link proxy (typed FeaturePython)
  LinkTransform = true
  LinkedObject = -> _Element030
  _LinkVersion = 1
  _Parent = -> Constraint021
FEATURE [Part::FeaturePython] _Element030  # link proxy (typed FeaturePython)
  Detach = false
  LinkTransform = true
  LinkedObject = -> Link006 [10.Edge9]
  _LinkVersion = 1
  _Parent = -> Elements
FEATURE [App::FeaturePython] ElementLink037  label="_Element031"  # link proxy (typed FeaturePython)
  LinkTransform = true
  LinkedObject = -> _Element031
  _LinkVersion = 1
  _Parent = -> Constraint021
FEATURE [Part::FeaturePython] _Element031  # link proxy (typed FeaturePython)
  Detach = false
  LinkTransform = true
  LinkedObject = -> Link [Hole004.Edge98]
  _LinkVersion = 1
  _Parent = -> Elements
FEATURE [App::FeaturePython] Constraint022  label="Attachment016"  # WARN: FeaturePython — macro-defined, semantics opaque (R4)
  Cascade = false
  Disabled = false
  Group = -> [ElementLink038,ElementLink039]
  Multiply = false
  _ConstraintType = 45
  _LinkVersion = 1
  _Parent = -> Constraints
FEATURE [App::FeaturePython] ElementLink038  label="_Element032"  # link proxy (typed FeaturePython)
  LinkTransform = true
  LinkedObject = -> _Element032
  _LinkVersion = 1
  _Parent = -> Constraint022
FEATURE [Part::FeaturePython] _Element032  # link proxy (typed FeaturePython)
  Detach = false
  LinkTransform = true
  LinkedObject = -> Link007 [0.Edge9]
  _LinkVersion = 1
  _Parent = -> Elements
FEATURE [App::FeaturePython] ElementLink039  label="_Element033"  # link proxy (typed FeaturePython)
  LinkTransform = true
  LinkedObject = -> _Element033
  _LinkVersion = 1
  _Parent = -> Constraint022
FEATURE [Part::FeaturePython] _Element033  # link proxy (typed FeaturePython)
  Detach = false
  LinkTransform = true
  LinkedObject = -> Link [Hole004.Edge111]
  _LinkVersion = 1
  _Parent = -> Elements
FEATURE [App::FeaturePython] Constraint023  label="Attachment017"  # WARN: FeaturePython — macro-defined, semantics opaque (R4)
  Cascade = false
  Disabled = false
  Group = -> [ElementLink040,ElementLink041]
  Multiply = false
  _ConstraintType = 45
  _LinkVersion = 1
  _Parent = -> Constraints
FEATURE [App::FeaturePython] ElementLink040  label="_Element034"  # link proxy (typed FeaturePython)
  LinkTransform = true
  LinkedObject = -> _Element034
  _LinkVersion = 1
  _Parent = -> Constraint023
FEATURE [Part::FeaturePython] _Element034  # link proxy (typed FeaturePython)
  Detach = false
  LinkTransform = true
  LinkedObject = -> Link007 [1.Edge9]
  _LinkVersion = 1
  _Parent = -> Elements
FEATURE [App::FeaturePython] ElementLink041  label="_Element035"  # link proxy (typed FeaturePython)
  LinkTransform = true
  LinkedObject = -> _Element035
  _LinkVersion = 1
  _Parent = -> Constraint023
FEATURE [Part::FeaturePython] _Element035  # link proxy (typed FeaturePython)
  Detach = false
  LinkTransform = true
  LinkedObject = -> Link [Hole004.Edge133]
  _LinkVersion = 1
  _Parent = -> Elements
FEATURE [App::FeaturePython] Constraint024  label="Attachment018"  # WARN: FeaturePython — macro-defined, semantics opaque (R4)
  Cascade = false
  Disabled = false
  Group = -> [ElementLink042,ElementLink043]
  Multiply = false
  _ConstraintType = 45
  _LinkVersion = 1
  _Parent = -> Constraints
FEATURE [App::FeaturePython] ElementLink042  label="_Element036"  # link proxy (typed FeaturePython)
  LinkTransform = true
  LinkedObject = -> _Element036
  _LinkVersion = 1
  _Parent = -> Constraint024
FEATURE [Part::FeaturePython] _Element036  # link proxy (typed FeaturePython)
  Detach = false
  LinkTransform = true
  LinkedObject = -> Link007 [2.Edge9]
  _LinkVersion = 1
  _Parent = -> Elements
FEATURE [App::FeaturePython] ElementLink043  label="_Element037"  # link proxy (typed FeaturePython)
  LinkTransform = true
  LinkedObject = -> _Element037
  _LinkVersion = 1
  _Parent = -> Constraint024
FEATURE [Part::FeaturePython] _Element037  # link proxy (typed FeaturePython)
  Detach = false
  LinkTransform = true
  LinkedObject = -> Link [Hole004.Edge109]
  _LinkVersion = 1
  _Parent = -> Elements
FEATURE [App::FeaturePython] Constraint025  label="Attachment019"  # WARN: FeaturePython — macro-defined, semantics opaque (R4)
  Cascade = false
  Disabled = false
  Group = -> [ElementLink044,ElementLink045]
  Multiply = false
  _ConstraintType = 45
  _LinkVersion = 1
  _Parent = -> Constraints
FEATURE [App::FeaturePython] ElementLink044  label="_Element038"  # link proxy (typed FeaturePython)
  LinkTransform = true
  LinkedObject = -> _Element038
  _LinkVersion = 1
  _Parent = -> Constraint025
FEATURE [Part::FeaturePython] _Element038  # link proxy (typed FeaturePython)
  Detach = false
  LinkTransform = true
  LinkedObject = -> Link007 [3.Edge9]
  _LinkVersion = 1
  _Parent = -> Elements
FEATURE [App::FeaturePython] ElementLink045  label="_Element039"  # link proxy (typed FeaturePython)
  LinkTransform = true
  LinkedObject = -> _Element039
  _LinkVersion = 1
  _Parent = -> Constraint025
FEATURE [Part::FeaturePython] _Element039  # link proxy (typed FeaturePython)
  Detach = false
  LinkTransform = true
  LinkedObject = -> Link [Hole004.Edge131]
  _LinkVersion = 1
  _Parent = -> Elements
FEATURE [App::FeaturePython] Constraint026  label="Attachment020"  # WARN: FeaturePython — macro-defined, semantics opaque (R4)
  Cascade = false
  Disabled = false
  Group = -> [ElementLink046,ElementLink047]
  Multiply = false
  _ConstraintType = 45
  _LinkVersion = 1
  _Parent = -> Constraints004
FEATURE [App::FeaturePython] ElementLink046  label="_Element040"  # link proxy (typed FeaturePython)
  LinkTransform = true
  LinkedObject = -> _Element040
  _LinkVersion = 1
  _Parent = -> Constraint026
FEATURE [Part::FeaturePython] _Element040  # link proxy (typed FeaturePython)
  Detach = false
  LinkTransform = true
  LinkedObject = -> Link008 [Link008_i3.Edge9]
  _LinkVersion = 1
  _Parent = -> Elements004
FEATURE [App::FeaturePython] ElementLink047  label="_Element041"  # link proxy (typed FeaturePython)
  LinkTransform = true
  LinkedObject = -> _Element041
  _LinkVersion = 1
  _Parent = -> Constraint026
FEATURE [Part::FeaturePython] _Element041  # link proxy (typed FeaturePython)
  Detach = false
  LinkTransform = true
  LinkedObject = -> Link004 [Pad004.Edge27]
  _LinkVersion = 1
  _Parent = -> Elements004
FEATURE [App::FeaturePython] Constraint027  label="Attachment021"  # WARN: FeaturePython — macro-defined, semantics opaque (R4)
  Cascade = false
  Disabled = false
  Group = -> [ElementLink048,ElementLink049]
  Multiply = false
  _ConstraintType = 45
  _LinkVersion = 1
  _Parent = -> Constraints004
FEATURE [App::FeaturePython] ElementLink048  label="_Element042"  # link proxy (typed FeaturePython)
  LinkTransform = true
  LinkedObject = -> _Element042
  _LinkVersion = 1
  _Parent = -> Constraint027
FEATURE [Part::FeaturePython] _Element042  # link proxy (typed FeaturePython)
  Detach = false
  LinkTransform = true
  LinkedObject = -> Link008 [Link008_i2.Edge9]
  _LinkVersion = 1
  _Parent = -> Elements004
FEATURE [App::FeaturePython] ElementLink049  label="_Element043"  # link proxy (typed FeaturePython)
  LinkTransform = true
  LinkedObject = -> _Element043
  _LinkVersion = 1
  _Parent = -> Constraint027
FEATURE [Part::FeaturePython] _Element043  # link proxy (typed FeaturePython)
  Detach = false
  LinkTransform = true
  LinkedObject = -> Link004 [Pad004.Edge24]
  _LinkVersion = 1
  _Parent = -> Elements004
FEATURE [App::FeaturePython] Constraint028  label="Attachment022"  # WARN: FeaturePython — macro-defined, semantics opaque (R4)
  Cascade = false
  Disabled = false
  Group = -> [ElementLink050,ElementLink051]
  Multiply = false
  _ConstraintType = 45
  _LinkVersion = 1
  _Parent = -> Constraints004
FEATURE [App::FeaturePython] ElementLink050  label="_Element044"  # link proxy (typed FeaturePython)
  LinkTransform = true
  LinkedObject = -> _Element044
  _LinkVersion = 1
  _Parent = -> Constraint028
FEATURE [Part::FeaturePython] _Element044  # link proxy (typed FeaturePython)
  Detach = false
  LinkTransform = true
  LinkedObject = -> Link008 [Link008_i1.Edge9]
  _LinkVersion = 1
  _Parent = -> Elements004
FEATURE [App::FeaturePython] ElementLink051  label="_Element045"  # link proxy (typed FeaturePython)
  LinkTransform = true
  LinkedObject = -> _Element045
  _LinkVersion = 1
  _Parent = -> Constraint028
FEATURE [Part::FeaturePython] _Element045  # link proxy (typed FeaturePython)
  Detach = false
  LinkTransform = true
  LinkedObject = -> Link004 [Pad004.Edge21]
  _LinkVersion = 1
  _Parent = -> Elements004
FEATURE [App::FeaturePython] Constraint029  label="Attachment023"  # WARN: FeaturePython — macro-defined, semantics opaque (R4)
  Cascade = false
  Disabled = false
  Group = -> [ElementLink052,ElementLink053]
  Multiply = false
  _ConstraintType = 45
  _LinkVersion = 1
  _Parent = -> Constraints004
FEATURE [App::FeaturePython] ElementLink052  label="_Element046"  # link proxy (typed FeaturePython)
  LinkTransform = true
  LinkedObject = -> _Element046
  _LinkVersion = 1
  _Parent = -> Constraint029
FEATURE [Part::FeaturePython] _Element046  # link proxy (typed FeaturePython)
  Detach = false
  LinkTransform = true
  LinkedObject = -> Link008 [Link008_i0.Edge9]
  _LinkVersion = 1
  _Parent = -> Elements004
FEATURE [App::FeaturePython] ElementLink053  label="_Element047"  # link proxy (typed FeaturePython)
  LinkTransform = true
  LinkedObject = -> _Element047
  _LinkVersion = 1
  _Parent = -> Constraint029
FEATURE [Part::FeaturePython] _Element047  # link proxy (typed FeaturePython)
  Detach = false
  LinkTransform = true
  LinkedObject = -> Link004 [Pad004.Edge18]
  _LinkVersion = 1
  _Parent = -> Elements004
FEATURE [App::FeaturePython] Constraint030  label="Attachment024"  # WARN: FeaturePython — macro-defined, semantics opaque (R4)
  Cascade = false
  Disabled = false
  Group = -> [ElementLink054,ElementLink055]
  Multiply = false
  _ConstraintType = 45
  _LinkVersion = 1
  _Parent = -> Constraints001
FEATURE [App::FeaturePython] ElementLink054  label="_Element048"  # link proxy (typed FeaturePython)
  LinkTransform = true
  LinkedObject = -> _Element048
  _LinkVersion = 1
  _Parent = -> Constraint030
FEATURE [Part::FeaturePython] _Element048  # link proxy (typed FeaturePython)
  Detach = false
  LinkTransform = true
  LinkedObject = -> Link009 [0.Edge9]
  _LinkVersion = 1
  _Parent = -> Elements001
FEATURE [App::FeaturePython] ElementLink055  label="_Element049"  # link proxy (typed FeaturePython)
  LinkTransform = true
  LinkedObject = -> _Element049
  _LinkVersion = 1
  _Parent = -> Constraint030
FEATURE [Part::FeaturePython] _Element049  # link proxy (typed FeaturePython)
  Detach = false
  LinkTransform = true
  LinkedObject = -> Link002 [Pocket003.Edge81]
  _LinkVersion = 1
  _Parent = -> Elements001
FEATURE [App::FeaturePython] Constraint031  label="Attachment025"  # WARN: FeaturePython — macro-defined, semantics opaque (R4)
  Cascade = false
  Disabled = false
  Group = -> [ElementLink056,ElementLink057]
  Multiply = false
  _ConstraintType = 45
  _LinkVersion = 1
  _Parent = -> Constraints001
FEATURE [App::FeaturePython] ElementLink056  label="_Element050"  # link proxy (typed FeaturePython)
  LinkTransform = true
  LinkedObject = -> _Element050
  _LinkVersion = 1
  _Parent = -> Constraint031
FEATURE [Part::FeaturePython] _Element050  # link proxy (typed FeaturePython)
  Detach = false
  LinkTransform = true
  LinkedObject = -> Link009 [1.Edge9]
  _LinkVersion = 1
  _Parent = -> Elements001
FEATURE [App::FeaturePython] ElementLink057  label="_Element051"  # link proxy (typed FeaturePython)
  LinkTransform = true
  LinkedObject = -> _Element051
  _LinkVersion = 1
  _Parent = -> Constraint031
FEATURE [Part::FeaturePython] _Element051  # link proxy (typed FeaturePython)
  Detach = false
  LinkTransform = true
  LinkedObject = -> Link002 [Pocket003.Edge79]
  _LinkVersion = 1
  _Parent = -> Elements001
FEATURE [App::FeaturePython] Constraint032  label="Attachment026"  # WARN: FeaturePython — macro-defined, semantics opaque (R4)
  Cascade = false
  Disabled = false
  Group = -> [ElementLink058,ElementLink059]
  Multiply = false
  _ConstraintType = 45
  _LinkVersion = 1
  _Parent = -> Constraints001
FEATURE [App::FeaturePython] ElementLink058  label="_Element052"  # link proxy (typed FeaturePython)
  LinkTransform = true
  LinkedObject = -> _Element052
  _LinkVersion = 1
  _Parent = -> Constraint032
FEATURE [Part::FeaturePython] _Element052  # link proxy (typed FeaturePython)
  Detach = false
  LinkTransform = true
  LinkedObject = -> Link009 [11.Edge9]
  _LinkVersion = 1
  _Parent = -> Elements001
FEATURE [App::FeaturePython] ElementLink059  label="_Element053"  # link proxy (typed FeaturePython)
  LinkTransform = true
  LinkedObject = -> _Element053
  _LinkVersion = 1
  _Parent = -> Constraint032
FEATURE [Part::FeaturePython] _Element053  # link proxy (typed FeaturePython)
  Detach = false
  LinkTransform = true
  LinkedObject = -> Link002 [Pocket003.Edge85]
  _LinkVersion = 1
  _Parent = -> Elements001
FEATURE [App::FeaturePython] Constraint033  label="Attachment027"  # WARN: FeaturePython — macro-defined, semantics opaque (R4)
  Cascade = false
  Disabled = false
  Group = -> [ElementLink060,ElementLink061]
  Multiply = false
  _ConstraintType = 45
  _LinkVersion = 1
  _Parent = -> Constraints001
FEATURE [App::FeaturePython] ElementLink060  label="_Element054"  # link proxy (typed FeaturePython)
  LinkTransform = true
  LinkedObject = -> _Element054
  _LinkVersion = 1
  _Parent = -> Constraint033
FEATURE [Part::FeaturePython] _Element054  # link proxy (typed FeaturePython)
  Detach = false
  LinkTransform = true
  LinkedObject = -> Link009 [2.Edge9]
  _LinkVersion = 1
  _Parent = -> Elements001
FEATURE [App::FeaturePython] ElementLink061  label="_Element055"  # link proxy (typed FeaturePython)
  LinkTransform = true
  LinkedObject = -> _Element055
  _LinkVersion = 1
  _Parent = -> Constraint033
FEATURE [Part::FeaturePython] _Element055  # link proxy (typed FeaturePython)
  Detach = false
  LinkTransform = true
  LinkedObject = -> Link002 [Pocket003.Edge83]
  _LinkVersion = 1
  _Parent = -> Elements001
FEATURE [App::FeaturePython] Constraint034  label="Attachment028"  # WARN: FeaturePython — macro-defined, semantics opaque (R4)
  Cascade = false
  Disabled = false
  Group = -> [ElementLink062,ElementLink063]
  Multiply = false
  _ConstraintType = 45
  _LinkVersion = 1
  _Parent = -> Constraints001
FEATURE [App::FeaturePython] ElementLink062  label="_Element056"  # link proxy (typed FeaturePython)
  LinkTransform = true
  LinkedObject = -> _Element056
  _LinkVersion = 1
  _Parent = -> Constraint034
FEATURE [Part::FeaturePython] _Element056  # link proxy (typed FeaturePython)
  Detach = false
  LinkTransform = true
  LinkedObject = -> Link009 [12.Edge9]
  _LinkVersion = 1
  _Parent = -> Elements001
FEATURE [App::FeaturePython] ElementLink063  label="_Element057"  # link proxy (typed FeaturePython)
  LinkTransform = true
  LinkedObject = -> _Element057
  _LinkVersion = 1
  _Parent = -> Constraint034
FEATURE [Part::FeaturePython] _Element057  # link proxy (typed FeaturePython)
  Detach = false
  LinkTransform = true
  LinkedObject = -> Link002 [Pocket003.Edge75]
  _LinkVersion = 1
  _Parent = -> Elements001
FEATURE [App::FeaturePython] Constraint035  label="Attachment029"  # WARN: FeaturePython — macro-defined, semantics opaque (R4)
  Cascade = false
  Disabled = false
  Group = -> [ElementLink064,ElementLink065]
  Multiply = false
  _ConstraintType = 45
  _LinkVersion = 1
  _Parent = -> Constraints001
FEATURE [App::FeaturePython] ElementLink064  label="_Element058"  # link proxy (typed FeaturePython)
  LinkTransform = true
  LinkedObject = -> _Element058
  _LinkVersion = 1
  _Parent = -> Constraint035
FEATURE [Part::FeaturePython] _Element058  # link proxy (typed FeaturePython)
  Detach = false
  LinkTransform = true
  LinkedObject = -> Link009 [3.Edge9]
  _LinkVersion = 1
  _Parent = -> Elements001
FEATURE [App::FeaturePython] ElementLink065  label="_Element059"  # link proxy (typed FeaturePython)
  LinkTransform = true
  LinkedObject = -> _Element059
  _LinkVersion = 1
  _Parent = -> Constraint035
FEATURE [Part::FeaturePython] _Element059  # link proxy (typed FeaturePython)
  Detach = false
  LinkTransform = true
  LinkedObject = -> Link002 [Pocket003.Edge67]
  _LinkVersion = 1
  _Parent = -> Elements001
FEATURE [App::FeaturePython] Constraint036  label="Attachment030"  # WARN: FeaturePython — macro-defined, semantics opaque (R4)
  Cascade = false
  Disabled = false
  Group = -> [ElementLink066,ElementLink067]
  Multiply = false
  _ConstraintType = 45
  _LinkVersion = 1
  _Parent = -> Constraints001
FEATURE [App::FeaturePython] ElementLink066  label="_Element060"  # link proxy (typed FeaturePython)
  LinkTransform = true
  LinkedObject = -> _Element060
  _LinkVersion = 1
  _Parent = -> Constraint036
FEATURE [Part::FeaturePython] _Element060  # link proxy (typed FeaturePython)
  Detach = false
  LinkTransform = true
  LinkedObject = -> Link009 [13.Edge9]
  _LinkVersion = 1
  _Parent = -> Elements001
FEATURE [App::FeaturePython] ElementLink067  label="_Element061"  # link proxy (typed FeaturePython)
  LinkTransform = true
  LinkedObject = -> _Element061
  _LinkVersion = 1
  _Parent = -> Constraint036
FEATURE [Part::FeaturePython] _Element061  # link proxy (typed FeaturePython)
  Detach = false
  LinkTransform = true
  LinkedObject = -> Link002 [Pocket003.Edge71]
  _LinkVersion = 1
  _Parent = -> Elements001
FEATURE [App::FeaturePython] Constraint037  label="Attachment031"  # WARN: FeaturePython — macro-defined, semantics opaque (R4)
  Cascade = false
  Disabled = false
  Group = -> [ElementLink068,ElementLink069]
  Multiply = false
  _ConstraintType = 45
  _LinkVersion = 1
  _Parent = -> Constraints001
FEATURE [App::FeaturePython] ElementLink068  label="_Element062"  # link proxy (typed FeaturePython)
  LinkTransform = true
  LinkedObject = -> _Element062
  _LinkVersion = 1
  _Parent = -> Constraint037
FEATURE [Part::FeaturePython] _Element062  # link proxy (typed FeaturePython)
  Detach = false
  LinkTransform = true
  LinkedObject = -> Link009 [4.Edge9]
  _LinkVersion = 1
  _Parent = -> Elements001
FEATURE [App::FeaturePython] ElementLink069  label="_Element063"  # link proxy (typed FeaturePython)
  LinkTransform = true
  LinkedObject = -> _Element063
  _LinkVersion = 1
  _Parent = -> Constraint037
FEATURE [Part::FeaturePython] _Element063  # link proxy (typed FeaturePython)
  Detach = false
  LinkTransform = true
  LinkedObject = -> Link002 [Pocket003.Edge77]
  _LinkVersion = 1
  _Parent = -> Elements001
FEATURE [App::FeaturePython] Constraint038  label="Attachment032"  # WARN: FeaturePython — macro-defined, semantics opaque (R4)
  Cascade = false
  Disabled = false
  Group = -> [ElementLink070,ElementLink071]
  Multiply = false
  _ConstraintType = 45
  _LinkVersion = 1
  _Parent = -> Constraints001
FEATURE [App::FeaturePython] ElementLink070  label="_Element064"  # link proxy (typed FeaturePython)
  LinkTransform = true
  LinkedObject = -> _Element064
  _LinkVersion = 1
  _Parent = -> Constraint038
FEATURE [Part::FeaturePython] _Element064  # link proxy (typed FeaturePython)
  Detach = false
  LinkTransform = true
  LinkedObject = -> Link009 [10.Edge9]
  _LinkVersion = 1
  _Parent = -> Elements001
FEATURE [App::FeaturePython] ElementLink071  label="_Element065"  # link proxy (typed FeaturePython)
  LinkTransform = true
  LinkedObject = -> _Element065
  _LinkVersion = 1
  _Parent = -> Constraint038
FEATURE [Part::FeaturePython] _Element065  # link proxy (typed FeaturePython)
  Detach = false
  LinkTransform = true
  LinkedObject = -> Link002 [Pocket003.Edge108]
  _LinkVersion = 1
  _Parent = -> Elements001
FEATURE [App::FeaturePython] Constraint039  label="Attachment033"  # WARN: FeaturePython — macro-defined, semantics opaque (R4)
  Cascade = false
  Disabled = false
  Group = -> [ElementLink072,ElementLink073]
  Multiply = false
  _ConstraintType = 45
  _LinkVersion = 1
  _Parent = -> Constraints001
FEATURE [App::FeaturePython] ElementLink072  label="_Element066"  # link proxy (typed FeaturePython)
  LinkTransform = true
  LinkedObject = -> _Element066
  _LinkVersion = 1
  _Parent = -> Constraint039
FEATURE [Part::FeaturePython] _Element066  # link proxy (typed FeaturePython)
  Detach = false
  LinkTransform = true
  LinkedObject = -> Link009 [9.Edge9]
  _LinkVersion = 1
  _Parent = -> Elements001
FEATURE [App::FeaturePython] ElementLink073  label="_Element067"  # link proxy (typed FeaturePython)
  LinkTransform = true
  LinkedObject = -> _Element067
  _LinkVersion = 1
  _Parent = -> Constraint039
FEATURE [Part::FeaturePython] _Element067  # link proxy (typed FeaturePython)
  Detach = false
  LinkTransform = true
  LinkedObject = -> Link002 [Pocket003.Edge104]
  _LinkVersion = 1
  _Parent = -> Elements001
FEATURE [App::FeaturePython] Constraint040  label="Attachment034"  # WARN: FeaturePython — macro-defined, semantics opaque (R4)
  Cascade = false
  Disabled = false
  Group = -> [ElementLink074,ElementLink075]
  Multiply = false
  _ConstraintType = 45
  _LinkVersion = 1
  _Parent = -> Constraints001
FEATURE [App::FeaturePython] ElementLink074  label="_Element068"  # link proxy (typed FeaturePython)
  LinkTransform = true
  LinkedObject = -> _Element068
  _LinkVersion = 1
  _Parent = -> Constraint040
FEATURE [Part::FeaturePython] _Element068  # link proxy (typed FeaturePython)
  Detach = false
  LinkTransform = true
  LinkedObject = -> Link009 [8.Edge9]
  _LinkVersion = 1
  _Parent = -> Elements001
FEATURE [App::FeaturePython] ElementLink075  label="_Element069"  # link proxy (typed FeaturePython)
  LinkTransform = true
  LinkedObject = -> _Element069
  _LinkVersion = 1
  _Parent = -> Constraint040
FEATURE [Part::FeaturePython] _Element069  # link proxy (typed FeaturePython)
  Detach = false
  LinkTransform = true
  LinkedObject = -> Link002 [Pocket003.Edge100]
  _LinkVersion = 1
  _Parent = -> Elements001
FEATURE [App::FeaturePython] Constraint041  label="Attachment035"  # WARN: FeaturePython — macro-defined, semantics opaque (R4)
  Cascade = false
  Disabled = false
  Group = -> [ElementLink076,ElementLink077]
  Multiply = false
  _ConstraintType = 45
  _LinkVersion = 1
  _Parent = -> Constraints001
FEATURE [App::FeaturePython] ElementLink076  label="_Element070"  # link proxy (typed FeaturePython)
  LinkTransform = true
  LinkedObject = -> _Element070
  _LinkVersion = 1
  _Parent = -> Constraint041
FEATURE [Part::FeaturePython] _Element070  # link proxy (typed FeaturePython)
  Detach = false
  LinkTransform = true
  LinkedObject = -> Link009 [7.Edge9]
  _LinkVersion = 1
  _Parent = -> Elements001
FEATURE [App::FeaturePython] ElementLink077  label="_Element071"  # link proxy (typed FeaturePython)
  LinkTransform = true
  LinkedObject = -> _Element071
  _LinkVersion = 1
  _Parent = -> Constraint041
FEATURE [Part::FeaturePython] _Element071  # link proxy (typed FeaturePython)
  Detach = false
  LinkTransform = true
  LinkedObject = -> Link002 [Pocket003.Edge102]
  _LinkVersion = 1
  _Parent = -> Elements001
FEATURE [App::FeaturePython] Constraint042  label="Attachment036"  # WARN: FeaturePython — macro-defined, semantics opaque (R4)
  Cascade = false
  Disabled = false
  Group = -> [ElementLink078,ElementLink079]
  Multiply = false
  _ConstraintType = 45
  _LinkVersion = 1
  _Parent = -> Constraints001
FEATURE [App::FeaturePython] ElementLink078  label="_Element072"  # link proxy (typed FeaturePython)
  LinkTransform = true
  LinkedObject = -> _Element072
  _LinkVersion = 1
  _Parent = -> Constraint042
FEATURE [Part::FeaturePython] _Element072  # link proxy (typed FeaturePython)
  Detach = false
  LinkTransform = true
  LinkedObject = -> Link009 [6.Edge9]
  _LinkVersion = 1
  _Parent = -> Elements001
FEATURE [App::FeaturePython] ElementLink079  label="_Element073"  # link proxy (typed FeaturePython)
  LinkTransform = true
  LinkedObject = -> _Element073
  _LinkVersion = 1
  _Parent = -> Constraint042
FEATURE [Part::FeaturePython] _Element073  # link proxy (typed FeaturePython)
  Detach = false
  LinkTransform = true
  LinkedObject = -> Link002 [Pocket003.Edge92]
  _LinkVersion = 1
  _Parent = -> Elements001
FEATURE [App::FeaturePython] Constraint043  label="Attachment037"  # WARN: FeaturePython — macro-defined, semantics opaque (R4)
  Cascade = false
  Disabled = false
  Group = -> [ElementLink080,ElementLink081]
  Multiply = false
  _ConstraintType = 45
  _LinkVersion = 1
  _Parent = -> Constraints001
FEATURE [App::FeaturePython] ElementLink080  label="_Element074"  # link proxy (typed FeaturePython)
  LinkTransform = true
  LinkedObject = -> _Element074
  _LinkVersion = 1
  _Parent = -> Constraint043
FEATURE [Part::FeaturePython] _Element074  # link proxy (typed FeaturePython)
  Detach = false
  LinkTransform = true
  LinkedObject = -> Link009 [5.Edge9]
  _LinkVersion = 1
  _Parent = -> Elements001
FEATURE [App::FeaturePython] ElementLink081  label="_Element075"  # link proxy (typed FeaturePython)
  LinkTransform = true
  LinkedObject = -> _Element075
  _LinkVersion = 1
  _Parent = -> Constraint043
FEATURE [Part::FeaturePython] _Element075  # link proxy (typed FeaturePython)
  Detach = false
  LinkTransform = true
  LinkedObject = -> Link002 [Pocket003.Edge95]
  _LinkVersion = 1
  _Parent = -> Elements001
FEATURE [App::FeaturePython] Constraint044  label="Attachment038"  # WARN: FeaturePython — macro-defined, semantics opaque (R4)
  Cascade = false
  Disabled = false
  Group = -> [ElementLink082,ElementLink083]
  Multiply = false
  _ConstraintType = 45
  _LinkVersion = 1
  _Parent = -> Constraints001
FEATURE [App::FeaturePython] ElementLink082  label="_Element076"  # link proxy (typed FeaturePython)
  LinkTransform = true
  LinkedObject = -> _Element076
  _LinkVersion = 1
  _Parent = -> Constraint044
FEATURE [Part::FeaturePython] _Element076  # link proxy (typed FeaturePython)
  Detach = false
  LinkTransform = true
  LinkedObject = -> Link009 [15.Edge9]
  _LinkVersion = 1
  _Parent = -> Elements001
FEATURE [App::FeaturePython] ElementLink083  label="_Element077"  # link proxy (typed FeaturePython)
  LinkTransform = true
  LinkedObject = -> _Element077
  _LinkVersion = 1
  _Parent = -> Constraint044
FEATURE [Part::FeaturePython] _Element077  # link proxy (typed FeaturePython)
  Detach = false
  LinkTransform = true
  LinkedObject = -> Link002 [Pocket003.Edge106]
  _LinkVersion = 1
  _Parent = -> Elements001
FEATURE [App::FeaturePython] Constraint045  label="Attachment039"  # WARN: FeaturePython — macro-defined, semantics opaque (R4)
  Cascade = false
  Disabled = false
  Group = -> [ElementLink084,ElementLink085]
  Multiply = false
  _ConstraintType = 45
  _LinkVersion = 1
  _Parent = -> Constraints001
FEATURE [App::FeaturePython] ElementLink084  label="_Element078"  # link proxy (typed FeaturePython)
  LinkTransform = true
  LinkedObject = -> _Element078
  _LinkVersion = 1
  _Parent = -> Constraint045
FEATURE [Part::FeaturePython] _Element078  # link proxy (typed FeaturePython)
  Detach = false
  LinkTransform = true
  LinkedObject = -> Link009 [14.Edge9]
  _LinkVersion = 1
  _Parent = -> Elements001
FEATURE [App::FeaturePython] ElementLink085  label="_Element079"  # link proxy (typed FeaturePython)
  LinkTransform = true
  LinkedObject = -> _Element079
  _LinkVersion = 1
  _Parent = -> Constraint045
FEATURE [Part::FeaturePython] _Element079  # link proxy (typed FeaturePython)
  Detach = false
  LinkTransform = true
  LinkedObject = -> Link002 [Pocket003.Edge110]
  _LinkVersion = 1
  _Parent = -> Elements001
FEATURE [App::FeaturePython] Constraint046  label="Attachment040"  # WARN: FeaturePython — macro-defined, semantics opaque (R4)
  Cascade = false
  Disabled = false
  Group = -> [ElementLink086,ElementLink087]
  Multiply = false
  _ConstraintType = 45
  _LinkVersion = 1
  _Parent = -> Constraints001
FEATURE [App::FeaturePython] ElementLink086  label="_Element080"  # link proxy (typed FeaturePython)
  LinkTransform = true
  LinkedObject = -> _Element080
  _LinkVersion = 1
  _Parent = -> Constraint046
FEATURE [Part::FeaturePython] _Element080  # link proxy (typed FeaturePython)
  Detach = false
  LinkTransform = true
  LinkedObject = -> Link010 [0.Edge9]
  _LinkVersion = 1
  _Parent = -> Elements001
FEATURE [App::FeaturePython] ElementLink087  label="_Element081"  # link proxy (typed FeaturePython)
  LinkTransform = true
  LinkedObject = -> _Element081
  _LinkVersion = 1
  _Parent = -> Constraint046
FEATURE [Part::FeaturePython] _Element081  # link proxy (typed FeaturePython)
  Detach = false
  LinkTransform = true
  LinkedObject = -> Link002 [Pocket003.Edge87]
  _LinkVersion = 1
  _Parent = -> Elements001
FEATURE [App::FeaturePython] Constraint047  label="Attachment041"  # WARN: FeaturePython — macro-defined, semantics opaque (R4)
  Cascade = false
  Disabled = false
  Group = -> [ElementLink088,ElementLink089]
  Multiply = false
  _ConstraintType = 45
  _LinkVersion = 1
  _Parent = -> Constraints001
FEATURE [App::FeaturePython] ElementLink088  label="_Element082"  # link proxy (typed FeaturePython)
  LinkTransform = true
  LinkedObject = -> _Element082
  _LinkVersion = 1
  _Parent = -> Constraint047
FEATURE [Part::FeaturePython] _Element082  # link proxy (typed FeaturePython)
  Detach = false
  LinkTransform = true
  LinkedObject = -> Link010 [1.Edge9]
  _LinkVersion = 1
  _Parent = -> Elements001
FEATURE [App::FeaturePython] ElementLink089  label="_Element083"  # link proxy (typed FeaturePython)
  LinkTransform = true
  LinkedObject = -> _Element083
  _LinkVersion = 1
  _Parent = -> Constraint047
FEATURE [Part::FeaturePython] _Element083  # link proxy (typed FeaturePython)
  Detach = false
  LinkTransform = true
  LinkedObject = -> Link002 [Pocket003.Edge98]
  _LinkVersion = 1
  _Parent = -> Elements001
FEATURE [App::FeaturePython] Constraint048  label="Attachment042"  # WARN: FeaturePython — macro-defined, semantics opaque (R4)
  Cascade = false
  Disabled = false
  Group = -> [ElementLink090,ElementLink091]
  Multiply = false
  _ConstraintType = 45
  _LinkVersion = 1
  _Parent = -> Constraints001
FEATURE [App::FeaturePython] ElementLink090  label="_Element084"  # link proxy (typed FeaturePython)
  LinkTransform = true
  LinkedObject = -> _Element084
  _LinkVersion = 1
  _Parent = -> Constraint048
FEATURE [Part::FeaturePython] _Element084  # link proxy (typed FeaturePython)
  Detach = false
  LinkTransform = true
  LinkedObject = -> Link010 [2.Edge9]
  _LinkVersion = 1
  _Parent = -> Elements001
FEATURE [App::FeaturePython] ElementLink091  label="_Element085"  # link proxy (typed FeaturePython)
  LinkTransform = true
  LinkedObject = -> _Element085
  _LinkVersion = 1
  _Parent = -> Constraint048
FEATURE [Part::FeaturePython] _Element085  # link proxy (typed FeaturePython)
  Detach = false
  LinkTransform = true
  LinkedObject = -> Link002 [Pocket003.Edge73]
  _LinkVersion = 1
  _Parent = -> Elements001
FEATURE [App::FeaturePython] Constraint049  label="Attachment043"  # WARN: FeaturePython — macro-defined, semantics opaque (R4)
  Cascade = false
  Disabled = false
  Group = -> [ElementLink092,ElementLink093]
  Multiply = false
  _ConstraintType = 45
  _LinkVersion = 1
  _Parent = -> Constraints001
FEATURE [App::FeaturePython] ElementLink092  label="_Element086"  # link proxy (typed FeaturePython)
  LinkTransform = true
  LinkedObject = -> _Element086
  _LinkVersion = 1
  _Parent = -> Constraint049
FEATURE [Part::FeaturePython] _Element086  # link proxy (typed FeaturePython)
  Detach = false
  LinkTransform = true
  LinkedObject = -> Link010 [3.Edge9]
  _LinkVersion = 1
  _Parent = -> Elements001
FEATURE [App::FeaturePython] ElementLink093  label="_Element087"  # link proxy (typed FeaturePython)
  LinkTransform = true
  LinkedObject = -> _Element087
  _LinkVersion = 1
  _Parent = -> Constraint049
FEATURE [Part::FeaturePython] _Element087  # link proxy (typed FeaturePython)
  Detach = false
  LinkTransform = true
  LinkedObject = -> Link002 [Pocket003.Edge89]
  _LinkVersion = 1
  _Parent = -> Elements001
FEATURE [Part::FeaturePython] Element051  label="limit-bolt-mate"  # link proxy (typed FeaturePython)
  Detach = false
  LinkTransform = true
  LinkedObject = -> Link [Pocket004.Edge12]
  _LinkVersion = 1
  _Parent = -> Elements
FEATURE [Part::FeaturePython] _Element090  # link proxy (typed FeaturePython)
  Detach = false
  LinkTransform = true
  LinkedObject = -> Link012 [Edge13]
  _LinkVersion = 1
  _Parent = -> Elements
FEATURE [App::FeaturePython] Constraint052  label="Attachment046"  # WARN: FeaturePython — macro-defined, semantics opaque (R4)
  Cascade = false
  Disabled = false
  Group = -> [ElementLink098,ElementLink099]
  Multiply = false
  _ConstraintType = 45
  _LinkVersion = 1
  _Parent = -> Constraints
FEATURE [App::FeaturePython] ElementLink098  label="limit-bolt-mate"  # link proxy (typed FeaturePython)
  LinkTransform = true
  LinkedObject = -> Element051
  _LinkVersion = 1
  _Parent = -> Constraint052
FEATURE [App::FeaturePython] ElementLink099  label="_Element091"  # link proxy (typed FeaturePython)
  LinkTransform = true
  LinkedObject = -> _Element091
  Offset = pos=(0,0,20) rot=(0,0,1;0rad)
  Placement = pos=(-20,0,-7.1e-15) rot=(0,0,1;0rad)
  _LinkVersion = 1
  _Parent = -> Constraint052
FEATURE [Part::FeaturePython] _Element091  # link proxy (typed FeaturePython)
  Detach = false
  LinkTransform = true
  LinkedObject = -> Link011 [Edge43]
  _LinkVersion = 1
  _Parent = -> Elements
FEATURE [App::FeaturePython] Constraint053  label="Attachment047"  # WARN: FeaturePython — macro-defined, semantics opaque (R4)
  Cascade = false
  Disabled = false
  Group = -> [ElementLink100,ElementLink101]
  Multiply = false
  _ConstraintType = 45
  _LinkVersion = 1
  _Parent = -> Constraints
FEATURE [App::FeaturePython] ElementLink100  label="limit-bolt-mate"  # link proxy (typed FeaturePython)
  LinkTransform = true
  LinkedObject = -> Element051
  _LinkVersion = 1
  _Parent = -> Constraint053
FEATURE [App::FeaturePython] ElementLink101  label="_Element090"  # link proxy (typed FeaturePython)
  LinkTransform = true
  LinkedObject = -> _Element090
  _LinkVersion = 1
  _Parent = -> Constraint053
FEATURE [Part::FeaturePython] Element052  label="limit-mate"  # link proxy (typed FeaturePython)
  Detach = false
  LinkTransform = true
  LinkedObject = -> Link004 [Pocket005.Edge18]
  _LinkVersion = 1
  _Parent = -> Elements004
FEATURE [Part::FeaturePython] Element053  label="limit-bolt-mate"  # link proxy (typed FeaturePython)
  Detach = false
  LinkTransform = true
  LinkedObject = -> Link002 [Pocket006.Edge5]
  _LinkVersion = 1
  _Parent = -> Elements001
FEATURE [App::FeaturePython] Constraint054  label="Attachment048"  # WARN: FeaturePython — macro-defined, semantics opaque (R4)
  Cascade = false
  Disabled = false
  Group = -> [ElementLink102,ElementLink103]
  Multiply = false
  _ConstraintType = 45
  _LinkVersion = 1
  _Parent = -> Constraints001
FEATURE [App::FeaturePython] ElementLink102  label="limit-bolt-mate"  # link proxy (typed FeaturePython)
  LinkTransform = true
  LinkedObject = -> Element053
  _LinkVersion = 1
  _Parent = -> Constraint054
FEATURE [App::FeaturePython] ElementLink103  label="_Element092"  # link proxy (typed FeaturePython)
  LinkTransform = true
  LinkedObject = -> _Element092
  _LinkVersion = 1
  _Parent = -> Constraint054
FEATURE [Part::FeaturePython] _Element092  # link proxy (typed FeaturePython)
  Detach = false
  LinkTransform = true
  LinkedObject = -> Link013 [Edge5]
  _LinkVersion = 1
  _Parent = -> Elements001
FEATURE [App::FeaturePython] Constraint055  label="Attachment049"  # WARN: FeaturePython — macro-defined, semantics opaque (R4)
  Cascade = false
  Disabled = false
  Group = -> [ElementLink104,ElementLink105]
  Multiply = false
  _ConstraintType = 45
  _LinkVersion = 1
  _Parent = -> Constraints001
FEATURE [App::FeaturePython] ElementLink104  label="_Element093"  # link proxy (typed FeaturePython)
  LinkTransform = true
  LinkedObject = -> _Element093
  _LinkVersion = 1
  _Parent = -> Constraint055
FEATURE [Part::FeaturePython] _Element093  # link proxy (typed FeaturePython)
  Detach = false
  LinkTransform = true
  LinkedObject = -> Link013 [Edge1]
  _LinkVersion = 1
  _Parent = -> Elements001
FEATURE [App::FeaturePython] ElementLink105  label="_Element094"  # link proxy (typed FeaturePython)
  LinkTransform = true
  LinkedObject = -> _Element094
  _LinkVersion = 1
  _Parent = -> Constraint055
FEATURE [Part::FeaturePython] _Element094  # link proxy (typed FeaturePython)
  Detach = false
  LinkTransform = true
  LinkedObject = -> Link015 [Edge13]
  _LinkVersion = 1
  _Parent = -> Elements001
FEATURE [App::FeaturePython] Constraint056  label="Attachment-limit-bolt"  # WARN: FeaturePython — macro-defined, semantics opaque (R4)
  Cascade = false
  Disabled = false
  Group = -> [ElementLink106,ElementLink107]
  Multiply = false
  _ConstraintType = 45
  _LinkVersion = 1
  _Parent = -> Constraints001
FEATURE [App::FeaturePython] ElementLink106  label="_Element095"  # link proxy (typed FeaturePython)
  LinkTransform = true
  LinkedObject = -> _Element095
  Offset = pos=(0,0,10) rot=(0,0,1;0rad)
  Placement = pos=(0,0,10) rot=(0,0,1;0rad)
  _LinkVersion = 1
  _Parent = -> Constraint056
FEATURE [Part::FeaturePython] _Element095  # link proxy (typed FeaturePython)
  Detach = false
  LinkTransform = true
  LinkedObject = -> Link014 [Edge43]
  _LinkVersion = 1
  _Parent = -> Elements001
FEATURE [App::FeaturePython] ElementLink107  label="limit-bolt-mate"  # link proxy (typed FeaturePython)
  LinkTransform = true
  LinkedObject = -> Element053
  _LinkVersion = 1
  _Parent = -> Constraint056
note: 2 file-system paths scrubbed to <path> (originals preserved in the JSON sidecar)
